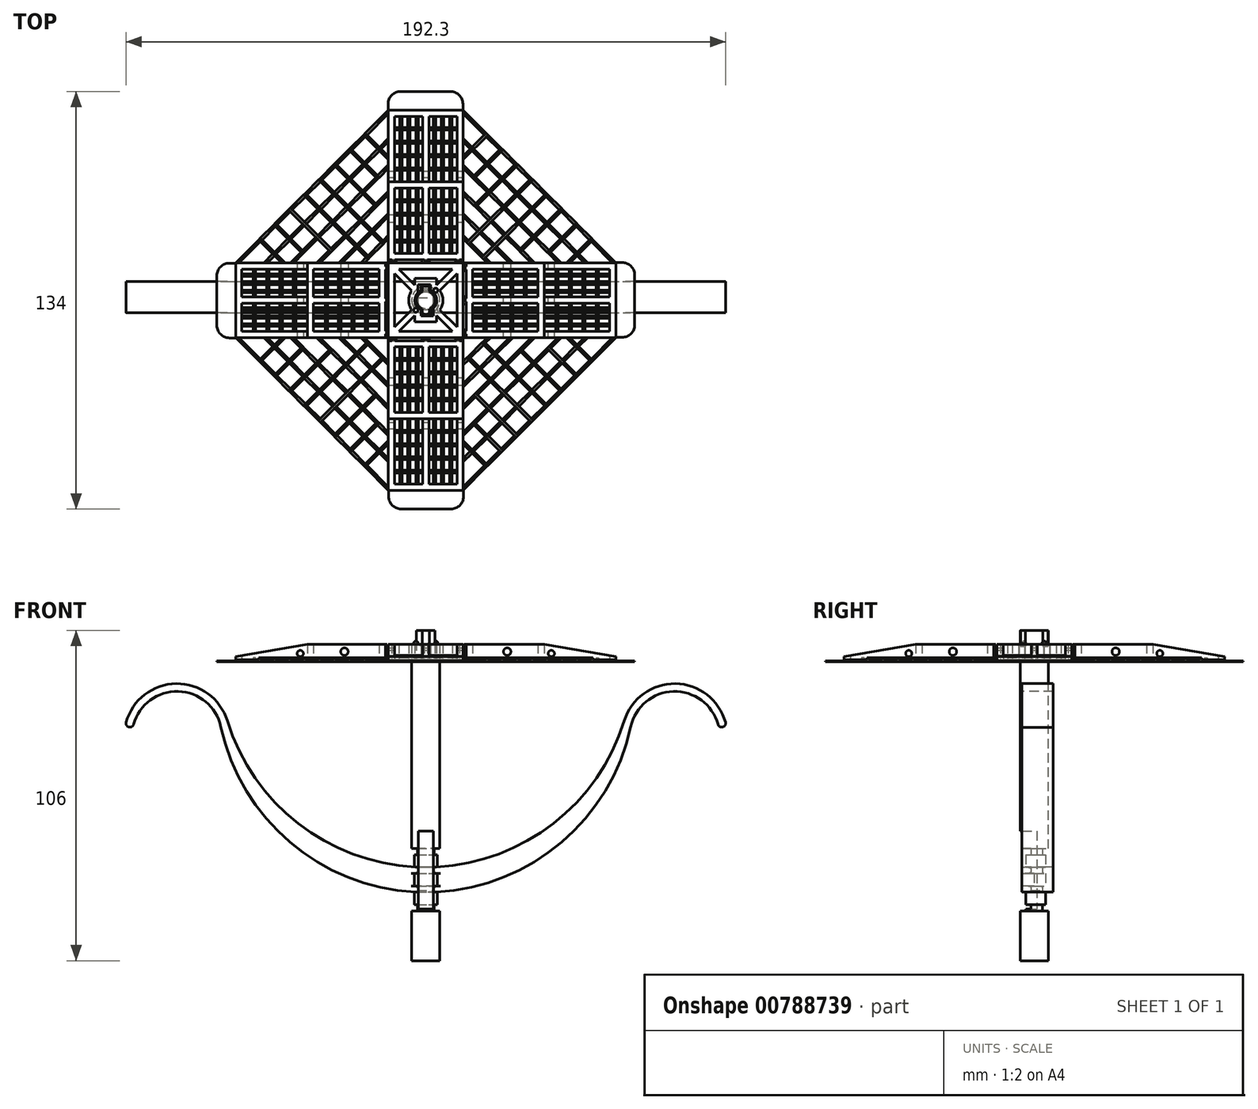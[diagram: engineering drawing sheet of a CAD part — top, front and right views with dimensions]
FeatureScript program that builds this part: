
annotation { "Feature Type Name" : "Feature", "Feature Type Description" : "" }
export const myFeature = defineFeature(function(context is Context, id is Id, definition is map)
    precondition{}
    {
        {
            var Q0;
            Q0=qCreatedBy(makeId("Top.planeOp"),FACE);
            var sketch = newSketch(context, id + "F0", { "sketchPlane" : qUnion([Q0])});
            skLineSegment(sketch, "E0", {"start": v(0, -70.19) * mm, "end": v(0, 72.49) * mm, "construction": true});
            skLineSegment(sketch, "E1", {"start": v(-72.03, 0) * mm, "end": v(73.38, 0) * mm, "construction": true});
            skLineSegment(sketch, "E2", {"start": v(-51.26, -51.26) * mm, "end": v(59.52, 59.52) * mm, "construction": true});
            skLineSegment(sketch, "E3", {"start": v(-54.32, 54.32) * mm, "end": v(52.75, -52.75) * mm, "construction": true});
            skCircle(sketch, "E4", {"center": v(0, 0) * mm, "radius": 3.5 * mm, "construction": true});
            skCircle(sketch, "E5", {"center": v(0, 0) * mm, "radius": 4.5 * mm, "construction": true});
            skSolve(sketch);
        }
        {
            var Q0;
            Q0=qCreatedBy(makeId("Top.planeOp"),FACE);
            var sketch = newSketch(context, id + "F1", { "sketchPlane" : qUnion([Q0])});
            skLineSegment(sketch, "E6.bottom", {"start": v(12, 12) * mm, "end": v(-12, 12) * mm});
            skLineSegment(sketch, "E6.top", {"start": v(12, -12) * mm, "end": v(-12, -12) * mm});
            skLineSegment(sketch, "E6.left", {"start": v(12, 12) * mm, "end": v(12, -12) * mm});
            skLineSegment(sketch, "E6.right", {"start": v(-12, 12) * mm, "end": v(-12, -12) * mm});
            skPoint(sketch, "E6.middle", {"position": v(0, 0) * mm});
            skLineSegment(sketch, "E7.bottom", {"start": v(1.5, -5) * mm, "end": v(-1.5, -5) * mm});
            skLineSegment(sketch, "E7.top", {"start": v(1.5, 5) * mm, "end": v(-1.5, 5) * mm});
            skLineSegment(sketch, "E7.left", {"start": v(1.5, -5) * mm, "end": v(1.5, -3.16) * mm});
            skLineSegment(sketch, "E7.right", {"start": v(-1.5, -5) * mm, "end": v(-1.5, -3.16) * mm});
            skLineSegment(sketch, "E8.bottom", {"start": v(8.59, 10) * mm, "end": v(1, 10) * mm});
            skLineSegment(sketch, "E8.top", {"start": v(8.59, -10) * mm, "end": v(1, -10) * mm});
            skLineSegment(sketch, "E8.left", {"start": v(10, 8.59) * mm, "end": v(10, -8.59) * mm});
            skLineSegment(sketch, "E8.right", {"start": v(-10, 8.59) * mm, "end": v(-10, -8.59) * mm});
            skLineSegment(sketch, "E9.trimOffspring", {"start": v(-1.5, 3.16) * mm, "end": v(-1.5, 5) * mm});
            skLineSegment(sketch, "E10.trimOffspring", {"start": v(1.5, 3.16) * mm, "end": v(1.5, 5) * mm});
            skLineSegment(sketch, "E11.left", {"start": v(10, -1) * mm, "end": v(10, 1) * mm});
            skLineSegment(sketch, "E11.right", {"start": v(-10, -1) * mm, "end": v(-10, 1) * mm});
            skPoint(sketch, "E12.middle", {"position": v(0, 8.75) * mm});
            skPoint(sketch, "E12.middle.positionSnap0", {"position": v(0, 10) * mm});
            skPoint(sketch, "E12.centerSnap0", {"position": v(0, 10) * mm});
            skPoint(sketch, "E13.middle", {"position": v(0, -8.75) * mm});
            skPoint(sketch, "E13.cornerSnap0", {"position": v(0, -10) * mm});
            skLineSegment(sketch, "E14.trimOffspring", {"start": v(-1, 10) * mm, "end": v(-8.59, 10) * mm});
            skLineSegment(sketch, "E15.trimOffspring", {"start": v(-1, -10) * mm, "end": v(-8.59, -10) * mm});
            skArc(sketch, "E16", {"start": v(1.5, -3.16) * mm, "mid": v(3.5, 0) * mm, "end": v(1.5, 3.16) * mm});
            skLineSegment(sketch, "E17", {"start": v(-10, -8.59) * mm, "end": v(-4.53, -3.12) * mm});
            skLineSegment(sketch, "E18", {"start": v(-8.59, -10) * mm, "end": v(-3.5, -4.91) * mm});
            skLineSegment(sketch, "E19", {"start": v(-10, 8.59) * mm, "end": v(-4.53, 3.12) * mm});
            skLineSegment(sketch, "E20", {"start": v(10, -8.59) * mm, "end": v(4.53, -3.12) * mm});
            skPoint(sketch, "E21.orphan", {"position": v(-10, -10) * mm});
            skPoint(sketch, "E22.orphan", {"position": v(10, -10) * mm});
            skPoint(sketch, "E23.orphan", {"position": v(10, 10) * mm});
            skPoint(sketch, "E24.orphan", {"position": v(-10, 10) * mm});
            skArc(sketch, "E25.trimOffspring", {"start": v(-4.53, 3.12) * mm, "mid": v(-5.5, 0) * mm, "end": v(-4.53, -3.12) * mm});
            skLineSegment(sketch, "E26.trimOffspring", {"start": v(-3.5, 4.91) * mm, "end": v(-8.59, 10) * mm});
            skLineSegment(sketch, "E27.trimOffspring", {"start": v(4.53, 3.12) * mm, "end": v(10, 8.59) * mm});
            skLineSegment(sketch, "E28.trimOffspring", {"start": v(3.5, 4.91) * mm, "end": v(8.59, 10) * mm});
            skLineSegment(sketch, "E29.trimOffspring", {"start": v(3.5, -4.91) * mm, "end": v(8.59, -10) * mm});
            skArc(sketch, "E30.trimOffspring", {"start": v(4.53, -3.12) * mm, "mid": v(5.5, 0) * mm, "end": v(4.53, 3.12) * mm});
            skLineSegment(sketch, "E31.bottom", {"start": v(3.5, -7) * mm, "end": v(-3.5, -7) * mm});
            skLineSegment(sketch, "E31.top", {"start": v(3.5, 7) * mm, "end": v(-3.5, 7) * mm});
            skLineSegment(sketch, "E31.left", {"start": v(3.5, -7) * mm, "end": v(3.5, -4.91) * mm});
            skLineSegment(sketch, "E31.right", {"start": v(-3.5, -7) * mm, "end": v(-3.5, -4.91) * mm});
            skLineSegment(sketch, "E32", {"start": v(-1, -10) * mm, "end": v(1, -10) * mm});
            skLineSegment(sketch, "E33", {"start": v(1, 10) * mm, "end": v(-1, 10) * mm});
            skLineSegment(sketch, "E34.trimOffspring", {"start": v(-3.5, 0) * mm, "end": v(-3.5, 7) * mm});
            skArc(sketch, "E35.trimOffspring", {"start": v(-1.5, 3.16) * mm, "mid": v(-3.5, 0) * mm, "end": v(-1.5, -3.16) * mm});
            skLineSegment(sketch, "E36.trimOffspring", {"start": v(3.5, 4.91) * mm, "end": v(3.5, 7) * mm});
            skSolve(sketch);
        }
        {
            var Q0;
            Q0 = qSketchRegion(id + "F1", true);
            extrude(context, id + "F2", {"entities" : qUnion([Q0]), "depth" : 5 * mm, "offsetDistance" : 25 * mm, "hasSecondDirection" : true, "secondDirectionOppositeDirection" : true, "secondDirectionDepth" : .6 * mm});
        }
        {
            var Q0;
            Q0=qCreatedBy(makeId("Top.planeOp"),FACE);
            var sketch = newSketch(context, id + "F3", { "sketchPlane" : qUnion([Q0])});
            skLineSegment(sketch, "E37.bottom", {"start": v(-13, 12) * mm, "end": v(-61, 12) * mm});
            skLineSegment(sketch, "E37.top", {"start": v(-13, -12) * mm, "end": v(-61, -12) * mm});
            skLineSegment(sketch, "E37.left", {"start": v(-13, 12) * mm, "end": v(-13, -12) * mm});
            skLineSegment(sketch, "E37.right", {"start": v(-61, 12) * mm, "end": v(-61, -12) * mm});
            skPoint(sketch, "E37.middle", {"position": v(-37, 0) * mm});
            skLineSegment(sketch, "E38.bottom", {"start": v(-15, 10) * mm, "end": v(-36, 10) * mm});
            skLineSegment(sketch, "E38.top", {"start": v(-15, -10) * mm, "end": v(-36, -10) * mm});
            skLineSegment(sketch, "E38.left", {"start": v(-15, 10) * mm, "end": v(-15, 1) * mm});
            skLineSegment(sketch, "E38.right", {"start": v(-59, 10) * mm, "end": v(-59, 1) * mm});
            skLineSegment(sketch, "E39.bottom", {"start": v(-15, 1) * mm, "end": v(-36, 1) * mm});
            skLineSegment(sketch, "E39.top", {"start": v(-15, -1) * mm, "end": v(-36, -1) * mm});
            skLineSegment(sketch, "E40.left", {"start": v(-36, 10) * mm, "end": v(-36, 1) * mm});
            skLineSegment(sketch, "E40.right", {"start": v(-38, 10) * mm, "end": v(-38, 1) * mm});
            skLineSegment(sketch, "E41.trimOffspring", {"start": v(-38, 10) * mm, "end": v(-59, 10) * mm});
            skLineSegment(sketch, "E42.trimOffspring", {"start": v(-15, -1) * mm, "end": v(-15, -10) * mm});
            skLineSegment(sketch, "E43.trimOffspring", {"start": v(-38, -10) * mm, "end": v(-59, -10) * mm});
            skLineSegment(sketch, "E44.trimOffspring", {"start": v(-38, -1) * mm, "end": v(-59, -1) * mm});
            skLineSegment(sketch, "E45.trimOffspring", {"start": v(-38, 1) * mm, "end": v(-59, 1) * mm});
            skLineSegment(sketch, "E46.trimOffspring", {"start": v(-36, -1) * mm, "end": v(-36, -10) * mm});
            skLineSegment(sketch, "E47.trimOffspring", {"start": v(-38, -1) * mm, "end": v(-38, -10) * mm});
            skLineSegment(sketch, "E48.trimOffspring", {"start": v(-59, -1) * mm, "end": v(-59, -10) * mm});
            skSolve(sketch);
        }
        {
            var Q0;
            Q0 = qSketchRegion(id + "F3", true);
            extrude(context, id + "F4", {"entities" : qUnion([Q0]), "depth" : 5 * mm, "offsetDistance" : 25 * mm, "hasSecondDirection" : true, "secondDirectionOppositeDirection" : true, "secondDirectionDepth" : .6 * mm});
        }
        {
            var Q0;
            Q0=qCreatedBy(makeId("Front.planeOp"),FACE);
            var sketch = newSketch(context, id + "F5", { "sketchPlane" : qUnion([Q0])});
            skLineSegment(sketch, "E49", {"start": v(0, 58.8) * mm, "end": v(0, -68.64) * mm, "construction": true});
            skSolve(sketch);
        }
        {
            var Q0;
            Q0=makeQuery(id+"F4.opExtrude","SWEPT_BODY",BODY,{"disambiguationData":[OSD([sQuery(id+"F3.wireOp",EDGE,"E37.bottom"),sQuery(id+"F3.wireOp",EDGE,"E37.top"),sQuery(id+"F3.wireOp",EDGE,"E37.left"),sQuery(id+"F3.wireOp",EDGE,"E37.right"),sQuery(id+"F3.wireOp",EDGE,"E38.bottom"),sQuery(id+"F3.wireOp",EDGE,"E38.top"),sQuery(id+"F3.wireOp",EDGE,"E38.left"),sQuery(id+"F3.wireOp",EDGE,"E38.right"),sQuery(id+"F3.wireOp",EDGE,"E39.bottom"),sQuery(id+"F3.wireOp",EDGE,"E39.top"),sQuery(id+"F3.wireOp",EDGE,"E40.left"),sQuery(id+"F3.wireOp",EDGE,"E40.right"),sQuery(id+"F3.wireOp",EDGE,"E41.trimOffspring"),sQuery(id+"F3.wireOp",EDGE,"E42.trimOffspring"),sQuery(id+"F3.wireOp",EDGE,"E43.trimOffspring"),sQuery(id+"F3.wireOp",EDGE,"E44.trimOffspring"),sQuery(id+"F3.wireOp",EDGE,"E45.trimOffspring"),sQuery(id+"F3.wireOp",EDGE,"E46.trimOffspring"),sQuery(id+"F3.wireOp",EDGE,"E47.trimOffspring"),sQuery(id+"F3.wireOp",EDGE,"E48.trimOffspring")])]});
            var Q1;
            Q1=sQuery(id+"F5.wireOp",EDGE,"E49");
            circularPattern(context, id + "F6", {"entities" : qUnion([Q0]), "axis" : qUnion([Q1]), "angle" : 360 * degree, "instanceCount" : 4, "equalSpace" : true});
        }
        {
            var Q0;
            Q0=qCreatedBy(makeId("Top.planeOp"),FACE);
            var sketch = newSketch(context, id + "F7", { "sketchPlane" : qUnion([Q0])});
            skLineSegment(sketch, "E50", {"start": v(-61, 12) * mm, "end": v(-61, -12) * mm});
            skLineSegment(sketch, "E51", {"start": v(-61, -12) * mm, "end": v(-12, -61) * mm});
            skLineSegment(sketch, "E52", {"start": v(-12, -61) * mm, "end": v(12, -61) * mm});
            skLineSegment(sketch, "E53", {"start": v(12, -61) * mm, "end": v(61, -12) * mm});
            skLineSegment(sketch, "E54", {"start": v(61, -12) * mm, "end": v(61, 12) * mm});
            skLineSegment(sketch, "E55", {"start": v(61, 12) * mm, "end": v(12, 61) * mm});
            skLineSegment(sketch, "E56", {"start": v(12, 61) * mm, "end": v(-12, 61) * mm});
            skLineSegment(sketch, "E57", {"start": v(-12, 61) * mm, "end": v(-61, 12) * mm});
            skLineSegment(sketch, "E58", {"start": v(-60.2, -11.67) * mm, "end": v(-11.67, -60.2) * mm});
            skLineSegment(sketch, "E59", {"start": v(-11.67, -60.2) * mm, "end": v(11.67, -60.2) * mm});
            skLineSegment(sketch, "E60", {"start": v(11.67, -60.2) * mm, "end": v(60.2, -11.67) * mm});
            skLineSegment(sketch, "E61", {"start": v(60.2, -11.67) * mm, "end": v(60.2, 11.67) * mm});
            skLineSegment(sketch, "E62", {"start": v(60.2, 11.67) * mm, "end": v(11.67, 60.2) * mm});
            skLineSegment(sketch, "E63", {"start": v(11.67, 60.2) * mm, "end": v(-11.67, 60.2) * mm});
            skLineSegment(sketch, "E64", {"start": v(-11.67, 60.2) * mm, "end": v(-60.2, 11.67) * mm});
            skLineSegment(sketch, "E65", {"start": v(-60.2, 11.67) * mm, "end": v(-60.2, -11.67) * mm});
            skSolve(sketch);
        }
        {
            var Q0;
            Q0 = qSketchRegion(id + "F7", true);
            extrude(context, id + "F8", {"entities" : qUnion([Q0]), "oppositeDirection" : true, "depth" : .6 * mm, "offsetDistance" : 25 * mm});
        }
        {
            var Q0;
            Q0=makeQuery(id+"F4.opExtrude","SWEPT_BODY",BODY,{"disambiguationData":[OSD([sQuery(id+"F3.wireOp",EDGE,"E37.bottom"),sQuery(id+"F3.wireOp",EDGE,"E37.top"),sQuery(id+"F3.wireOp",EDGE,"E37.left"),sQuery(id+"F3.wireOp",EDGE,"E37.right"),sQuery(id+"F3.wireOp",EDGE,"E38.bottom"),sQuery(id+"F3.wireOp",EDGE,"E38.top"),sQuery(id+"F3.wireOp",EDGE,"E38.left"),sQuery(id+"F3.wireOp",EDGE,"E38.right"),sQuery(id+"F3.wireOp",EDGE,"E39.bottom"),sQuery(id+"F3.wireOp",EDGE,"E39.top"),sQuery(id+"F3.wireOp",EDGE,"E40.left"),sQuery(id+"F3.wireOp",EDGE,"E40.right"),sQuery(id+"F3.wireOp",EDGE,"E41.trimOffspring"),sQuery(id+"F3.wireOp",EDGE,"E42.trimOffspring"),sQuery(id+"F3.wireOp",EDGE,"E43.trimOffspring"),sQuery(id+"F3.wireOp",EDGE,"E44.trimOffspring"),sQuery(id+"F3.wireOp",EDGE,"E45.trimOffspring"),sQuery(id+"F3.wireOp",EDGE,"E46.trimOffspring"),sQuery(id+"F3.wireOp",EDGE,"E47.trimOffspring"),sQuery(id+"F3.wireOp",EDGE,"E48.trimOffspring")])]});
            var Q1;
            Q1=makeQuery(id+"F6.opPattern","COPY",BODY,{"derivedFrom":makeQuery(id+"F4.opExtrude","SWEPT_BODY",BODY,{"disambiguationData":[OSD([sQuery(id+"F3.wireOp",EDGE,"E37.bottom"),sQuery(id+"F3.wireOp",EDGE,"E37.top"),sQuery(id+"F3.wireOp",EDGE,"E37.left"),sQuery(id+"F3.wireOp",EDGE,"E37.right"),sQuery(id+"F3.wireOp",EDGE,"E38.bottom"),sQuery(id+"F3.wireOp",EDGE,"E38.top"),sQuery(id+"F3.wireOp",EDGE,"E38.left"),sQuery(id+"F3.wireOp",EDGE,"E38.right"),sQuery(id+"F3.wireOp",EDGE,"E39.bottom"),sQuery(id+"F3.wireOp",EDGE,"E39.top"),sQuery(id+"F3.wireOp",EDGE,"E40.left"),sQuery(id+"F3.wireOp",EDGE,"E40.right"),sQuery(id+"F3.wireOp",EDGE,"E41.trimOffspring"),sQuery(id+"F3.wireOp",EDGE,"E42.trimOffspring"),sQuery(id+"F3.wireOp",EDGE,"E43.trimOffspring"),sQuery(id+"F3.wireOp",EDGE,"E44.trimOffspring"),sQuery(id+"F3.wireOp",EDGE,"E45.trimOffspring"),sQuery(id+"F3.wireOp",EDGE,"E46.trimOffspring"),sQuery(id+"F3.wireOp",EDGE,"E47.trimOffspring"),sQuery(id+"F3.wireOp",EDGE,"E48.trimOffspring")])]}),"instanceName":"1"});
            var Q2;
            Q2=makeQuery(id+"F6.opPattern","COPY",BODY,{"derivedFrom":makeQuery(id+"F4.opExtrude","SWEPT_BODY",BODY,{"disambiguationData":[OSD([sQuery(id+"F3.wireOp",EDGE,"E37.bottom"),sQuery(id+"F3.wireOp",EDGE,"E37.top"),sQuery(id+"F3.wireOp",EDGE,"E37.left"),sQuery(id+"F3.wireOp",EDGE,"E37.right"),sQuery(id+"F3.wireOp",EDGE,"E38.bottom"),sQuery(id+"F3.wireOp",EDGE,"E38.top"),sQuery(id+"F3.wireOp",EDGE,"E38.left"),sQuery(id+"F3.wireOp",EDGE,"E38.right"),sQuery(id+"F3.wireOp",EDGE,"E39.bottom"),sQuery(id+"F3.wireOp",EDGE,"E39.top"),sQuery(id+"F3.wireOp",EDGE,"E40.left"),sQuery(id+"F3.wireOp",EDGE,"E40.right"),sQuery(id+"F3.wireOp",EDGE,"E41.trimOffspring"),sQuery(id+"F3.wireOp",EDGE,"E42.trimOffspring"),sQuery(id+"F3.wireOp",EDGE,"E43.trimOffspring"),sQuery(id+"F3.wireOp",EDGE,"E44.trimOffspring"),sQuery(id+"F3.wireOp",EDGE,"E45.trimOffspring"),sQuery(id+"F3.wireOp",EDGE,"E46.trimOffspring"),sQuery(id+"F3.wireOp",EDGE,"E47.trimOffspring"),sQuery(id+"F3.wireOp",EDGE,"E48.trimOffspring")])]}),"instanceName":"2"});
            var Q3;
            Q3=makeQuery(id+"F6.opPattern","COPY",BODY,{"derivedFrom":makeQuery(id+"F4.opExtrude","SWEPT_BODY",BODY,{"disambiguationData":[OSD([sQuery(id+"F3.wireOp",EDGE,"E37.bottom"),sQuery(id+"F3.wireOp",EDGE,"E37.top"),sQuery(id+"F3.wireOp",EDGE,"E37.left"),sQuery(id+"F3.wireOp",EDGE,"E37.right"),sQuery(id+"F3.wireOp",EDGE,"E38.bottom"),sQuery(id+"F3.wireOp",EDGE,"E38.top"),sQuery(id+"F3.wireOp",EDGE,"E38.left"),sQuery(id+"F3.wireOp",EDGE,"E38.right"),sQuery(id+"F3.wireOp",EDGE,"E39.bottom"),sQuery(id+"F3.wireOp",EDGE,"E39.top"),sQuery(id+"F3.wireOp",EDGE,"E40.left"),sQuery(id+"F3.wireOp",EDGE,"E40.right"),sQuery(id+"F3.wireOp",EDGE,"E41.trimOffspring"),sQuery(id+"F3.wireOp",EDGE,"E42.trimOffspring"),sQuery(id+"F3.wireOp",EDGE,"E43.trimOffspring"),sQuery(id+"F3.wireOp",EDGE,"E44.trimOffspring"),sQuery(id+"F3.wireOp",EDGE,"E45.trimOffspring"),sQuery(id+"F3.wireOp",EDGE,"E46.trimOffspring"),sQuery(id+"F3.wireOp",EDGE,"E47.trimOffspring"),sQuery(id+"F3.wireOp",EDGE,"E48.trimOffspring")])]}),"instanceName":"3"});
            var Q4;
            Q4=makeQuery(id+"F8.opExtrude","SWEPT_BODY",BODY,{"disambiguationData":[OSD([sQuery(id+"F7.wireOp",EDGE,"E50"),sQuery(id+"F7.wireOp",EDGE,"E51"),sQuery(id+"F7.wireOp",EDGE,"E52"),sQuery(id+"F7.wireOp",EDGE,"E53"),sQuery(id+"F7.wireOp",EDGE,"E54"),sQuery(id+"F7.wireOp",EDGE,"E55"),sQuery(id+"F7.wireOp",EDGE,"E56"),sQuery(id+"F7.wireOp",EDGE,"E57"),sQuery(id+"F7.wireOp",EDGE,"E58"),sQuery(id+"F7.wireOp",EDGE,"E59"),sQuery(id+"F7.wireOp",EDGE,"E60"),sQuery(id+"F7.wireOp",EDGE,"E61"),sQuery(id+"F7.wireOp",EDGE,"E62"),sQuery(id+"F7.wireOp",EDGE,"E63"),sQuery(id+"F7.wireOp",EDGE,"E64"),sQuery(id+"F7.wireOp",EDGE,"E65")])]});
            booleanBodies(context, id + "F9", {"operationType" : BooleanOperationType.UNION, "tools" : qUnion([Q0, Q1, Q2, Q3, Q4])});
        }
        {
            var Q0;
            Q0=qCreatedBy(makeId("Top.planeOp"),FACE);
            var sketch = newSketch(context, id + "F10", { "sketchPlane" : qUnion([Q0])});
            skLineSegment(sketch, "E66.bottom", {"start": v(-13, -12) * mm, "end": v(-11.2, -12) * mm});
            skLineSegment(sketch, "E66.top", {"start": v(-13, -11.2) * mm, "end": v(-11.2, -11.2) * mm});
            skLineSegment(sketch, "E66.left", {"start": v(-13, -12) * mm, "end": v(-13, -11.2) * mm});
            skLineSegment(sketch, "E66.right", {"start": v(-11.2, -12) * mm, "end": v(-11.2, -11.2) * mm});
            skLineSegment(sketch, "E67.0.1.0", {"start": v(-13, -9.5) * mm, "end": v(-13, -8.7) * mm});
            skLineSegment(sketch, "E67.0.1.1", {"start": v(-13, -9.5) * mm, "end": v(-11.2, -9.5) * mm});
            skLineSegment(sketch, "E67.0.1.2", {"start": v(-11.2, -9.5) * mm, "end": v(-11.2, -8.7) * mm});
            skLineSegment(sketch, "E67.0.4.0", {"start": v(-13, -2) * mm, "end": v(-13, -1.2) * mm});
            skLineSegment(sketch, "E67.0.4.2", {"start": v(-11.2, -2) * mm, "end": v(-11.2, -1.2) * mm});
            skLineSegment(sketch, "E67.0.4.3", {"start": v(-13, -1.2) * mm, "end": v(-11.2, -1.2) * mm});
            skLineSegment(sketch, "E67.direction1", {"start": v(-13, -12) * mm, "end": v(12, -12) * mm, "construction": true});
            skLineSegment(sketch, "E67.direction2", {"start": v(-13, -12) * mm, "end": v(-13, -9.5) * mm, "construction": true});
            skLineSegment(sketch, "E68.MirrorCS", {"start": v(-13, 12) * mm, "end": v(-13, 11.2) * mm});
            skLineSegment(sketch, "E69.MirrorCS", {"start": v(-13, 2) * mm, "end": v(-13, 1.2) * mm});
            skLineSegment(sketch, "E70.MirrorCS", {"start": v(-13, 12) * mm, "end": v(-13, 9.5) * mm, "construction": true});
            skLineSegment(sketch, "E71.MirrorCS", {"start": v(-13, 1.2) * mm, "end": v(-11.2, 1.2) * mm});
            skLineSegment(sketch, "E72.MirrorCS", {"start": v(-11.2, 12) * mm, "end": v(-11.2, 11.2) * mm});
            skLineSegment(sketch, "E73.MirrorCS", {"start": v(-13, 12) * mm, "end": v(-11.2, 12) * mm});
            skLineSegment(sketch, "E74.MirrorCS", {"start": v(-13, 9.5) * mm, "end": v(-13, 8.7) * mm});
            skLineSegment(sketch, "E75.MirrorCS", {"start": v(-11.2, 2) * mm, "end": v(-11.2, 1.2) * mm});
            skLineSegment(sketch, "E76.MirrorCS", {"start": v(-13, 11.2) * mm, "end": v(-11.2, 11.2) * mm});
            skLineSegment(sketch, "E77.MirrorCS", {"start": v(-11.2, 9.5) * mm, "end": v(-11.2, 8.7) * mm});
            skLineSegment(sketch, "E78.MirrorCS", {"start": v(-13, 9.5) * mm, "end": v(-11.2, 9.5) * mm});
            skLineSegment(sketch, "E79.bottom", {"start": v(-59, -8.4) * mm, "end": v(-15, -8.4) * mm});
            skLineSegment(sketch, "E79.top", {"start": v(-59, -7.6) * mm, "end": v(-15, -7.6) * mm});
            skLineSegment(sketch, "E79.left", {"start": v(-59, -8.4) * mm, "end": v(-59, -7.6) * mm});
            skLineSegment(sketch, "E79.right", {"start": v(-15, -8.4) * mm, "end": v(-15, -7.6) * mm});
            skLineSegment(sketch, "E80.0.1.0", {"start": v(-59, -5.8) * mm, "end": v(-59, -5) * mm});
            skLineSegment(sketch, "E80.0.1.1", {"start": v(-59, -5.8) * mm, "end": v(-15, -5.8) * mm});
            skLineSegment(sketch, "E80.0.1.2", {"start": v(-59, -5) * mm, "end": v(-15, -5) * mm});
            skLineSegment(sketch, "E80.0.1.3", {"start": v(-15, -5.8) * mm, "end": v(-15, -5) * mm});
            skLineSegment(sketch, "E80.0.2.0", {"start": v(-59, -3.2) * mm, "end": v(-59, -2.4) * mm});
            skLineSegment(sketch, "E80.0.2.1", {"start": v(-59, -3.2) * mm, "end": v(-15, -3.2) * mm});
            skLineSegment(sketch, "E80.0.2.2", {"start": v(-59, -2.4) * mm, "end": v(-15, -2.4) * mm});
            skLineSegment(sketch, "E80.0.2.3", {"start": v(-15, -3.2) * mm, "end": v(-15, -2.4) * mm});
            skLineSegment(sketch, "E80.direction1", {"start": v(-59, -8.4) * mm, "end": v(-34, -8.4) * mm, "construction": true});
            skLineSegment(sketch, "E80.direction2", {"start": v(-59, -8.4) * mm, "end": v(-59, -5.8) * mm, "construction": true});
            skLineSegment(sketch, "E81.MirrorCS", {"start": v(-15, 3.2) * mm, "end": v(-15, 2.4) * mm});
            skLineSegment(sketch, "E82.MirrorCS", {"start": v(-59, 3.2) * mm, "end": v(-59, 2.4) * mm});
            skLineSegment(sketch, "E83.MirrorCS", {"start": v(-59, 8.4) * mm, "end": v(-59, 7.6) * mm});
            skLineSegment(sketch, "E84.MirrorCS", {"start": v(-15, 5.8) * mm, "end": v(-15, 5) * mm});
            skLineSegment(sketch, "E85.MirrorCS", {"start": v(-59, 8.4) * mm, "end": v(-34, 8.4) * mm, "construction": true});
            skLineSegment(sketch, "E86.MirrorCS", {"start": v(-59, 5) * mm, "end": v(-15, 5) * mm});
            skLineSegment(sketch, "E87.MirrorCS", {"start": v(-59, 3.2) * mm, "end": v(-15, 3.2) * mm});
            skLineSegment(sketch, "E88.MirrorCS", {"start": v(-59, 5.8) * mm, "end": v(-15, 5.8) * mm});
            skLineSegment(sketch, "E89.MirrorCS", {"start": v(-59, 8.4) * mm, "end": v(-59, 5.8) * mm, "construction": true});
            skLineSegment(sketch, "E90.MirrorCS", {"start": v(-59, 8.4) * mm, "end": v(-15, 8.4) * mm});
            skLineSegment(sketch, "E91.MirrorCS", {"start": v(-59, 7.6) * mm, "end": v(-15, 7.6) * mm});
            skLineSegment(sketch, "E92.MirrorCS", {"start": v(-59, 2.4) * mm, "end": v(-15, 2.4) * mm});
            skLineSegment(sketch, "E93.MirrorCS", {"start": v(-59, 5.8) * mm, "end": v(-59, 5) * mm});
            skLineSegment(sketch, "E94.MirrorCS", {"start": v(-15, 8.4) * mm, "end": v(-15, 7.6) * mm});
            skLineSegment(sketch, "E95.bottom", {"start": v(-13, -12) * mm, "end": v(-15, -12) * mm});
            skLineSegment(sketch, "E95.top", {"start": v(-13, 12) * mm, "end": v(-15, 12) * mm});
            skLineSegment(sketch, "E95.left", {"start": v(-13, -12) * mm, "end": v(-13, 12) * mm});
            skLineSegment(sketch, "E95.right", {"start": v(-15, -12) * mm, "end": v(-15, 8.4) * mm});
            skLineSegment(sketch, "E96", {"start": v(-15, 12) * mm, "end": v(-15, 8.4) * mm});
            skLineSegment(sketch, "E97", {"start": v(-13, -8.7) * mm, "end": v(-13, -2) * mm});
            skLineSegment(sketch, "E98", {"start": v(-11.2, -8.7) * mm, "end": v(-11.2, -2) * mm});
            skLineSegment(sketch, "E99", {"start": v(-13, 2) * mm, "end": v(-13, 8.7) * mm});
            skLineSegment(sketch, "E100", {"start": v(-11.2, 2) * mm, "end": v(-11.2, 8.7) * mm});
            skSolve(sketch);
        }
        {
            var Q0;
            Q0=qCreatedBy(makeId("Top.planeOp"),FACE);
            var sketch = newSketch(context, id + "F11", { "sketchPlane" : qUnion([Q0])});
            skLineSegment(sketch, "E101.bottom", {"start": v(-13, 10.85) * mm, "end": v(-12.4, 10.85) * mm});
            skLineSegment(sketch, "E101.top", {"start": v(-13, 9.85) * mm, "end": v(-12.4, 9.85) * mm});
            skLineSegment(sketch, "E101.left", {"start": v(-13, 10.85) * mm, "end": v(-13, 9.85) * mm});
            skLineSegment(sketch, "E101.right", {"start": v(-12.4, 10.85) * mm, "end": v(-12.4, 9.85) * mm});
            skLineSegment(sketch, "E102.bottom", {"start": v(-13, 0.5) * mm, "end": v(-12.4, 0.5) * mm});
            skLineSegment(sketch, "E102.top", {"start": v(-13, -0.5) * mm, "end": v(-12.4, -0.5) * mm});
            skLineSegment(sketch, "E102.left", {"start": v(-13, 0.5) * mm, "end": v(-13, -0.5) * mm});
            skLineSegment(sketch, "E102.right", {"start": v(-12.4, 0.5) * mm, "end": v(-12.4, -0.5) * mm});
            skLineSegment(sketch, "E103.bottom", {"start": v(-13, -9.85) * mm, "end": v(-12.4, -9.85) * mm});
            skLineSegment(sketch, "E103.top", {"start": v(-13, -10.85) * mm, "end": v(-12.4, -10.85) * mm});
            skLineSegment(sketch, "E103.left", {"start": v(-13, -9.85) * mm, "end": v(-13, -10.85) * mm});
            skLineSegment(sketch, "E103.right", {"start": v(-12.4, -9.85) * mm, "end": v(-12.4, -10.85) * mm});
            skLineSegment(sketch, "E104.1.0", {"start": v(-0.5, -12.4) * mm, "end": v(0.5, -12.4) * mm});
            skLineSegment(sketch, "E104.1.1", {"start": v(-0.5, -13) * mm, "end": v(0.5, -13) * mm});
            skLineSegment(sketch, "E104.1.2", {"start": v(-10.85, -13) * mm, "end": v(-9.85, -13) * mm});
            skLineSegment(sketch, "E104.1.3", {"start": v(9.85, -12.4) * mm, "end": v(10.85, -12.4) * mm});
            skLineSegment(sketch, "E104.1.4", {"start": v(-10.85, -12.4) * mm, "end": v(-9.85, -12.4) * mm});
            skLineSegment(sketch, "E104.1.5", {"start": v(9.85, -13) * mm, "end": v(10.85, -13) * mm});
            skLineSegment(sketch, "E104.1.6", {"start": v(0.5, -13) * mm, "end": v(0.5, -12.4) * mm});
            skLineSegment(sketch, "E104.1.7", {"start": v(-9.85, -13) * mm, "end": v(-9.85, -12.4) * mm});
            skLineSegment(sketch, "E104.1.8", {"start": v(-10.85, -13) * mm, "end": v(-10.85, -12.4) * mm});
            skLineSegment(sketch, "E104.1.9", {"start": v(10.85, -13) * mm, "end": v(10.85, -12.4) * mm});
            skLineSegment(sketch, "E104.1.10", {"start": v(9.85, -13) * mm, "end": v(9.85, -12.4) * mm});
            skLineSegment(sketch, "E104.1.11", {"start": v(-0.5, -13) * mm, "end": v(-0.5, -12.4) * mm});
            skLineSegment(sketch, "E104.2.0", {"start": v(12.4, -0.5) * mm, "end": v(12.4, 0.5) * mm});
            skLineSegment(sketch, "E104.2.1", {"start": v(13, -0.5) * mm, "end": v(13, 0.5) * mm});
            skLineSegment(sketch, "E104.2.2", {"start": v(13, -10.85) * mm, "end": v(13, -9.85) * mm});
            skLineSegment(sketch, "E104.2.3", {"start": v(12.4, 9.85) * mm, "end": v(12.4, 10.85) * mm});
            skLineSegment(sketch, "E104.2.4", {"start": v(12.4, -10.85) * mm, "end": v(12.4, -9.85) * mm});
            skLineSegment(sketch, "E104.2.5", {"start": v(13, 9.85) * mm, "end": v(13, 10.85) * mm});
            skLineSegment(sketch, "E104.2.6", {"start": v(13, 0.5) * mm, "end": v(12.4, 0.5) * mm});
            skLineSegment(sketch, "E104.2.7", {"start": v(13, -9.85) * mm, "end": v(12.4, -9.85) * mm});
            skLineSegment(sketch, "E104.2.8", {"start": v(13, -10.85) * mm, "end": v(12.4, -10.85) * mm});
            skLineSegment(sketch, "E104.2.9", {"start": v(13, 10.85) * mm, "end": v(12.4, 10.85) * mm});
            skLineSegment(sketch, "E104.2.10", {"start": v(13, 9.85) * mm, "end": v(12.4, 9.85) * mm});
            skLineSegment(sketch, "E104.2.11", {"start": v(13, -0.5) * mm, "end": v(12.4, -0.5) * mm});
            skLineSegment(sketch, "E104.3.0", {"start": v(0.5, 12.4) * mm, "end": v(-0.5, 12.4) * mm});
            skLineSegment(sketch, "E104.3.1", {"start": v(0.5, 13) * mm, "end": v(-0.5, 13) * mm});
            skLineSegment(sketch, "E104.3.2", {"start": v(10.85, 13) * mm, "end": v(9.85, 13) * mm});
            skLineSegment(sketch, "E104.3.3", {"start": v(-9.85, 12.4) * mm, "end": v(-10.85, 12.4) * mm});
            skLineSegment(sketch, "E104.3.4", {"start": v(10.85, 12.4) * mm, "end": v(9.85, 12.4) * mm});
            skLineSegment(sketch, "E104.3.5", {"start": v(-9.85, 13) * mm, "end": v(-10.85, 13) * mm});
            skLineSegment(sketch, "E104.3.6", {"start": v(-0.5, 13) * mm, "end": v(-0.5, 12.4) * mm});
            skLineSegment(sketch, "E104.3.7", {"start": v(9.85, 13) * mm, "end": v(9.85, 12.4) * mm});
            skLineSegment(sketch, "E104.3.8", {"start": v(10.85, 13) * mm, "end": v(10.85, 12.4) * mm});
            skLineSegment(sketch, "E104.3.9", {"start": v(-10.85, 13) * mm, "end": v(-10.85, 12.4) * mm});
            skLineSegment(sketch, "E104.3.10", {"start": v(-9.85, 13) * mm, "end": v(-9.85, 12.4) * mm});
            skLineSegment(sketch, "E104.3.11", {"start": v(0.5, 13) * mm, "end": v(0.5, 12.4) * mm});
            skPoint(sketch, "E104.center", {"position": v(0, 0) * mm});
            skSolve(sketch);
        }
        {
            var Q0;
            Q0 = qSketchRegion(id + "F11", true);
            var Q1;
            Q1=makeQuery(id+"F4.opExtrude","CAP_FACE",FACE,{"disambiguationData":[OSD([sQuery(id+"F3.wireOp",EDGE,"E37.bottom"),sQuery(id+"F3.wireOp",EDGE,"E37.top"),sQuery(id+"F3.wireOp",EDGE,"E37.left"),sQuery(id+"F3.wireOp",EDGE,"E37.right"),sQuery(id+"F3.wireOp",EDGE,"E38.bottom"),sQuery(id+"F3.wireOp",EDGE,"E38.top"),sQuery(id+"F3.wireOp",EDGE,"E38.left"),sQuery(id+"F3.wireOp",EDGE,"E38.right"),sQuery(id+"F3.wireOp",EDGE,"E39.bottom"),sQuery(id+"F3.wireOp",EDGE,"E39.top"),sQuery(id+"F3.wireOp",EDGE,"E40.left"),sQuery(id+"F3.wireOp",EDGE,"E40.right"),sQuery(id+"F3.wireOp",EDGE,"E41.trimOffspring"),sQuery(id+"F3.wireOp",EDGE,"E42.trimOffspring"),sQuery(id+"F3.wireOp",EDGE,"E43.trimOffspring"),sQuery(id+"F3.wireOp",EDGE,"E44.trimOffspring"),sQuery(id+"F3.wireOp",EDGE,"E45.trimOffspring"),sQuery(id+"F3.wireOp",EDGE,"E46.trimOffspring"),sQuery(id+"F3.wireOp",EDGE,"E47.trimOffspring"),sQuery(id+"F3.wireOp",EDGE,"E48.trimOffspring")])],"isStart":false});
            var Q2;
            Q2=makeQuery(id+"F4.opExtrude","CAP_FACE",FACE,{"disambiguationData":[OSD([sQuery(id+"F3.wireOp",EDGE,"E37.bottom"),sQuery(id+"F3.wireOp",EDGE,"E37.top"),sQuery(id+"F3.wireOp",EDGE,"E37.left"),sQuery(id+"F3.wireOp",EDGE,"E37.right"),sQuery(id+"F3.wireOp",EDGE,"E38.bottom"),sQuery(id+"F3.wireOp",EDGE,"E38.top"),sQuery(id+"F3.wireOp",EDGE,"E38.left"),sQuery(id+"F3.wireOp",EDGE,"E38.right"),sQuery(id+"F3.wireOp",EDGE,"E39.bottom"),sQuery(id+"F3.wireOp",EDGE,"E39.top"),sQuery(id+"F3.wireOp",EDGE,"E40.left"),sQuery(id+"F3.wireOp",EDGE,"E40.right"),sQuery(id+"F3.wireOp",EDGE,"E41.trimOffspring"),sQuery(id+"F3.wireOp",EDGE,"E42.trimOffspring"),sQuery(id+"F3.wireOp",EDGE,"E43.trimOffspring"),sQuery(id+"F3.wireOp",EDGE,"E44.trimOffspring"),sQuery(id+"F3.wireOp",EDGE,"E45.trimOffspring"),sQuery(id+"F3.wireOp",EDGE,"E46.trimOffspring"),sQuery(id+"F3.wireOp",EDGE,"E47.trimOffspring"),sQuery(id+"F3.wireOp",EDGE,"E48.trimOffspring")])],"isStart":false});
            extrude(context, id + "F12", {"entities" : qUnion([Q0]), "operationType" : NewBodyOperationType.ADD, "endBound" : BoundingType.UP_TO_SURFACE, "depth" : 25 * mm, "endBoundEntityFace" : qUnion([Q1]), "offsetDistance" : 25 * mm, "hasSecondDirection" : true, "secondDirectionOppositeDirection" : true, "secondDirectionDepth" : .6 * mm, "secondDirectionBoundEntityFace" : qUnion([Q2])});
        }
        {
            var Q0;
            Q0=makeQuery(id+"F12.opExtrude","CAP_EDGE",EDGE,{"disambiguationData":[OSD([sQuery(id+"F11.wireOp",EDGE,"E103.right")])],"isStart":true});
            var Q1;
            Q1=makeQuery(id+"F12.opExtrude","CAP_EDGE",EDGE,{"disambiguationData":[OSD([sQuery(id+"F11.wireOp",EDGE,"E102.right")])],"isStart":true});
            var Q2;
            Q2=makeQuery(id+"F12.opExtrude","CAP_EDGE",EDGE,{"disambiguationData":[OSD([sQuery(id+"F11.wireOp",EDGE,"E101.right")])],"isStart":true});
            var Q3;
            Q3=makeQuery(id+"F12.opExtrude","CAP_EDGE",EDGE,{"disambiguationData":[OSD([sQuery(id+"F11.wireOp",EDGE,"E104.3.3")])],"isStart":true});
            var Q4;
            Q4=makeQuery(id+"F12.opExtrude","CAP_EDGE",EDGE,{"disambiguationData":[OSD([sQuery(id+"F11.wireOp",EDGE,"E104.3.0")])],"isStart":true});
            var Q5;
            Q5=makeQuery(id+"F12.opExtrude","CAP_EDGE",EDGE,{"disambiguationData":[OSD([sQuery(id+"F11.wireOp",EDGE,"E104.3.4")])],"isStart":true});
            var Q6;
            Q6=makeQuery(id+"F12.opExtrude","CAP_EDGE",EDGE,{"disambiguationData":[OSD([sQuery(id+"F11.wireOp",EDGE,"E104.2.3")])],"isStart":true});
            var Q7;
            Q7=makeQuery(id+"F12.opExtrude","CAP_EDGE",EDGE,{"disambiguationData":[OSD([sQuery(id+"F11.wireOp",EDGE,"E104.2.0")])],"isStart":true});
            var Q8;
            Q8=makeQuery(id+"F12.opExtrude","CAP_EDGE",EDGE,{"disambiguationData":[OSD([sQuery(id+"F11.wireOp",EDGE,"E104.2.4")])],"isStart":true});
            var Q9;
            Q9=makeQuery(id+"F12.opExtrude","CAP_EDGE",EDGE,{"disambiguationData":[OSD([sQuery(id+"F11.wireOp",EDGE,"E104.1.3")])],"isStart":true});
            var Q10;
            Q10=makeQuery(id+"F12.opExtrude","CAP_EDGE",EDGE,{"disambiguationData":[OSD([sQuery(id+"F11.wireOp",EDGE,"E104.1.0")])],"isStart":true});
            var Q11;
            Q11=makeQuery(id+"F12.opExtrude","CAP_EDGE",EDGE,{"disambiguationData":[OSD([sQuery(id+"F11.wireOp",EDGE,"E104.1.4")])],"isStart":true});
            chamfer(context, id + "F13", {"entities" : qUnion([Q0, Q1, Q2, Q3, Q4, Q5, Q6, Q7, Q8, Q9, Q10, Q11]), "width" : .6 * mm, "tangentPropagation" : true});
        }
        {
            var Q0;
            Q0=makeQuery(id+"F12.opExtrude","SWEPT_EDGE",EDGE,{"disambiguationData":[OSD([sQuery(id+"F11.wireOp",EDGE,"E103.top"),sQuery(id+"F11.wireOp",EDGE,"E103.right")])]});
            var Q1;
            Q1=makeQuery(id+"F12.opExtrude","SWEPT_EDGE",EDGE,{"disambiguationData":[OSD([sQuery(id+"F11.wireOp",EDGE,"E103.bottom"),sQuery(id+"F11.wireOp",EDGE,"E103.right")])]});
            var Q2;
            Q2=makeQuery(id+"F12.opExtrude","SWEPT_EDGE",EDGE,{"disambiguationData":[OSD([sQuery(id+"F11.wireOp",EDGE,"E102.top"),sQuery(id+"F11.wireOp",EDGE,"E102.right")])]});
            var Q3;
            Q3=makeQuery(id+"F12.opExtrude","SWEPT_EDGE",EDGE,{"disambiguationData":[OSD([sQuery(id+"F11.wireOp",EDGE,"E102.bottom"),sQuery(id+"F11.wireOp",EDGE,"E102.right")])]});
            var Q4;
            Q4=makeQuery(id+"F12.opExtrude","SWEPT_EDGE",EDGE,{"disambiguationData":[OSD([sQuery(id+"F11.wireOp",EDGE,"E101.top"),sQuery(id+"F11.wireOp",EDGE,"E101.right")])]});
            var Q5;
            Q5=makeQuery(id+"F12.opExtrude","SWEPT_EDGE",EDGE,{"disambiguationData":[OSD([sQuery(id+"F11.wireOp",EDGE,"E101.bottom"),sQuery(id+"F11.wireOp",EDGE,"E101.right")])]});
            var Q6;
            Q6=makeQuery(id+"F12.opExtrude","SWEPT_EDGE",EDGE,{"disambiguationData":[OSD([sQuery(id+"F11.wireOp",EDGE,"E104.3.3"),sQuery(id+"F11.wireOp",EDGE,"E104.3.9")])]});
            var Q7;
            Q7=makeQuery(id+"F12.opExtrude","SWEPT_EDGE",EDGE,{"disambiguationData":[OSD([sQuery(id+"F11.wireOp",EDGE,"E104.3.3"),sQuery(id+"F11.wireOp",EDGE,"E104.3.10")])]});
            var Q8;
            Q8=makeQuery(id+"F12.opExtrude","SWEPT_EDGE",EDGE,{"disambiguationData":[OSD([sQuery(id+"F11.wireOp",EDGE,"E104.3.0"),sQuery(id+"F11.wireOp",EDGE,"E104.3.6")])]});
            var Q9;
            Q9=makeQuery(id+"F12.opExtrude","SWEPT_EDGE",EDGE,{"disambiguationData":[OSD([sQuery(id+"F11.wireOp",EDGE,"E104.3.0"),sQuery(id+"F11.wireOp",EDGE,"E104.3.11")])]});
            var Q10;
            Q10=makeQuery(id+"F12.opExtrude","SWEPT_EDGE",EDGE,{"disambiguationData":[OSD([sQuery(id+"F11.wireOp",EDGE,"E104.3.4"),sQuery(id+"F11.wireOp",EDGE,"E104.3.7")])]});
            var Q11;
            Q11=makeQuery(id+"F12.opExtrude","SWEPT_EDGE",EDGE,{"disambiguationData":[OSD([sQuery(id+"F11.wireOp",EDGE,"E104.3.4"),sQuery(id+"F11.wireOp",EDGE,"E104.3.8")])]});
            var Q12;
            Q12=makeQuery(id+"F12.opExtrude","SWEPT_EDGE",EDGE,{"disambiguationData":[OSD([sQuery(id+"F11.wireOp",EDGE,"E104.2.3"),sQuery(id+"F11.wireOp",EDGE,"E104.2.9")])]});
            var Q13;
            Q13=makeQuery(id+"F12.opExtrude","SWEPT_EDGE",EDGE,{"disambiguationData":[OSD([sQuery(id+"F11.wireOp",EDGE,"E104.2.3"),sQuery(id+"F11.wireOp",EDGE,"E104.2.10")])]});
            var Q14;
            Q14=makeQuery(id+"F12.opExtrude","SWEPT_EDGE",EDGE,{"disambiguationData":[OSD([sQuery(id+"F11.wireOp",EDGE,"E104.2.0"),sQuery(id+"F11.wireOp",EDGE,"E104.2.6")])]});
            var Q15;
            Q15=makeQuery(id+"F12.opExtrude","SWEPT_EDGE",EDGE,{"disambiguationData":[OSD([sQuery(id+"F11.wireOp",EDGE,"E104.2.0"),sQuery(id+"F11.wireOp",EDGE,"E104.2.11")])]});
            var Q16;
            Q16=makeQuery(id+"F12.opExtrude","SWEPT_EDGE",EDGE,{"disambiguationData":[OSD([sQuery(id+"F11.wireOp",EDGE,"E104.2.4"),sQuery(id+"F11.wireOp",EDGE,"E104.2.8")])]});
            var Q17;
            Q17=makeQuery(id+"F12.opExtrude","SWEPT_EDGE",EDGE,{"disambiguationData":[OSD([sQuery(id+"F11.wireOp",EDGE,"E104.2.4"),sQuery(id+"F11.wireOp",EDGE,"E104.2.7")])]});
            var Q18;
            Q18=makeQuery(id+"F12.opExtrude","SWEPT_EDGE",EDGE,{"disambiguationData":[OSD([sQuery(id+"F11.wireOp",EDGE,"E104.1.3"),sQuery(id+"F11.wireOp",EDGE,"E104.1.10")])]});
            var Q19;
            Q19=makeQuery(id+"F12.opExtrude","SWEPT_EDGE",EDGE,{"disambiguationData":[OSD([sQuery(id+"F11.wireOp",EDGE,"E104.1.3"),sQuery(id+"F11.wireOp",EDGE,"E104.1.9")])]});
            var Q20;
            Q20=makeQuery(id+"F12.opExtrude","SWEPT_EDGE",EDGE,{"disambiguationData":[OSD([sQuery(id+"F11.wireOp",EDGE,"E104.1.0"),sQuery(id+"F11.wireOp",EDGE,"E104.1.11")])]});
            var Q21;
            Q21=makeQuery(id+"F12.opExtrude","SWEPT_EDGE",EDGE,{"disambiguationData":[OSD([sQuery(id+"F11.wireOp",EDGE,"E104.1.0"),sQuery(id+"F11.wireOp",EDGE,"E104.1.6")])]});
            var Q22;
            Q22=makeQuery(id+"F12.opExtrude","SWEPT_EDGE",EDGE,{"disambiguationData":[OSD([sQuery(id+"F11.wireOp",EDGE,"E104.1.4"),sQuery(id+"F11.wireOp",EDGE,"E104.1.8")])]});
            var Q23;
            Q23=makeQuery(id+"F12.opExtrude","SWEPT_EDGE",EDGE,{"disambiguationData":[OSD([sQuery(id+"F11.wireOp",EDGE,"E104.1.4"),sQuery(id+"F11.wireOp",EDGE,"E104.1.7")])]});
            fillet(context, id + "F14", {"entities" : qUnion([Q0, Q1, Q2, Q3, Q4, Q5, Q6, Q7, Q8, Q9, Q10, Q11, Q12, Q13, Q14, Q15, Q16, Q17, Q18, Q19, Q20, Q21, Q22, Q23]), "radius" : .4 * mm, "tangentPropagation" : true, "allowEdgeOverflow" : false});
        }
        {
            var Q0;
            Q0 = qSketchRegion(id + "F10", true);
            extrude(context, id + "F15", {"entities" : qUnion([Q0]), "oppositeDirection" : true, "depth" : .6 * mm, "offsetDistance" : 25 * mm});
        }
        {
            var Q0;
            Q0=makeQuery(id+"F15.opExtrude","SWEPT_BODY",BODY,{"disambiguationData":[OSD([sQuery(id+"F10.wireOp",EDGE,"E66.bottom"),sQuery(id+"F10.wireOp",EDGE,"E66.top"),sQuery(id+"F10.wireOp",EDGE,"E66.right"),sQuery(id+"F10.wireOp",EDGE,"E67.0.1.1"),sQuery(id+"F10.wireOp",EDGE,"E67.0.1.2"),sQuery(id+"F10.wireOp",EDGE,"E67.0.1.3"),sQuery(id+"F10.wireOp",EDGE,"E67.0.2.1"),sQuery(id+"F10.wireOp",EDGE,"E67.0.2.2"),sQuery(id+"F10.wireOp",EDGE,"E67.0.2.3"),sQuery(id+"F10.wireOp",EDGE,"E67.0.3.1"),sQuery(id+"F10.wireOp",EDGE,"E67.0.3.2"),sQuery(id+"F10.wireOp",EDGE,"E67.0.3.3"),sQuery(id+"F10.wireOp",EDGE,"E67.0.4.1"),sQuery(id+"F10.wireOp",EDGE,"E67.0.4.2"),sQuery(id+"F10.wireOp",EDGE,"E67.0.4.3"),sQuery(id+"F10.wireOp",EDGE,"f8f007aa-b1cc-4542-abcf-356018b7fdd71.MirrorCS"),sQuery(id+"F10.wireOp",EDGE,"E71.MirrorCS"),sQuery(id+"F10.wireOp",EDGE,"f8f007aa-b1cc-4542-abcf-356018b7fdd76.MirrorCS"),sQuery(id+"F10.wireOp",EDGE,"E72.MirrorCS"),sQuery(id+"F10.wireOp",EDGE,"f8f007aa-b1cc-4542-abcf-356018b7fdd78.MirrorCS"),sQuery(id+"F10.wireOp",EDGE,"E73.MirrorCS"),sQuery(id+"F10.wireOp",EDGE,"E75.MirrorCS"),sQuery(id+"F10.wireOp",EDGE,"f8f007aa-b1cc-4542-abcf-356018b7fdd712.MirrorCS"),sQuery(id+"F10.wireOp",EDGE,"f8f007aa-b1cc-4542-abcf-356018b7fdd713.MirrorCS"),sQuery(id+"F10.wireOp",EDGE,"E76.MirrorCS"),sQuery(id+"F10.wireOp",EDGE,"E77.MirrorCS"),sQuery(id+"F10.wireOp",EDGE,"E78.MirrorCS"),sQuery(id+"F10.wireOp",EDGE,"f8f007aa-b1cc-4542-abcf-356018b7fdd718.MirrorCS"),sQuery(id+"F10.wireOp",EDGE,"f8f007aa-b1cc-4542-abcf-356018b7fdd719.MirrorCS"),sQuery(id+"F10.wireOp",EDGE,"E690.MirrorCS"),sQuery(id+"F10.wireOp",EDGE,"E79.bottom"),sQuery(id+"F10.wireOp",EDGE,"E79.top"),sQuery(id+"F10.wireOp",EDGE,"E79.left"),sQuery(id+"F10.wireOp",EDGE,"E80.0.1.0"),sQuery(id+"F10.wireOp",EDGE,"E80.0.1.1"),sQuery(id+"F10.wireOp",EDGE,"E80.0.1.2"),sQuery(id+"F10.wireOp",EDGE,"E80.0.2.0"),sQuery(id+"F10.wireOp",EDGE,"E80.0.2.1"),sQuery(id+"F10.wireOp",EDGE,"E80.0.2.2"),sQuery(id+"F10.wireOp",EDGE,"E82.MirrorCS"),sQuery(id+"F10.wireOp",EDGE,"E83.MirrorCS"),sQuery(id+"F10.wireOp",EDGE,"E86.MirrorCS"),sQuery(id+"F10.wireOp",EDGE,"E87.MirrorCS"),sQuery(id+"F10.wireOp",EDGE,"E88.MirrorCS"),sQuery(id+"F10.wireOp",EDGE,"E90.MirrorCS"),sQuery(id+"F10.wireOp",EDGE,"E91.MirrorCS"),sQuery(id+"F10.wireOp",EDGE,"E92.MirrorCS"),sQuery(id+"F10.wireOp",EDGE,"E93.MirrorCS"),sQuery(id+"F10.wireOp",EDGE,"E95.bottom"),sQuery(id+"F10.wireOp",EDGE,"E95.top"),sQuery(id+"F10.wireOp",EDGE,"E95.left"),sQuery(id+"F10.wireOp",EDGE,"E95.right"),sQuery(id+"F10.wireOp",EDGE,"E96")])]});
            var Q1;
            Q1=sQuery(id+"F5.wireOp",EDGE,"E49");
            circularPattern(context, id + "F16", {"entities" : qUnion([Q0]), "axis" : qUnion([Q1]), "angle" : 360 * degree, "instanceCount" : 4, "equalSpace" : true});
        }
        {
            var Q0;
            Q0=makeQuery(id+"F15.opExtrude","SWEPT_BODY",BODY,{"disambiguationData":[OSD([sQuery(id+"F10.wireOp",EDGE,"E66.bottom"),sQuery(id+"F10.wireOp",EDGE,"E66.top"),sQuery(id+"F10.wireOp",EDGE,"E66.right"),sQuery(id+"F10.wireOp",EDGE,"E67.0.1.1"),sQuery(id+"F10.wireOp",EDGE,"E67.0.1.2"),sQuery(id+"F10.wireOp",EDGE,"E67.0.1.3"),sQuery(id+"F10.wireOp",EDGE,"E67.0.2.1"),sQuery(id+"F10.wireOp",EDGE,"E67.0.2.2"),sQuery(id+"F10.wireOp",EDGE,"E67.0.2.3"),sQuery(id+"F10.wireOp",EDGE,"E67.0.3.1"),sQuery(id+"F10.wireOp",EDGE,"E67.0.3.2"),sQuery(id+"F10.wireOp",EDGE,"E67.0.3.3"),sQuery(id+"F10.wireOp",EDGE,"E67.0.4.1"),sQuery(id+"F10.wireOp",EDGE,"E67.0.4.2"),sQuery(id+"F10.wireOp",EDGE,"E67.0.4.3"),sQuery(id+"F10.wireOp",EDGE,"f8f007aa-b1cc-4542-abcf-356018b7fdd71.MirrorCS"),sQuery(id+"F10.wireOp",EDGE,"E71.MirrorCS"),sQuery(id+"F10.wireOp",EDGE,"f8f007aa-b1cc-4542-abcf-356018b7fdd76.MirrorCS"),sQuery(id+"F10.wireOp",EDGE,"E72.MirrorCS"),sQuery(id+"F10.wireOp",EDGE,"f8f007aa-b1cc-4542-abcf-356018b7fdd78.MirrorCS"),sQuery(id+"F10.wireOp",EDGE,"E73.MirrorCS"),sQuery(id+"F10.wireOp",EDGE,"E75.MirrorCS"),sQuery(id+"F10.wireOp",EDGE,"f8f007aa-b1cc-4542-abcf-356018b7fdd712.MirrorCS"),sQuery(id+"F10.wireOp",EDGE,"f8f007aa-b1cc-4542-abcf-356018b7fdd713.MirrorCS"),sQuery(id+"F10.wireOp",EDGE,"E76.MirrorCS"),sQuery(id+"F10.wireOp",EDGE,"E77.MirrorCS"),sQuery(id+"F10.wireOp",EDGE,"E78.MirrorCS"),sQuery(id+"F10.wireOp",EDGE,"f8f007aa-b1cc-4542-abcf-356018b7fdd718.MirrorCS"),sQuery(id+"F10.wireOp",EDGE,"f8f007aa-b1cc-4542-abcf-356018b7fdd719.MirrorCS"),sQuery(id+"F10.wireOp",EDGE,"E690.MirrorCS"),sQuery(id+"F10.wireOp",EDGE,"E79.bottom"),sQuery(id+"F10.wireOp",EDGE,"E79.top"),sQuery(id+"F10.wireOp",EDGE,"E79.left"),sQuery(id+"F10.wireOp",EDGE,"E80.0.1.0"),sQuery(id+"F10.wireOp",EDGE,"E80.0.1.1"),sQuery(id+"F10.wireOp",EDGE,"E80.0.1.2"),sQuery(id+"F10.wireOp",EDGE,"E80.0.2.0"),sQuery(id+"F10.wireOp",EDGE,"E80.0.2.1"),sQuery(id+"F10.wireOp",EDGE,"E80.0.2.2"),sQuery(id+"F10.wireOp",EDGE,"E82.MirrorCS"),sQuery(id+"F10.wireOp",EDGE,"E83.MirrorCS"),sQuery(id+"F10.wireOp",EDGE,"E86.MirrorCS"),sQuery(id+"F10.wireOp",EDGE,"E87.MirrorCS"),sQuery(id+"F10.wireOp",EDGE,"E88.MirrorCS"),sQuery(id+"F10.wireOp",EDGE,"E90.MirrorCS"),sQuery(id+"F10.wireOp",EDGE,"E91.MirrorCS"),sQuery(id+"F10.wireOp",EDGE,"E92.MirrorCS"),sQuery(id+"F10.wireOp",EDGE,"E93.MirrorCS"),sQuery(id+"F10.wireOp",EDGE,"E95.bottom"),sQuery(id+"F10.wireOp",EDGE,"E95.top"),sQuery(id+"F10.wireOp",EDGE,"E95.left"),sQuery(id+"F10.wireOp",EDGE,"E95.right"),sQuery(id+"F10.wireOp",EDGE,"E96")])]});
            var Q1;
            Q1=makeQuery(id+"F16.opPattern","COPY",BODY,{"derivedFrom":makeQuery(id+"F15.opExtrude","SWEPT_BODY",BODY,{"disambiguationData":[OSD([sQuery(id+"F10.wireOp",EDGE,"E66.bottom"),sQuery(id+"F10.wireOp",EDGE,"E66.top"),sQuery(id+"F10.wireOp",EDGE,"E66.right"),sQuery(id+"F10.wireOp",EDGE,"E67.0.1.1"),sQuery(id+"F10.wireOp",EDGE,"E67.0.1.2"),sQuery(id+"F10.wireOp",EDGE,"E67.0.1.3"),sQuery(id+"F10.wireOp",EDGE,"E67.0.2.1"),sQuery(id+"F10.wireOp",EDGE,"E67.0.2.2"),sQuery(id+"F10.wireOp",EDGE,"E67.0.2.3"),sQuery(id+"F10.wireOp",EDGE,"E67.0.3.1"),sQuery(id+"F10.wireOp",EDGE,"E67.0.3.2"),sQuery(id+"F10.wireOp",EDGE,"E67.0.3.3"),sQuery(id+"F10.wireOp",EDGE,"E67.0.4.1"),sQuery(id+"F10.wireOp",EDGE,"E67.0.4.2"),sQuery(id+"F10.wireOp",EDGE,"E67.0.4.3"),sQuery(id+"F10.wireOp",EDGE,"f8f007aa-b1cc-4542-abcf-356018b7fdd71.MirrorCS"),sQuery(id+"F10.wireOp",EDGE,"E71.MirrorCS"),sQuery(id+"F10.wireOp",EDGE,"f8f007aa-b1cc-4542-abcf-356018b7fdd76.MirrorCS"),sQuery(id+"F10.wireOp",EDGE,"E72.MirrorCS"),sQuery(id+"F10.wireOp",EDGE,"f8f007aa-b1cc-4542-abcf-356018b7fdd78.MirrorCS"),sQuery(id+"F10.wireOp",EDGE,"E73.MirrorCS"),sQuery(id+"F10.wireOp",EDGE,"E75.MirrorCS"),sQuery(id+"F10.wireOp",EDGE,"f8f007aa-b1cc-4542-abcf-356018b7fdd712.MirrorCS"),sQuery(id+"F10.wireOp",EDGE,"f8f007aa-b1cc-4542-abcf-356018b7fdd713.MirrorCS"),sQuery(id+"F10.wireOp",EDGE,"E76.MirrorCS"),sQuery(id+"F10.wireOp",EDGE,"E77.MirrorCS"),sQuery(id+"F10.wireOp",EDGE,"E78.MirrorCS"),sQuery(id+"F10.wireOp",EDGE,"f8f007aa-b1cc-4542-abcf-356018b7fdd718.MirrorCS"),sQuery(id+"F10.wireOp",EDGE,"f8f007aa-b1cc-4542-abcf-356018b7fdd719.MirrorCS"),sQuery(id+"F10.wireOp",EDGE,"E690.MirrorCS"),sQuery(id+"F10.wireOp",EDGE,"E79.bottom"),sQuery(id+"F10.wireOp",EDGE,"E79.top"),sQuery(id+"F10.wireOp",EDGE,"E79.left"),sQuery(id+"F10.wireOp",EDGE,"E80.0.1.0"),sQuery(id+"F10.wireOp",EDGE,"E80.0.1.1"),sQuery(id+"F10.wireOp",EDGE,"E80.0.1.2"),sQuery(id+"F10.wireOp",EDGE,"E80.0.2.0"),sQuery(id+"F10.wireOp",EDGE,"E80.0.2.1"),sQuery(id+"F10.wireOp",EDGE,"E80.0.2.2"),sQuery(id+"F10.wireOp",EDGE,"E82.MirrorCS"),sQuery(id+"F10.wireOp",EDGE,"E83.MirrorCS"),sQuery(id+"F10.wireOp",EDGE,"E86.MirrorCS"),sQuery(id+"F10.wireOp",EDGE,"E87.MirrorCS"),sQuery(id+"F10.wireOp",EDGE,"E88.MirrorCS"),sQuery(id+"F10.wireOp",EDGE,"E90.MirrorCS"),sQuery(id+"F10.wireOp",EDGE,"E91.MirrorCS"),sQuery(id+"F10.wireOp",EDGE,"E92.MirrorCS"),sQuery(id+"F10.wireOp",EDGE,"E93.MirrorCS"),sQuery(id+"F10.wireOp",EDGE,"E95.bottom"),sQuery(id+"F10.wireOp",EDGE,"E95.top"),sQuery(id+"F10.wireOp",EDGE,"E95.left"),sQuery(id+"F10.wireOp",EDGE,"E95.right"),sQuery(id+"F10.wireOp",EDGE,"E96")])]}),"instanceName":"1"});
            var Q2;
            Q2=makeQuery(id+"F16.opPattern","COPY",BODY,{"derivedFrom":makeQuery(id+"F15.opExtrude","SWEPT_BODY",BODY,{"disambiguationData":[OSD([sQuery(id+"F10.wireOp",EDGE,"E66.bottom"),sQuery(id+"F10.wireOp",EDGE,"E66.top"),sQuery(id+"F10.wireOp",EDGE,"E66.right"),sQuery(id+"F10.wireOp",EDGE,"E67.0.1.1"),sQuery(id+"F10.wireOp",EDGE,"E67.0.1.2"),sQuery(id+"F10.wireOp",EDGE,"E67.0.1.3"),sQuery(id+"F10.wireOp",EDGE,"E67.0.2.1"),sQuery(id+"F10.wireOp",EDGE,"E67.0.2.2"),sQuery(id+"F10.wireOp",EDGE,"E67.0.2.3"),sQuery(id+"F10.wireOp",EDGE,"E67.0.3.1"),sQuery(id+"F10.wireOp",EDGE,"E67.0.3.2"),sQuery(id+"F10.wireOp",EDGE,"E67.0.3.3"),sQuery(id+"F10.wireOp",EDGE,"E67.0.4.1"),sQuery(id+"F10.wireOp",EDGE,"E67.0.4.2"),sQuery(id+"F10.wireOp",EDGE,"E67.0.4.3"),sQuery(id+"F10.wireOp",EDGE,"f8f007aa-b1cc-4542-abcf-356018b7fdd71.MirrorCS"),sQuery(id+"F10.wireOp",EDGE,"E71.MirrorCS"),sQuery(id+"F10.wireOp",EDGE,"f8f007aa-b1cc-4542-abcf-356018b7fdd76.MirrorCS"),sQuery(id+"F10.wireOp",EDGE,"E72.MirrorCS"),sQuery(id+"F10.wireOp",EDGE,"f8f007aa-b1cc-4542-abcf-356018b7fdd78.MirrorCS"),sQuery(id+"F10.wireOp",EDGE,"E73.MirrorCS"),sQuery(id+"F10.wireOp",EDGE,"E75.MirrorCS"),sQuery(id+"F10.wireOp",EDGE,"f8f007aa-b1cc-4542-abcf-356018b7fdd712.MirrorCS"),sQuery(id+"F10.wireOp",EDGE,"f8f007aa-b1cc-4542-abcf-356018b7fdd713.MirrorCS"),sQuery(id+"F10.wireOp",EDGE,"E76.MirrorCS"),sQuery(id+"F10.wireOp",EDGE,"E77.MirrorCS"),sQuery(id+"F10.wireOp",EDGE,"E78.MirrorCS"),sQuery(id+"F10.wireOp",EDGE,"f8f007aa-b1cc-4542-abcf-356018b7fdd718.MirrorCS"),sQuery(id+"F10.wireOp",EDGE,"f8f007aa-b1cc-4542-abcf-356018b7fdd719.MirrorCS"),sQuery(id+"F10.wireOp",EDGE,"E690.MirrorCS"),sQuery(id+"F10.wireOp",EDGE,"E79.bottom"),sQuery(id+"F10.wireOp",EDGE,"E79.top"),sQuery(id+"F10.wireOp",EDGE,"E79.left"),sQuery(id+"F10.wireOp",EDGE,"E80.0.1.0"),sQuery(id+"F10.wireOp",EDGE,"E80.0.1.1"),sQuery(id+"F10.wireOp",EDGE,"E80.0.1.2"),sQuery(id+"F10.wireOp",EDGE,"E80.0.2.0"),sQuery(id+"F10.wireOp",EDGE,"E80.0.2.1"),sQuery(id+"F10.wireOp",EDGE,"E80.0.2.2"),sQuery(id+"F10.wireOp",EDGE,"E82.MirrorCS"),sQuery(id+"F10.wireOp",EDGE,"E83.MirrorCS"),sQuery(id+"F10.wireOp",EDGE,"E86.MirrorCS"),sQuery(id+"F10.wireOp",EDGE,"E87.MirrorCS"),sQuery(id+"F10.wireOp",EDGE,"E88.MirrorCS"),sQuery(id+"F10.wireOp",EDGE,"E90.MirrorCS"),sQuery(id+"F10.wireOp",EDGE,"E91.MirrorCS"),sQuery(id+"F10.wireOp",EDGE,"E92.MirrorCS"),sQuery(id+"F10.wireOp",EDGE,"E93.MirrorCS"),sQuery(id+"F10.wireOp",EDGE,"E95.bottom"),sQuery(id+"F10.wireOp",EDGE,"E95.top"),sQuery(id+"F10.wireOp",EDGE,"E95.left"),sQuery(id+"F10.wireOp",EDGE,"E95.right"),sQuery(id+"F10.wireOp",EDGE,"E96")])]}),"instanceName":"3"});
            var Q3;
            Q3=makeQuery(id+"F16.opPattern","COPY",BODY,{"derivedFrom":makeQuery(id+"F15.opExtrude","SWEPT_BODY",BODY,{"disambiguationData":[OSD([sQuery(id+"F10.wireOp",EDGE,"E66.bottom"),sQuery(id+"F10.wireOp",EDGE,"E66.top"),sQuery(id+"F10.wireOp",EDGE,"E66.right"),sQuery(id+"F10.wireOp",EDGE,"E67.0.1.1"),sQuery(id+"F10.wireOp",EDGE,"E67.0.1.2"),sQuery(id+"F10.wireOp",EDGE,"E67.0.1.3"),sQuery(id+"F10.wireOp",EDGE,"E67.0.2.1"),sQuery(id+"F10.wireOp",EDGE,"E67.0.2.2"),sQuery(id+"F10.wireOp",EDGE,"E67.0.2.3"),sQuery(id+"F10.wireOp",EDGE,"E67.0.3.1"),sQuery(id+"F10.wireOp",EDGE,"E67.0.3.2"),sQuery(id+"F10.wireOp",EDGE,"E67.0.3.3"),sQuery(id+"F10.wireOp",EDGE,"E67.0.4.1"),sQuery(id+"F10.wireOp",EDGE,"E67.0.4.2"),sQuery(id+"F10.wireOp",EDGE,"E67.0.4.3"),sQuery(id+"F10.wireOp",EDGE,"f8f007aa-b1cc-4542-abcf-356018b7fdd71.MirrorCS"),sQuery(id+"F10.wireOp",EDGE,"E71.MirrorCS"),sQuery(id+"F10.wireOp",EDGE,"f8f007aa-b1cc-4542-abcf-356018b7fdd76.MirrorCS"),sQuery(id+"F10.wireOp",EDGE,"E72.MirrorCS"),sQuery(id+"F10.wireOp",EDGE,"f8f007aa-b1cc-4542-abcf-356018b7fdd78.MirrorCS"),sQuery(id+"F10.wireOp",EDGE,"E73.MirrorCS"),sQuery(id+"F10.wireOp",EDGE,"E75.MirrorCS"),sQuery(id+"F10.wireOp",EDGE,"f8f007aa-b1cc-4542-abcf-356018b7fdd712.MirrorCS"),sQuery(id+"F10.wireOp",EDGE,"f8f007aa-b1cc-4542-abcf-356018b7fdd713.MirrorCS"),sQuery(id+"F10.wireOp",EDGE,"E76.MirrorCS"),sQuery(id+"F10.wireOp",EDGE,"E77.MirrorCS"),sQuery(id+"F10.wireOp",EDGE,"E78.MirrorCS"),sQuery(id+"F10.wireOp",EDGE,"f8f007aa-b1cc-4542-abcf-356018b7fdd718.MirrorCS"),sQuery(id+"F10.wireOp",EDGE,"f8f007aa-b1cc-4542-abcf-356018b7fdd719.MirrorCS"),sQuery(id+"F10.wireOp",EDGE,"E690.MirrorCS"),sQuery(id+"F10.wireOp",EDGE,"E79.bottom"),sQuery(id+"F10.wireOp",EDGE,"E79.top"),sQuery(id+"F10.wireOp",EDGE,"E79.left"),sQuery(id+"F10.wireOp",EDGE,"E80.0.1.0"),sQuery(id+"F10.wireOp",EDGE,"E80.0.1.1"),sQuery(id+"F10.wireOp",EDGE,"E80.0.1.2"),sQuery(id+"F10.wireOp",EDGE,"E80.0.2.0"),sQuery(id+"F10.wireOp",EDGE,"E80.0.2.1"),sQuery(id+"F10.wireOp",EDGE,"E80.0.2.2"),sQuery(id+"F10.wireOp",EDGE,"E82.MirrorCS"),sQuery(id+"F10.wireOp",EDGE,"E83.MirrorCS"),sQuery(id+"F10.wireOp",EDGE,"E86.MirrorCS"),sQuery(id+"F10.wireOp",EDGE,"E87.MirrorCS"),sQuery(id+"F10.wireOp",EDGE,"E88.MirrorCS"),sQuery(id+"F10.wireOp",EDGE,"E90.MirrorCS"),sQuery(id+"F10.wireOp",EDGE,"E91.MirrorCS"),sQuery(id+"F10.wireOp",EDGE,"E92.MirrorCS"),sQuery(id+"F10.wireOp",EDGE,"E93.MirrorCS"),sQuery(id+"F10.wireOp",EDGE,"E95.bottom"),sQuery(id+"F10.wireOp",EDGE,"E95.top"),sQuery(id+"F10.wireOp",EDGE,"E95.left"),sQuery(id+"F10.wireOp",EDGE,"E95.right"),sQuery(id+"F10.wireOp",EDGE,"E96")])]}),"instanceName":"2"});
            booleanBodies(context, id + "F17", {"operationType" : BooleanOperationType.UNION, "tools" : qUnion([Q0, Q1, Q2, Q3])});
        }
        {
            var Q0;
            Q0=qCreatedBy(makeId("Top.planeOp"),FACE);
            var sketch = newSketch(context, id + "F18", { "sketchPlane" : qUnion([Q0])});
            skLineSegment(sketch, "E105.bottom", {"start": v(-18.6, -10) * mm, "end": v(-19.4, -10) * mm});
            skLineSegment(sketch, "E105.top", {"start": v(-18.6, 10) * mm, "end": v(-19.4, 10) * mm});
            skLineSegment(sketch, "E105.left", {"start": v(-18.6, -10) * mm, "end": v(-18.6, 10) * mm});
            skLineSegment(sketch, "E105.right", {"start": v(-19.4, -10) * mm, "end": v(-19.4, 10) * mm});
            skLineSegment(sketch, "E106.1.0.0", {"start": v(-22.9, -10) * mm, "end": v(-22.9, 10) * mm});
            skLineSegment(sketch, "E106.1.0.1", {"start": v(-23.7, -10) * mm, "end": v(-23.7, 10) * mm});
            skLineSegment(sketch, "E106.1.0.2", {"start": v(-22.9, -10) * mm, "end": v(-23.7, -10) * mm});
            skLineSegment(sketch, "E106.1.0.3", {"start": v(-22.9, 10) * mm, "end": v(-23.7, 10) * mm});
            skLineSegment(sketch, "E106.2.0.0", {"start": v(-27.2, -10) * mm, "end": v(-27.2, 10) * mm});
            skLineSegment(sketch, "E106.2.0.1", {"start": v(-28, -10) * mm, "end": v(-28, 10) * mm});
            skLineSegment(sketch, "E106.2.0.2", {"start": v(-27.2, -10) * mm, "end": v(-28, -10) * mm});
            skLineSegment(sketch, "E106.2.0.3", {"start": v(-27.2, 10) * mm, "end": v(-28, 10) * mm});
            skLineSegment(sketch, "E106.3.0.0", {"start": v(-31.5, -10) * mm, "end": v(-31.5, 10) * mm});
            skLineSegment(sketch, "E106.3.0.1", {"start": v(-32.3, -10) * mm, "end": v(-32.3, 10) * mm});
            skLineSegment(sketch, "E106.3.0.2", {"start": v(-31.5, -10) * mm, "end": v(-32.3, -10) * mm});
            skLineSegment(sketch, "E106.3.0.3", {"start": v(-31.5, 10) * mm, "end": v(-32.3, 10) * mm});
            skLineSegment(sketch, "E106.direction1", {"start": v(-19.4, -10) * mm, "end": v(-23.7, -10) * mm, "construction": true});
            skLineSegment(sketch, "E107", {"start": v(-37, -11.33) * mm, "end": v(-37, 10.9) * mm, "construction": true});
            skLineSegment(sketch, "E108.MirrorCS", {"start": v(-55.4, -10) * mm, "end": v(-54.6, -10) * mm});
            skLineSegment(sketch, "E109.MirrorCS", {"start": v(-46.8, 10) * mm, "end": v(-46, 10) * mm});
            skLineSegment(sketch, "E110.MirrorCS", {"start": v(-46.8, -10) * mm, "end": v(-46, -10) * mm});
            skLineSegment(sketch, "E111.MirrorCS", {"start": v(-51.1, 10) * mm, "end": v(-50.3, 10) * mm});
            skLineSegment(sketch, "E112.MirrorCS", {"start": v(-51.1, -10) * mm, "end": v(-50.3, -10) * mm});
            skLineSegment(sketch, "E113.MirrorCS", {"start": v(-55.4, 10) * mm, "end": v(-54.6, 10) * mm});
            skLineSegment(sketch, "E114.MirrorCS", {"start": v(-42.5, 10) * mm, "end": v(-41.7, 10) * mm});
            skLineSegment(sketch, "E115.MirrorCS", {"start": v(-42.5, -10) * mm, "end": v(-41.7, -10) * mm});
            skLineSegment(sketch, "E116.MirrorCS", {"start": v(-42.5, -10) * mm, "end": v(-42.5, 10) * mm});
            skLineSegment(sketch, "E117.MirrorCS", {"start": v(-46, -10) * mm, "end": v(-46, 10) * mm});
            skLineSegment(sketch, "E118.MirrorCS", {"start": v(-46.8, -10) * mm, "end": v(-46.8, 10) * mm});
            skLineSegment(sketch, "E119.MirrorCS", {"start": v(-50.3, -10) * mm, "end": v(-50.3, 10) * mm});
            skLineSegment(sketch, "E120.MirrorCS", {"start": v(-51.1, -10) * mm, "end": v(-51.1, 10) * mm});
            skLineSegment(sketch, "E121.MirrorCS", {"start": v(-54.6, -10) * mm, "end": v(-54.6, 10) * mm});
            skLineSegment(sketch, "E122.MirrorCS", {"start": v(-55.4, -10) * mm, "end": v(-55.4, 10) * mm});
            skLineSegment(sketch, "E123.MirrorCS", {"start": v(-54.6, -10) * mm, "end": v(-50.3, -10) * mm, "construction": true});
            skLineSegment(sketch, "E124.MirrorCS", {"start": v(-41.7, -10) * mm, "end": v(-41.7, 10) * mm});
            skLineSegment(sketch, "E125.bottom", {"start": v(-55.4, -10) * mm, "end": v(-13, -10) * mm});
            skLineSegment(sketch, "E125.top", {"start": v(-55.4, -12) * mm, "end": v(-13, -12) * mm});
            skLineSegment(sketch, "E125.left", {"start": v(-55.4, -10) * mm, "end": v(-55.4, -12) * mm});
            skLineSegment(sketch, "E125.right", {"start": v(-13, -10) * mm, "end": v(-13, -12) * mm});
            skLineSegment(sketch, "E126.bottom", {"start": v(-13, -12) * mm, "end": v(-14, -12) * mm});
            skLineSegment(sketch, "E126.top", {"start": v(-13, 12) * mm, "end": v(-14, 12) * mm});
            skLineSegment(sketch, "E126.left", {"start": v(-13, -12) * mm, "end": v(-13, 12) * mm});
            skLineSegment(sketch, "E126.right", {"start": v(-14, -12) * mm, "end": v(-14, 12) * mm});
            skSolve(sketch);
        }
        {
            var Q0;
            Q0 = qSketchRegion(id + "F18", true);
            extrude(context, id + "F19", {"entities" : qUnion([Q0]), "depth" : .6 * mm, "offsetDistance" : 25 * mm});
        }
        {
            var Q0;
            Q0=makeQuery(id+"F19.opExtrude","SWEPT_BODY",BODY,{"disambiguationData":[OSD([sQuery(id+"F18.wireOp",EDGE,"E105.top"),sQuery(id+"F18.wireOp",EDGE,"E105.left"),sQuery(id+"F18.wireOp",EDGE,"E105.right"),sQuery(id+"F18.wireOp",EDGE,"E106.1.0.0"),sQuery(id+"F18.wireOp",EDGE,"E106.1.0.1"),sQuery(id+"F18.wireOp",EDGE,"E106.1.0.3"),sQuery(id+"F18.wireOp",EDGE,"E106.2.0.0"),sQuery(id+"F18.wireOp",EDGE,"E106.2.0.1"),sQuery(id+"F18.wireOp",EDGE,"E106.2.0.3"),sQuery(id+"F18.wireOp",EDGE,"E106.3.0.0"),sQuery(id+"F18.wireOp",EDGE,"E106.3.0.1"),sQuery(id+"F18.wireOp",EDGE,"E106.3.0.3"),sQuery(id+"F18.wireOp",EDGE,"E109.MirrorCS"),sQuery(id+"F18.wireOp",EDGE,"E111.MirrorCS"),sQuery(id+"F18.wireOp",EDGE,"E113.MirrorCS"),sQuery(id+"F18.wireOp",EDGE,"E114.MirrorCS"),sQuery(id+"F18.wireOp",EDGE,"E116.MirrorCS"),sQuery(id+"F18.wireOp",EDGE,"E117.MirrorCS"),sQuery(id+"F18.wireOp",EDGE,"E118.MirrorCS"),sQuery(id+"F18.wireOp",EDGE,"E119.MirrorCS"),sQuery(id+"F18.wireOp",EDGE,"E120.MirrorCS"),sQuery(id+"F18.wireOp",EDGE,"E121.MirrorCS"),sQuery(id+"F18.wireOp",EDGE,"E122.MirrorCS"),sQuery(id+"F18.wireOp",EDGE,"E124.MirrorCS"),sQuery(id+"F18.wireOp",EDGE,"E125.bottom"),sQuery(id+"F18.wireOp",EDGE,"E125.top"),sQuery(id+"F18.wireOp",EDGE,"E125.left"),sQuery(id+"F18.wireOp",EDGE,"EhRrtqoq-vNMk-uMcm-uzMD-iH6UDO5MWuUa.bottom"),sQuery(id+"F18.wireOp",EDGE,"EhRrtqoq-vNMk-uMcm-uzMD-iH6UDO5MWuUa.top"),sQuery(id+"F18.wireOp",EDGE,"orvlhdmn-wiKn-TyWR-zfCy-YB2kORi7zM3W.bottom"),sQuery(id+"F18.wireOp",EDGE,"orvlhdmn-wiKn-TyWR-zfCy-YB2kORi7zM3W.top"),sQuery(id+"F18.wireOp",EDGE,"orvlhdmn-wiKn-TyWR-zfCy-YB2kORi7zM3W.left"),sQuery(id+"F18.wireOp",EDGE,"orvlhdmn-wiKn-TyWR-zfCy-YB2kORi7zM3W.right"),sQuery(id+"F18.wireOp",EDGE,"E126.bottom"),sQuery(id+"F18.wireOp",EDGE,"E126.top"),sQuery(id+"F18.wireOp",EDGE,"E126.left"),sQuery(id+"F18.wireOp",EDGE,"E126.right")])]});
            var Q1;
            Q1=sQuery(id+"F5.wireOp",EDGE,"E49");
            circularPattern(context, id + "F20", {"operationType" : NewBodyOperationType.ADD, "entities" : qUnion([Q0]), "axis" : qUnion([Q1]), "angle" : 360 * degree, "instanceCount" : 4, "equalSpace" : true});
        }
        {
            var Q0;
            Q0=makeQuery(id+"F2.opExtrude","SWEPT_BODY",BODY,{"disambiguationData":[OSD([sQuery(id+"F1.wireOp",EDGE,"E6.bottom"),sQuery(id+"F1.wireOp",EDGE,"E6.top"),sQuery(id+"F1.wireOp",EDGE,"E6.left"),sQuery(id+"F1.wireOp",EDGE,"E6.right"),sQuery(id+"F1.wireOp",EDGE,"E7.bottom"),sQuery(id+"F1.wireOp",EDGE,"E7.top"),sQuery(id+"F1.wireOp",EDGE,"E7.left"),sQuery(id+"F1.wireOp",EDGE,"E7.right"),sQuery(id+"F1.wireOp",EDGE,"E8.bottom"),sQuery(id+"F1.wireOp",EDGE,"E8.top"),sQuery(id+"F1.wireOp",EDGE,"E8.left"),sQuery(id+"F1.wireOp",EDGE,"E8.right"),sQuery(id+"F1.wireOp",EDGE,"E9.trimOffspring"),sQuery(id+"F1.wireOp",EDGE,"E10.trimOffspring"),sQuery(id+"F1.wireOp",EDGE,"E11.left"),sQuery(id+"F1.wireOp",EDGE,"E11.right"),sQuery(id+"F1.wireOp",EDGE,"E14.trimOffspring"),sQuery(id+"F1.wireOp",EDGE,"E15.trimOffspring"),sQuery(id+"F1.wireOp",EDGE,"E16"),sQuery(id+"F1.wireOp",EDGE,"E17"),sQuery(id+"F1.wireOp",EDGE,"E18"),sQuery(id+"F1.wireOp",EDGE,"E19"),sQuery(id+"F1.wireOp",EDGE,"E20"),sQuery(id+"F1.wireOp",EDGE,"E25.trimOffspring"),sQuery(id+"F1.wireOp",EDGE,"E26.trimOffspring"),sQuery(id+"F1.wireOp",EDGE,"E27.trimOffspring"),sQuery(id+"F1.wireOp",EDGE,"E28.trimOffspring"),sQuery(id+"F1.wireOp",EDGE,"E29.trimOffspring"),sQuery(id+"F1.wireOp",EDGE,"E30.trimOffspring"),sQuery(id+"F1.wireOp",EDGE,"E31.bottom"),sQuery(id+"F1.wireOp",EDGE,"E31.top"),sQuery(id+"F1.wireOp",EDGE,"E31.left"),sQuery(id+"F1.wireOp",EDGE,"E31.right"),sQuery(id+"F1.wireOp",EDGE,"E32"),sQuery(id+"F1.wireOp",EDGE,"E33"),sQuery(id+"F1.wireOp",EDGE,"E34.trimOffspring"),sQuery(id+"F1.wireOp",EDGE,"E35.trimOffspring"),sQuery(id+"F1.wireOp",EDGE,"E36.trimOffspring")])]});
            var Q1;
            Q1=makeQuery(id+"F4.opExtrude","SWEPT_BODY",BODY,{"disambiguationData":[OSD([sQuery(id+"F3.wireOp",EDGE,"E37.bottom"),sQuery(id+"F3.wireOp",EDGE,"E37.top"),sQuery(id+"F3.wireOp",EDGE,"E37.left"),sQuery(id+"F3.wireOp",EDGE,"E37.right"),sQuery(id+"F3.wireOp",EDGE,"E38.bottom"),sQuery(id+"F3.wireOp",EDGE,"E38.top"),sQuery(id+"F3.wireOp",EDGE,"E38.left"),sQuery(id+"F3.wireOp",EDGE,"E38.right"),sQuery(id+"F3.wireOp",EDGE,"E39.bottom"),sQuery(id+"F3.wireOp",EDGE,"E39.top"),sQuery(id+"F3.wireOp",EDGE,"E40.left"),sQuery(id+"F3.wireOp",EDGE,"E40.right"),sQuery(id+"F3.wireOp",EDGE,"E41.trimOffspring"),sQuery(id+"F3.wireOp",EDGE,"E42.trimOffspring"),sQuery(id+"F3.wireOp",EDGE,"E43.trimOffspring"),sQuery(id+"F3.wireOp",EDGE,"E44.trimOffspring"),sQuery(id+"F3.wireOp",EDGE,"E45.trimOffspring"),sQuery(id+"F3.wireOp",EDGE,"E46.trimOffspring"),sQuery(id+"F3.wireOp",EDGE,"E47.trimOffspring"),sQuery(id+"F3.wireOp",EDGE,"E48.trimOffspring")])]});
            var Q2;
            Q2=makeQuery(id+"F15.opExtrude","SWEPT_BODY",BODY,{"disambiguationData":[OSD([sQuery(id+"F10.wireOp",EDGE,"E66.bottom"),sQuery(id+"F10.wireOp",EDGE,"E66.top"),sQuery(id+"F10.wireOp",EDGE,"E66.right"),sQuery(id+"F10.wireOp",EDGE,"E67.0.1.1"),sQuery(id+"F10.wireOp",EDGE,"E67.0.1.2"),sQuery(id+"F10.wireOp",EDGE,"E67.0.1.3"),sQuery(id+"F10.wireOp",EDGE,"E67.0.2.1"),sQuery(id+"F10.wireOp",EDGE,"E67.0.2.2"),sQuery(id+"F10.wireOp",EDGE,"E67.0.2.3"),sQuery(id+"F10.wireOp",EDGE,"E67.0.3.1"),sQuery(id+"F10.wireOp",EDGE,"E67.0.3.2"),sQuery(id+"F10.wireOp",EDGE,"E67.0.3.3"),sQuery(id+"F10.wireOp",EDGE,"E67.0.4.1"),sQuery(id+"F10.wireOp",EDGE,"E67.0.4.2"),sQuery(id+"F10.wireOp",EDGE,"E67.0.4.3"),sQuery(id+"F10.wireOp",EDGE,"f8f007aa-b1cc-4542-abcf-356018b7fdd71.MirrorCS"),sQuery(id+"F10.wireOp",EDGE,"E71.MirrorCS"),sQuery(id+"F10.wireOp",EDGE,"f8f007aa-b1cc-4542-abcf-356018b7fdd76.MirrorCS"),sQuery(id+"F10.wireOp",EDGE,"E72.MirrorCS"),sQuery(id+"F10.wireOp",EDGE,"f8f007aa-b1cc-4542-abcf-356018b7fdd78.MirrorCS"),sQuery(id+"F10.wireOp",EDGE,"E73.MirrorCS"),sQuery(id+"F10.wireOp",EDGE,"E75.MirrorCS"),sQuery(id+"F10.wireOp",EDGE,"f8f007aa-b1cc-4542-abcf-356018b7fdd712.MirrorCS"),sQuery(id+"F10.wireOp",EDGE,"f8f007aa-b1cc-4542-abcf-356018b7fdd713.MirrorCS"),sQuery(id+"F10.wireOp",EDGE,"E76.MirrorCS"),sQuery(id+"F10.wireOp",EDGE,"E77.MirrorCS"),sQuery(id+"F10.wireOp",EDGE,"E78.MirrorCS"),sQuery(id+"F10.wireOp",EDGE,"f8f007aa-b1cc-4542-abcf-356018b7fdd718.MirrorCS"),sQuery(id+"F10.wireOp",EDGE,"f8f007aa-b1cc-4542-abcf-356018b7fdd719.MirrorCS"),sQuery(id+"F10.wireOp",EDGE,"E690.MirrorCS"),sQuery(id+"F10.wireOp",EDGE,"E79.bottom"),sQuery(id+"F10.wireOp",EDGE,"E79.top"),sQuery(id+"F10.wireOp",EDGE,"E79.left"),sQuery(id+"F10.wireOp",EDGE,"E80.0.1.0"),sQuery(id+"F10.wireOp",EDGE,"E80.0.1.1"),sQuery(id+"F10.wireOp",EDGE,"E80.0.1.2"),sQuery(id+"F10.wireOp",EDGE,"E80.0.2.0"),sQuery(id+"F10.wireOp",EDGE,"E80.0.2.1"),sQuery(id+"F10.wireOp",EDGE,"E80.0.2.2"),sQuery(id+"F10.wireOp",EDGE,"E82.MirrorCS"),sQuery(id+"F10.wireOp",EDGE,"E83.MirrorCS"),sQuery(id+"F10.wireOp",EDGE,"E86.MirrorCS"),sQuery(id+"F10.wireOp",EDGE,"E87.MirrorCS"),sQuery(id+"F10.wireOp",EDGE,"E88.MirrorCS"),sQuery(id+"F10.wireOp",EDGE,"E90.MirrorCS"),sQuery(id+"F10.wireOp",EDGE,"E91.MirrorCS"),sQuery(id+"F10.wireOp",EDGE,"E92.MirrorCS"),sQuery(id+"F10.wireOp",EDGE,"E93.MirrorCS"),sQuery(id+"F10.wireOp",EDGE,"E95.bottom"),sQuery(id+"F10.wireOp",EDGE,"E95.top"),sQuery(id+"F10.wireOp",EDGE,"E95.left"),sQuery(id+"F10.wireOp",EDGE,"E95.right"),sQuery(id+"F10.wireOp",EDGE,"E96")])]});
            booleanBodies(context, id + "F21", {"operationType" : BooleanOperationType.UNION, "tools" : qUnion([Q0, Q1, Q2])});
        }
        {
            var Q0;
            Q0=qCreatedBy(makeId("Top.planeOp"),FACE);
            var sketch = newSketch(context, id + "F22", { "sketchPlane" : qUnion([Q0])});
            skLineSegment(sketch, "E127.bottom", {"start": v(-11.43, -51.38) * mm, "end": v(-12, -51.95) * mm});
            skLineSegment(sketch, "E127.top", {"start": v(-51.38, -11.43) * mm, "end": v(-51.95, -12) * mm});
            skLineSegment(sketch, "E127.left", {"start": v(-11.43, -51.38) * mm, "end": v(-51.38, -11.43) * mm});
            skLineSegment(sketch, "E127.right", {"start": v(-12, -51.95) * mm, "end": v(-51.95, -12) * mm});
            skPoint(sketch, "E127.middle", {"position": v(-31.7, -31.7) * mm});
            skLineSegment(sketch, "E128.bottom", {"start": v(-11.43, -42.9) * mm, "end": v(-12, -43.46) * mm});
            skLineSegment(sketch, "E128.top", {"start": v(-42.9, -11.43) * mm, "end": v(-43.46, -12) * mm});
            skLineSegment(sketch, "E128.left", {"start": v(-11.43, -42.9) * mm, "end": v(-42.9, -11.43) * mm});
            skLineSegment(sketch, "E128.right", {"start": v(-12, -43.46) * mm, "end": v(-43.46, -12) * mm});
            skPoint(sketch, "E128.middle", {"position": v(-27.45, -27.45) * mm});
            skLineSegment(sketch, "E129.bottom", {"start": v(-11.43, -34.41) * mm, "end": v(-12, -34.98) * mm});
            skLineSegment(sketch, "E129.top", {"start": v(-34.41, -11.43) * mm, "end": v(-34.98, -12) * mm});
            skLineSegment(sketch, "E129.left", {"start": v(-11.43, -34.41) * mm, "end": v(-34.41, -11.43) * mm});
            skLineSegment(sketch, "E129.right", {"start": v(-12, -34.98) * mm, "end": v(-34.98, -12) * mm});
            skPoint(sketch, "E129.middle", {"position": v(-23.2, -23.2) * mm});
            skLineSegment(sketch, "E130.bottom", {"start": v(-11.43, -27.34) * mm, "end": v(-12, -27.9) * mm});
            skLineSegment(sketch, "E130.top", {"start": v(-27.34, -11.43) * mm, "end": v(-27.9, -12) * mm});
            skLineSegment(sketch, "E130.left", {"start": v(-11.43, -27.34) * mm, "end": v(-27.34, -11.43) * mm});
            skLineSegment(sketch, "E130.right", {"start": v(-12, -27.9) * mm, "end": v(-27.9, -12) * mm});
            skPoint(sketch, "E130.middle", {"position": v(-19.67, -19.67) * mm});
            skLineSegment(sketch, "E131.bottom", {"start": v(-11.43, -20.27) * mm, "end": v(-12, -20.84) * mm});
            skLineSegment(sketch, "E131.top", {"start": v(-20.27, -11.43) * mm, "end": v(-20.84, -12) * mm});
            skLineSegment(sketch, "E131.left", {"start": v(-11.43, -20.27) * mm, "end": v(-20.27, -11.43) * mm});
            skLineSegment(sketch, "E131.right", {"start": v(-12, -20.84) * mm, "end": v(-20.84, -12) * mm});
            skPoint(sketch, "E131.middle", {"position": v(-16.14, -16.14) * mm});
            skLineSegment(sketch, "E132.1.0", {"start": v(43.46, -12) * mm, "end": v(12, -43.46) * mm});
            skLineSegment(sketch, "E132.1.1", {"start": v(51.95, -12) * mm, "end": v(12, -51.95) * mm});
            skPoint(sketch, "E132.1.2", {"position": v(23.2, -23.2) * mm});
            skLineSegment(sketch, "E132.1.3", {"start": v(20.84, -12) * mm, "end": v(12, -20.84) * mm});
            skLineSegment(sketch, "E132.1.4", {"start": v(51.38, -11.43) * mm, "end": v(11.43, -51.38) * mm});
            skPoint(sketch, "E132.1.5", {"position": v(16.14, -16.14) * mm});
            skLineSegment(sketch, "E132.1.6", {"start": v(34.41, -11.43) * mm, "end": v(11.43, -34.41) * mm});
            skLineSegment(sketch, "E132.1.7", {"start": v(34.98, -12) * mm, "end": v(12, -34.98) * mm});
            skLineSegment(sketch, "E132.1.8", {"start": v(42.9, -11.43) * mm, "end": v(11.43, -42.9) * mm});
            skPoint(sketch, "E132.1.9", {"position": v(27.45, -27.45) * mm});
            skLineSegment(sketch, "E132.1.10", {"start": v(20.27, -11.43) * mm, "end": v(11.43, -20.27) * mm});
            skPoint(sketch, "E132.1.11", {"position": v(19.67, -19.67) * mm});
            skLineSegment(sketch, "E132.1.12", {"start": v(27.9, -12) * mm, "end": v(12, -27.9) * mm});
            skLineSegment(sketch, "E132.1.13", {"start": v(27.34, -11.43) * mm, "end": v(11.43, -27.34) * mm});
            skPoint(sketch, "E132.1.14", {"position": v(31.7, -31.7) * mm});
            skLineSegment(sketch, "E132.1.15", {"start": v(20.27, -11.43) * mm, "end": v(20.84, -12) * mm});
            skLineSegment(sketch, "E132.1.16", {"start": v(11.43, -51.38) * mm, "end": v(12, -51.95) * mm});
            skLineSegment(sketch, "E132.1.17", {"start": v(34.41, -11.43) * mm, "end": v(34.98, -12) * mm});
            skLineSegment(sketch, "E132.1.18", {"start": v(11.43, -34.41) * mm, "end": v(12, -34.98) * mm});
            skLineSegment(sketch, "E132.1.19", {"start": v(27.34, -11.43) * mm, "end": v(27.9, -12) * mm});
            skLineSegment(sketch, "E132.1.20", {"start": v(11.43, -42.9) * mm, "end": v(12, -43.46) * mm});
            skLineSegment(sketch, "E132.1.21", {"start": v(51.38, -11.43) * mm, "end": v(51.95, -12) * mm});
            skLineSegment(sketch, "E132.1.22", {"start": v(11.43, -20.27) * mm, "end": v(12, -20.84) * mm});
            skLineSegment(sketch, "E132.1.23", {"start": v(11.43, -27.34) * mm, "end": v(12, -27.9) * mm});
            skLineSegment(sketch, "E132.1.24", {"start": v(42.9, -11.43) * mm, "end": v(43.46, -12) * mm});
            skLineSegment(sketch, "E132.2.0", {"start": v(12, 43.46) * mm, "end": v(43.46, 12) * mm});
            skLineSegment(sketch, "E132.2.1", {"start": v(12, 51.95) * mm, "end": v(51.95, 12) * mm});
            skPoint(sketch, "E132.2.2", {"position": v(23.2, 23.2) * mm});
            skLineSegment(sketch, "E132.2.3", {"start": v(12, 20.84) * mm, "end": v(20.84, 12) * mm});
            skLineSegment(sketch, "E132.2.4", {"start": v(11.43, 51.38) * mm, "end": v(51.38, 11.43) * mm});
            skPoint(sketch, "E132.2.5", {"position": v(16.14, 16.14) * mm});
            skLineSegment(sketch, "E132.2.6", {"start": v(11.43, 34.41) * mm, "end": v(34.41, 11.43) * mm});
            skLineSegment(sketch, "E132.2.7", {"start": v(12, 34.98) * mm, "end": v(34.98, 12) * mm});
            skLineSegment(sketch, "E132.2.8", {"start": v(11.43, 42.9) * mm, "end": v(42.9, 11.43) * mm});
            skPoint(sketch, "E132.2.9", {"position": v(27.45, 27.45) * mm});
            skLineSegment(sketch, "E132.2.10", {"start": v(11.43, 20.27) * mm, "end": v(20.27, 11.43) * mm});
            skPoint(sketch, "E132.2.11", {"position": v(19.67, 19.67) * mm});
            skLineSegment(sketch, "E132.2.12", {"start": v(12, 27.9) * mm, "end": v(27.9, 12) * mm});
            skLineSegment(sketch, "E132.2.13", {"start": v(11.43, 27.34) * mm, "end": v(27.34, 11.43) * mm});
            skPoint(sketch, "E132.2.14", {"position": v(31.7, 31.7) * mm});
            skLineSegment(sketch, "E132.2.15", {"start": v(11.43, 20.27) * mm, "end": v(12, 20.84) * mm});
            skLineSegment(sketch, "E132.2.16", {"start": v(51.38, 11.43) * mm, "end": v(51.95, 12) * mm});
            skLineSegment(sketch, "E132.2.17", {"start": v(11.43, 34.41) * mm, "end": v(12, 34.98) * mm});
            skLineSegment(sketch, "E132.2.18", {"start": v(34.41, 11.43) * mm, "end": v(34.98, 12) * mm});
            skLineSegment(sketch, "E132.2.19", {"start": v(11.43, 27.34) * mm, "end": v(12, 27.9) * mm});
            skLineSegment(sketch, "E132.2.20", {"start": v(42.9, 11.43) * mm, "end": v(43.46, 12) * mm});
            skLineSegment(sketch, "E132.2.21", {"start": v(11.43, 51.38) * mm, "end": v(12, 51.95) * mm});
            skLineSegment(sketch, "E132.2.22", {"start": v(20.27, 11.43) * mm, "end": v(20.84, 12) * mm});
            skLineSegment(sketch, "E132.2.23", {"start": v(27.34, 11.43) * mm, "end": v(27.9, 12) * mm});
            skLineSegment(sketch, "E132.2.24", {"start": v(11.43, 42.9) * mm, "end": v(12, 43.46) * mm});
            skLineSegment(sketch, "E132.3.0", {"start": v(-43.46, 12) * mm, "end": v(-12, 43.46) * mm});
            skLineSegment(sketch, "E132.3.1", {"start": v(-51.95, 12) * mm, "end": v(-12, 51.95) * mm});
            skPoint(sketch, "E132.3.2", {"position": v(-23.2, 23.2) * mm});
            skLineSegment(sketch, "E132.3.3", {"start": v(-20.84, 12) * mm, "end": v(-12, 20.84) * mm});
            skLineSegment(sketch, "E132.3.4", {"start": v(-51.38, 11.43) * mm, "end": v(-11.43, 51.38) * mm});
            skPoint(sketch, "E132.3.5", {"position": v(-16.14, 16.14) * mm});
            skLineSegment(sketch, "E132.3.6", {"start": v(-34.41, 11.43) * mm, "end": v(-11.43, 34.41) * mm});
            skLineSegment(sketch, "E132.3.7", {"start": v(-34.98, 12) * mm, "end": v(-12, 34.98) * mm});
            skLineSegment(sketch, "E132.3.8", {"start": v(-42.9, 11.43) * mm, "end": v(-11.43, 42.9) * mm});
            skPoint(sketch, "E132.3.9", {"position": v(-27.45, 27.45) * mm});
            skLineSegment(sketch, "E132.3.10", {"start": v(-20.27, 11.43) * mm, "end": v(-11.43, 20.27) * mm});
            skPoint(sketch, "E132.3.11", {"position": v(-19.67, 19.67) * mm});
            skLineSegment(sketch, "E132.3.12", {"start": v(-27.9, 12) * mm, "end": v(-12, 27.9) * mm});
            skLineSegment(sketch, "E132.3.13", {"start": v(-27.34, 11.43) * mm, "end": v(-11.43, 27.34) * mm});
            skPoint(sketch, "E132.3.14", {"position": v(-31.7, 31.7) * mm});
            skLineSegment(sketch, "E132.3.15", {"start": v(-20.27, 11.43) * mm, "end": v(-20.84, 12) * mm});
            skLineSegment(sketch, "E132.3.16", {"start": v(-11.43, 51.38) * mm, "end": v(-12, 51.95) * mm});
            skLineSegment(sketch, "E132.3.17", {"start": v(-34.41, 11.43) * mm, "end": v(-34.98, 12) * mm});
            skLineSegment(sketch, "E132.3.18", {"start": v(-11.43, 34.41) * mm, "end": v(-12, 34.98) * mm});
            skLineSegment(sketch, "E132.3.19", {"start": v(-27.34, 11.43) * mm, "end": v(-27.9, 12) * mm});
            skLineSegment(sketch, "E132.3.20", {"start": v(-11.43, 42.9) * mm, "end": v(-12, 43.46) * mm});
            skLineSegment(sketch, "E132.3.21", {"start": v(-51.38, 11.43) * mm, "end": v(-51.95, 12) * mm});
            skLineSegment(sketch, "E132.3.22", {"start": v(-11.43, 20.27) * mm, "end": v(-12, 20.84) * mm});
            skLineSegment(sketch, "E132.3.23", {"start": v(-11.43, 27.34) * mm, "end": v(-12, 27.9) * mm});
            skLineSegment(sketch, "E132.3.24", {"start": v(-42.9, 11.43) * mm, "end": v(-43.46, 12) * mm});
            skPoint(sketch, "E132.center", {"position": v(0, 0) * mm});
            skSolve(sketch);
        }
        {
            var Q0;
            Q0 = qSketchRegion(id + "F22", true);
            extrude(context, id + "F23", {"entities" : qUnion([Q0]), "operationType" : NewBodyOperationType.ADD, "oppositeDirection" : true, "depth" : .6 * mm, "offsetDistance" : 25 * mm});
        }
        {
            var Q0;
            Q0=qCreatedBy(makeId("Top.planeOp"),FACE);
            var sketch = newSketch(context, id + "F24", { "sketchPlane" : qUnion([Q0])});
            skLineSegment(sketch, "E133.bottom", {"start": v(-13.73, -17.97) * mm, "end": v(-13.17, -18.54) * mm});
            skLineSegment(sketch, "E133.top", {"start": v(-34.38, -38.62) * mm, "end": v(-33.81, -39.19) * mm});
            skLineSegment(sketch, "E133.left", {"start": v(-13.73, -17.97) * mm, "end": v(-34.38, -38.62) * mm});
            skLineSegment(sketch, "E133.right", {"start": v(-13.17, -18.54) * mm, "end": v(-33.81, -39.19) * mm});
            skPoint(sketch, "E133.middle", {"position": v(-23.77, -28.58) * mm});
            skLineSegment(sketch, "E134.bottom", {"start": v(-16, -29.85) * mm, "end": v(-15.43, -30.42) * mm});
            skLineSegment(sketch, "E134.top", {"start": v(-29.57, -43.43) * mm, "end": v(-29, -44) * mm});
            skLineSegment(sketch, "E134.left", {"start": v(-16, -29.85) * mm, "end": v(-29.57, -43.43) * mm});
            skLineSegment(sketch, "E134.right", {"start": v(-15.43, -30.42) * mm, "end": v(-29, -44) * mm});
            skPoint(sketch, "E134.middle", {"position": v(-22.5, -36.92) * mm});
            skLineSegment(sketch, "E135.bottom", {"start": v(-15.43, -38.9) * mm, "end": v(-14.86, -39.47) * mm});
            skLineSegment(sketch, "E135.top", {"start": v(-24.76, -48.24) * mm, "end": v(-24.2, -48.8) * mm});
            skLineSegment(sketch, "E135.left", {"start": v(-15.43, -38.9) * mm, "end": v(-24.76, -48.24) * mm});
            skLineSegment(sketch, "E135.right", {"start": v(-14.86, -39.47) * mm, "end": v(-24.2, -48.8) * mm});
            skPoint(sketch, "E135.middle", {"position": v(-19.81, -43.85) * mm});
            skLineSegment(sketch, "E136.bottom", {"start": v(-12, -45.1) * mm, "end": v(-11.43, -45.66) * mm});
            skLineSegment(sketch, "E136.top", {"start": v(-19.95, -53.05) * mm, "end": v(-19.39, -53.61) * mm});
            skLineSegment(sketch, "E136.left", {"start": v(-12, -45.1) * mm, "end": v(-19.95, -53.05) * mm});
            skLineSegment(sketch, "E136.right", {"start": v(-11.43, -45.66) * mm, "end": v(-19.39, -53.61) * mm});
            skPoint(sketch, "E136.middle", {"position": v(-15.7, -49.35) * mm});
            skLineSegment(sketch, "E137.MirrorCS", {"start": v(-38.9, -15.43) * mm, "end": v(-39.47, -14.86) * mm});
            skLineSegment(sketch, "E138.MirrorCS", {"start": v(-43.43, -29.57) * mm, "end": v(-44, -29) * mm});
            skLineSegment(sketch, "E139.MirrorCS", {"start": v(-53.05, -19.95) * mm, "end": v(-53.61, -19.39) * mm});
            skLineSegment(sketch, "E140.MirrorCS", {"start": v(-29.85, -16) * mm, "end": v(-30.42, -15.43) * mm});
            skLineSegment(sketch, "E141.MirrorCS", {"start": v(-48.24, -24.76) * mm, "end": v(-48.8, -24.2) * mm});
            skLineSegment(sketch, "E142.MirrorCS", {"start": v(-45.1, -12) * mm, "end": v(-45.66, -11.43) * mm});
            skLineSegment(sketch, "E143.MirrorCS", {"start": v(-30.42, -15.43) * mm, "end": v(-44, -29) * mm});
            skLineSegment(sketch, "E144.MirrorCS", {"start": v(-29.85, -16) * mm, "end": v(-43.43, -29.57) * mm});
            skLineSegment(sketch, "E145.MirrorCS", {"start": v(-39.47, -14.86) * mm, "end": v(-48.8, -24.2) * mm});
            skLineSegment(sketch, "E146.MirrorCS", {"start": v(-38.9, -15.43) * mm, "end": v(-48.24, -24.76) * mm});
            skLineSegment(sketch, "E147.MirrorCS", {"start": v(-45.66, -11.43) * mm, "end": v(-53.61, -19.39) * mm});
            skPoint(sketch, "E148.MirrorP", {"position": v(-36.92, -22.5) * mm});
            skPoint(sketch, "E149.MirrorP", {"position": v(-49.35, -15.7) * mm});
            skLineSegment(sketch, "E150.MirrorCS", {"start": v(-45.1, -12) * mm, "end": v(-53.05, -19.95) * mm});
            skPoint(sketch, "E151.MirrorP", {"position": v(-43.85, -19.81) * mm});
            skLineSegment(sketch, "E152.MirrorCS", {"start": v(-38.62, -34.38) * mm, "end": v(-39.19, -33.81) * mm});
            skLineSegment(sketch, "E153.MirrorCS", {"start": v(-17.97, -13.73) * mm, "end": v(-18.54, -13.17) * mm});
            skLineSegment(sketch, "E154.MirrorCS", {"start": v(-18.54, -13.17) * mm, "end": v(-39.19, -33.81) * mm});
            skLineSegment(sketch, "E155.MirrorCS", {"start": v(-17.97, -13.73) * mm, "end": v(-38.62, -34.38) * mm});
            skPoint(sketch, "E156.MirrorP", {"position": v(-28.58, -23.77) * mm});
            skLineSegment(sketch, "E157.1.0", {"start": v(45.1, -12) * mm, "end": v(53.05, -19.95) * mm});
            skLineSegment(sketch, "E157.1.1", {"start": v(45.66, -11.43) * mm, "end": v(53.61, -19.39) * mm});
            skLineSegment(sketch, "E157.1.2", {"start": v(17.97, -13.73) * mm, "end": v(38.62, -34.38) * mm});
            skLineSegment(sketch, "E157.1.3", {"start": v(18.54, -13.17) * mm, "end": v(39.19, -33.81) * mm});
            skLineSegment(sketch, "E157.1.4", {"start": v(29.85, -16) * mm, "end": v(43.43, -29.57) * mm});
            skLineSegment(sketch, "E157.1.5", {"start": v(30.42, -15.43) * mm, "end": v(44, -29) * mm});
            skLineSegment(sketch, "E157.1.6", {"start": v(38.9, -15.43) * mm, "end": v(48.24, -24.76) * mm});
            skLineSegment(sketch, "E157.1.7", {"start": v(39.47, -14.86) * mm, "end": v(48.8, -24.2) * mm});
            skLineSegment(sketch, "E157.1.8", {"start": v(13.17, -18.54) * mm, "end": v(33.81, -39.19) * mm});
            skLineSegment(sketch, "E157.1.9", {"start": v(13.73, -17.97) * mm, "end": v(34.38, -38.62) * mm});
            skPoint(sketch, "E157.1.10", {"position": v(28.58, -23.77) * mm});
            skPoint(sketch, "E157.1.11", {"position": v(36.92, -22.5) * mm});
            skPoint(sketch, "E157.1.12", {"position": v(43.85, -19.81) * mm});
            skPoint(sketch, "E157.1.13", {"position": v(49.35, -15.7) * mm});
            skPoint(sketch, "E157.1.14", {"position": v(22.5, -36.92) * mm});
            skPoint(sketch, "E157.1.15", {"position": v(15.7, -49.35) * mm});
            skLineSegment(sketch, "E157.1.16", {"start": v(15.43, -30.42) * mm, "end": v(29, -44) * mm});
            skPoint(sketch, "E157.1.17", {"position": v(19.81, -43.85) * mm});
            skLineSegment(sketch, "E157.1.18", {"start": v(16, -29.85) * mm, "end": v(29.57, -43.43) * mm});
            skPoint(sketch, "E157.1.19", {"position": v(23.77, -28.58) * mm});
            skLineSegment(sketch, "E157.1.20", {"start": v(14.86, -39.47) * mm, "end": v(24.2, -48.8) * mm});
            skLineSegment(sketch, "E157.1.21", {"start": v(15.43, -38.9) * mm, "end": v(24.76, -48.24) * mm});
            skLineSegment(sketch, "E157.1.22", {"start": v(11.43, -45.66) * mm, "end": v(19.39, -53.61) * mm});
            skLineSegment(sketch, "E157.1.23", {"start": v(12, -45.1) * mm, "end": v(19.95, -53.05) * mm});
            skLineSegment(sketch, "E157.1.24", {"start": v(53.05, -19.95) * mm, "end": v(53.61, -19.39) * mm});
            skLineSegment(sketch, "E157.1.25", {"start": v(17.97, -13.73) * mm, "end": v(18.54, -13.17) * mm});
            skLineSegment(sketch, "E157.1.26", {"start": v(38.62, -34.38) * mm, "end": v(39.19, -33.81) * mm});
            skLineSegment(sketch, "E157.1.27", {"start": v(29.85, -16) * mm, "end": v(30.42, -15.43) * mm});
            skLineSegment(sketch, "E157.1.28", {"start": v(43.43, -29.57) * mm, "end": v(44, -29) * mm});
            skLineSegment(sketch, "E157.1.29", {"start": v(38.9, -15.43) * mm, "end": v(39.47, -14.86) * mm});
            skLineSegment(sketch, "E157.1.30", {"start": v(48.24, -24.76) * mm, "end": v(48.8, -24.2) * mm});
            skLineSegment(sketch, "E157.1.31", {"start": v(45.1, -12) * mm, "end": v(45.66, -11.43) * mm});
            skLineSegment(sketch, "E157.1.32", {"start": v(13.73, -17.97) * mm, "end": v(13.17, -18.54) * mm});
            skLineSegment(sketch, "E157.1.33", {"start": v(15.43, -38.9) * mm, "end": v(14.86, -39.47) * mm});
            skLineSegment(sketch, "E157.1.34", {"start": v(29.57, -43.43) * mm, "end": v(29, -44) * mm});
            skLineSegment(sketch, "E157.1.35", {"start": v(19.95, -53.05) * mm, "end": v(19.39, -53.61) * mm});
            skLineSegment(sketch, "E157.1.36", {"start": v(16, -29.85) * mm, "end": v(15.43, -30.42) * mm});
            skLineSegment(sketch, "E157.1.37", {"start": v(24.76, -48.24) * mm, "end": v(24.2, -48.8) * mm});
            skLineSegment(sketch, "E157.1.38", {"start": v(12, -45.1) * mm, "end": v(11.43, -45.66) * mm});
            skLineSegment(sketch, "E157.1.39", {"start": v(34.38, -38.62) * mm, "end": v(33.81, -39.19) * mm});
            skLineSegment(sketch, "E157.2.0", {"start": v(12, 45.1) * mm, "end": v(19.95, 53.05) * mm});
            skLineSegment(sketch, "E157.2.1", {"start": v(11.43, 45.66) * mm, "end": v(19.39, 53.61) * mm});
            skLineSegment(sketch, "E157.2.2", {"start": v(13.73, 17.97) * mm, "end": v(34.38, 38.62) * mm});
            skLineSegment(sketch, "E157.2.3", {"start": v(13.17, 18.54) * mm, "end": v(33.81, 39.19) * mm});
            skLineSegment(sketch, "E157.2.4", {"start": v(16, 29.85) * mm, "end": v(29.57, 43.43) * mm});
            skLineSegment(sketch, "E157.2.5", {"start": v(15.43, 30.42) * mm, "end": v(29, 44) * mm});
            skLineSegment(sketch, "E157.2.6", {"start": v(15.43, 38.9) * mm, "end": v(24.76, 48.24) * mm});
            skLineSegment(sketch, "E157.2.7", {"start": v(14.86, 39.47) * mm, "end": v(24.2, 48.8) * mm});
            skLineSegment(sketch, "E157.2.8", {"start": v(18.54, 13.17) * mm, "end": v(39.19, 33.81) * mm});
            skLineSegment(sketch, "E157.2.9", {"start": v(17.97, 13.73) * mm, "end": v(38.62, 34.38) * mm});
            skPoint(sketch, "E157.2.10", {"position": v(23.77, 28.58) * mm});
            skPoint(sketch, "E157.2.11", {"position": v(22.5, 36.92) * mm});
            skPoint(sketch, "E157.2.12", {"position": v(19.81, 43.85) * mm});
            skPoint(sketch, "E157.2.13", {"position": v(15.7, 49.35) * mm});
            skPoint(sketch, "E157.2.14", {"position": v(36.92, 22.5) * mm});
            skPoint(sketch, "E157.2.15", {"position": v(49.35, 15.7) * mm});
            skLineSegment(sketch, "E157.2.16", {"start": v(30.42, 15.43) * mm, "end": v(44, 29) * mm});
            skPoint(sketch, "E157.2.17", {"position": v(43.85, 19.81) * mm});
            skLineSegment(sketch, "E157.2.18", {"start": v(29.85, 16) * mm, "end": v(43.43, 29.57) * mm});
            skPoint(sketch, "E157.2.19", {"position": v(28.58, 23.77) * mm});
            skLineSegment(sketch, "E157.2.20", {"start": v(39.47, 14.86) * mm, "end": v(48.8, 24.2) * mm});
            skLineSegment(sketch, "E157.2.21", {"start": v(38.9, 15.43) * mm, "end": v(48.24, 24.76) * mm});
            skLineSegment(sketch, "E157.2.22", {"start": v(45.66, 11.43) * mm, "end": v(53.61, 19.39) * mm});
            skLineSegment(sketch, "E157.2.23", {"start": v(45.1, 12) * mm, "end": v(53.05, 19.95) * mm});
            skLineSegment(sketch, "E157.2.24", {"start": v(19.95, 53.05) * mm, "end": v(19.39, 53.61) * mm});
            skLineSegment(sketch, "E157.2.25", {"start": v(13.73, 17.97) * mm, "end": v(13.17, 18.54) * mm});
            skLineSegment(sketch, "E157.2.26", {"start": v(34.38, 38.62) * mm, "end": v(33.81, 39.19) * mm});
            skLineSegment(sketch, "E157.2.27", {"start": v(16, 29.85) * mm, "end": v(15.43, 30.42) * mm});
            skLineSegment(sketch, "E157.2.28", {"start": v(29.57, 43.43) * mm, "end": v(29, 44) * mm});
            skLineSegment(sketch, "E157.2.29", {"start": v(15.43, 38.9) * mm, "end": v(14.86, 39.47) * mm});
            skLineSegment(sketch, "E157.2.30", {"start": v(24.76, 48.24) * mm, "end": v(24.2, 48.8) * mm});
            skLineSegment(sketch, "E157.2.31", {"start": v(12, 45.1) * mm, "end": v(11.43, 45.66) * mm});
            skLineSegment(sketch, "E157.2.32", {"start": v(17.97, 13.73) * mm, "end": v(18.54, 13.17) * mm});
            skLineSegment(sketch, "E157.2.33", {"start": v(38.9, 15.43) * mm, "end": v(39.47, 14.86) * mm});
            skLineSegment(sketch, "E157.2.34", {"start": v(43.43, 29.57) * mm, "end": v(44, 29) * mm});
            skLineSegment(sketch, "E157.2.35", {"start": v(53.05, 19.95) * mm, "end": v(53.61, 19.39) * mm});
            skLineSegment(sketch, "E157.2.36", {"start": v(29.85, 16) * mm, "end": v(30.42, 15.43) * mm});
            skLineSegment(sketch, "E157.2.37", {"start": v(48.24, 24.76) * mm, "end": v(48.8, 24.2) * mm});
            skLineSegment(sketch, "E157.2.38", {"start": v(45.1, 12) * mm, "end": v(45.66, 11.43) * mm});
            skLineSegment(sketch, "E157.2.39", {"start": v(38.62, 34.38) * mm, "end": v(39.19, 33.81) * mm});
            skLineSegment(sketch, "E157.3.0", {"start": v(-45.1, 12) * mm, "end": v(-53.05, 19.95) * mm});
            skLineSegment(sketch, "E157.3.1", {"start": v(-45.66, 11.43) * mm, "end": v(-53.61, 19.39) * mm});
            skLineSegment(sketch, "E157.3.2", {"start": v(-17.97, 13.73) * mm, "end": v(-38.62, 34.38) * mm});
            skLineSegment(sketch, "E157.3.3", {"start": v(-18.54, 13.17) * mm, "end": v(-39.19, 33.81) * mm});
            skLineSegment(sketch, "E157.3.4", {"start": v(-29.85, 16) * mm, "end": v(-43.43, 29.57) * mm});
            skLineSegment(sketch, "E157.3.5", {"start": v(-30.42, 15.43) * mm, "end": v(-44, 29) * mm});
            skLineSegment(sketch, "E157.3.6", {"start": v(-38.9, 15.43) * mm, "end": v(-48.24, 24.76) * mm});
            skLineSegment(sketch, "E157.3.7", {"start": v(-39.47, 14.86) * mm, "end": v(-48.8, 24.2) * mm});
            skLineSegment(sketch, "E157.3.8", {"start": v(-13.17, 18.54) * mm, "end": v(-33.81, 39.19) * mm});
            skLineSegment(sketch, "E157.3.9", {"start": v(-13.73, 17.97) * mm, "end": v(-34.38, 38.62) * mm});
            skPoint(sketch, "E157.3.10", {"position": v(-28.58, 23.77) * mm});
            skPoint(sketch, "E157.3.11", {"position": v(-36.92, 22.5) * mm});
            skPoint(sketch, "E157.3.12", {"position": v(-43.85, 19.81) * mm});
            skPoint(sketch, "E157.3.13", {"position": v(-49.35, 15.7) * mm});
            skPoint(sketch, "E157.3.14", {"position": v(-22.5, 36.92) * mm});
            skPoint(sketch, "E157.3.15", {"position": v(-15.7, 49.35) * mm});
            skLineSegment(sketch, "E157.3.16", {"start": v(-15.43, 30.42) * mm, "end": v(-29, 44) * mm});
            skPoint(sketch, "E157.3.17", {"position": v(-19.81, 43.85) * mm});
            skLineSegment(sketch, "E157.3.18", {"start": v(-16, 29.85) * mm, "end": v(-29.57, 43.43) * mm});
            skPoint(sketch, "E157.3.19", {"position": v(-23.77, 28.58) * mm});
            skLineSegment(sketch, "E157.3.20", {"start": v(-14.86, 39.47) * mm, "end": v(-24.2, 48.8) * mm});
            skLineSegment(sketch, "E157.3.21", {"start": v(-15.43, 38.9) * mm, "end": v(-24.76, 48.24) * mm});
            skLineSegment(sketch, "E157.3.22", {"start": v(-11.43, 45.66) * mm, "end": v(-19.39, 53.61) * mm});
            skLineSegment(sketch, "E157.3.23", {"start": v(-12, 45.1) * mm, "end": v(-19.95, 53.05) * mm});
            skLineSegment(sketch, "E157.3.24", {"start": v(-53.05, 19.95) * mm, "end": v(-53.61, 19.39) * mm});
            skLineSegment(sketch, "E157.3.25", {"start": v(-17.97, 13.73) * mm, "end": v(-18.54, 13.17) * mm});
            skLineSegment(sketch, "E157.3.26", {"start": v(-38.62, 34.38) * mm, "end": v(-39.19, 33.81) * mm});
            skLineSegment(sketch, "E157.3.27", {"start": v(-29.85, 16) * mm, "end": v(-30.42, 15.43) * mm});
            skLineSegment(sketch, "E157.3.28", {"start": v(-43.43, 29.57) * mm, "end": v(-44, 29) * mm});
            skLineSegment(sketch, "E157.3.29", {"start": v(-38.9, 15.43) * mm, "end": v(-39.47, 14.86) * mm});
            skLineSegment(sketch, "E157.3.30", {"start": v(-48.24, 24.76) * mm, "end": v(-48.8, 24.2) * mm});
            skLineSegment(sketch, "E157.3.31", {"start": v(-45.1, 12) * mm, "end": v(-45.66, 11.43) * mm});
            skLineSegment(sketch, "E157.3.32", {"start": v(-13.73, 17.97) * mm, "end": v(-13.17, 18.54) * mm});
            skLineSegment(sketch, "E157.3.33", {"start": v(-15.43, 38.9) * mm, "end": v(-14.86, 39.47) * mm});
            skLineSegment(sketch, "E157.3.34", {"start": v(-29.57, 43.43) * mm, "end": v(-29, 44) * mm});
            skLineSegment(sketch, "E157.3.35", {"start": v(-19.95, 53.05) * mm, "end": v(-19.39, 53.61) * mm});
            skLineSegment(sketch, "E157.3.36", {"start": v(-16, 29.85) * mm, "end": v(-15.43, 30.42) * mm});
            skLineSegment(sketch, "E157.3.37", {"start": v(-24.76, 48.24) * mm, "end": v(-24.2, 48.8) * mm});
            skLineSegment(sketch, "E157.3.38", {"start": v(-12, 45.1) * mm, "end": v(-11.43, 45.66) * mm});
            skLineSegment(sketch, "E157.3.39", {"start": v(-34.38, 38.62) * mm, "end": v(-33.81, 39.19) * mm});
            skPoint(sketch, "E157.center", {"position": v(0, 0) * mm});
            skSolve(sketch);
        }
        {
            var Q0;
            Q0 = qSketchRegion(id + "F24", true);
            extrude(context, id + "F25", {"entities" : qUnion([Q0]), "operationType" : NewBodyOperationType.ADD, "depth" : .6 * mm, "offsetDistance" : 25 * mm});
        }
        {
            var Q0;
            {var subQ0=makeQuery(id+"F15.opExtrude","CAP_FACE",FACE,{"disambiguationData":[OSD([sQuery(id+"F10.wireOp",EDGE,"E66.bottom"),sQuery(id+"F10.wireOp",EDGE,"E66.top"),sQuery(id+"F10.wireOp",EDGE,"E66.right"),sQuery(id+"F10.wireOp",EDGE,"E67.0.1.1"),sQuery(id+"F10.wireOp",EDGE,"E67.0.1.2"),sQuery(id+"F10.wireOp",EDGE,"E67.0.1.3"),sQuery(id+"F10.wireOp",EDGE,"E67.0.2.1"),sQuery(id+"F10.wireOp",EDGE,"E67.0.2.2"),sQuery(id+"F10.wireOp",EDGE,"E67.0.2.3"),sQuery(id+"F10.wireOp",EDGE,"E67.0.3.1"),sQuery(id+"F10.wireOp",EDGE,"E67.0.3.2"),sQuery(id+"F10.wireOp",EDGE,"E67.0.3.3"),sQuery(id+"F10.wireOp",EDGE,"E67.0.4.1"),sQuery(id+"F10.wireOp",EDGE,"E67.0.4.2"),sQuery(id+"F10.wireOp",EDGE,"E67.0.4.3"),sQuery(id+"F10.wireOp",EDGE,"f8f007aa-b1cc-4542-abcf-356018b7fdd71.MirrorCS"),sQuery(id+"F10.wireOp",EDGE,"E71.MirrorCS"),sQuery(id+"F10.wireOp",EDGE,"f8f007aa-b1cc-4542-abcf-356018b7fdd76.MirrorCS"),sQuery(id+"F10.wireOp",EDGE,"E72.MirrorCS"),sQuery(id+"F10.wireOp",EDGE,"f8f007aa-b1cc-4542-abcf-356018b7fdd78.MirrorCS"),sQuery(id+"F10.wireOp",EDGE,"E73.MirrorCS"),sQuery(id+"F10.wireOp",EDGE,"E75.MirrorCS"),sQuery(id+"F10.wireOp",EDGE,"f8f007aa-b1cc-4542-abcf-356018b7fdd712.MirrorCS"),sQuery(id+"F10.wireOp",EDGE,"f8f007aa-b1cc-4542-abcf-356018b7fdd713.MirrorCS"),sQuery(id+"F10.wireOp",EDGE,"E76.MirrorCS"),sQuery(id+"F10.wireOp",EDGE,"E77.MirrorCS"),sQuery(id+"F10.wireOp",EDGE,"E78.MirrorCS"),sQuery(id+"F10.wireOp",EDGE,"f8f007aa-b1cc-4542-abcf-356018b7fdd718.MirrorCS"),sQuery(id+"F10.wireOp",EDGE,"f8f007aa-b1cc-4542-abcf-356018b7fdd719.MirrorCS"),sQuery(id+"F10.wireOp",EDGE,"E690.MirrorCS"),sQuery(id+"F10.wireOp",EDGE,"E79.bottom"),sQuery(id+"F10.wireOp",EDGE,"E79.top"),sQuery(id+"F10.wireOp",EDGE,"E79.left"),sQuery(id+"F10.wireOp",EDGE,"E80.0.1.0"),sQuery(id+"F10.wireOp",EDGE,"E80.0.1.1"),sQuery(id+"F10.wireOp",EDGE,"E80.0.1.2"),sQuery(id+"F10.wireOp",EDGE,"E80.0.2.0"),sQuery(id+"F10.wireOp",EDGE,"E80.0.2.1"),sQuery(id+"F10.wireOp",EDGE,"E80.0.2.2"),sQuery(id+"F10.wireOp",EDGE,"E82.MirrorCS"),sQuery(id+"F10.wireOp",EDGE,"E83.MirrorCS"),sQuery(id+"F10.wireOp",EDGE,"E86.MirrorCS"),sQuery(id+"F10.wireOp",EDGE,"E87.MirrorCS"),sQuery(id+"F10.wireOp",EDGE,"E88.MirrorCS"),sQuery(id+"F10.wireOp",EDGE,"E90.MirrorCS"),sQuery(id+"F10.wireOp",EDGE,"E91.MirrorCS"),sQuery(id+"F10.wireOp",EDGE,"E92.MirrorCS"),sQuery(id+"F10.wireOp",EDGE,"E93.MirrorCS"),sQuery(id+"F10.wireOp",EDGE,"E95.bottom"),sQuery(id+"F10.wireOp",EDGE,"E95.top"),sQuery(id+"F10.wireOp",EDGE,"E95.left"),sQuery(id+"F10.wireOp",EDGE,"E95.right"),sQuery(id+"F10.wireOp",EDGE,"E96")])],"isStart":false});var subQ1=makeQuery(id+"F4.opExtrude","CAP_FACE",FACE,{"disambiguationData":[OSD([sQuery(id+"F3.wireOp",EDGE,"E37.bottom"),sQuery(id+"F3.wireOp",EDGE,"E37.top"),sQuery(id+"F3.wireOp",EDGE,"E37.left"),sQuery(id+"F3.wireOp",EDGE,"E37.right"),sQuery(id+"F3.wireOp",EDGE,"E38.bottom"),sQuery(id+"F3.wireOp",EDGE,"E38.top"),sQuery(id+"F3.wireOp",EDGE,"E38.left"),sQuery(id+"F3.wireOp",EDGE,"E38.right"),sQuery(id+"F3.wireOp",EDGE,"E39.bottom"),sQuery(id+"F3.wireOp",EDGE,"E39.top"),sQuery(id+"F3.wireOp",EDGE,"E40.left"),sQuery(id+"F3.wireOp",EDGE,"E40.right"),sQuery(id+"F3.wireOp",EDGE,"E41.trimOffspring"),sQuery(id+"F3.wireOp",EDGE,"E42.trimOffspring"),sQuery(id+"F3.wireOp",EDGE,"E43.trimOffspring"),sQuery(id+"F3.wireOp",EDGE,"E44.trimOffspring"),sQuery(id+"F3.wireOp",EDGE,"E45.trimOffspring"),sQuery(id+"F3.wireOp",EDGE,"E46.trimOffspring"),sQuery(id+"F3.wireOp",EDGE,"E47.trimOffspring"),sQuery(id+"F3.wireOp",EDGE,"E48.trimOffspring")])],"isStart":true});Q0=makeQuery(id+"F23.boolean.opBoolean","MERGE",FACE,{"derivedFrom":[makeQuery(id+"F21.opBoolean","MERGE",FACE,{"derivedFrom":[makeQuery(id+"F2.opExtrude","CAP_FACE",FACE,{"disambiguationData":[OSD([sQuery(id+"F1.wireOp",EDGE,"E6.bottom"),sQuery(id+"F1.wireOp",EDGE,"E6.top"),sQuery(id+"F1.wireOp",EDGE,"E6.left"),sQuery(id+"F1.wireOp",EDGE,"E6.right"),sQuery(id+"F1.wireOp",EDGE,"E7.bottom"),sQuery(id+"F1.wireOp",EDGE,"E7.top"),sQuery(id+"F1.wireOp",EDGE,"E7.left"),sQuery(id+"F1.wireOp",EDGE,"E7.right"),sQuery(id+"F1.wireOp",EDGE,"E8.bottom"),sQuery(id+"F1.wireOp",EDGE,"E8.top"),sQuery(id+"F1.wireOp",EDGE,"E8.left"),sQuery(id+"F1.wireOp",EDGE,"E8.right"),sQuery(id+"F1.wireOp",EDGE,"E9.trimOffspring"),sQuery(id+"F1.wireOp",EDGE,"E10.trimOffspring"),sQuery(id+"F1.wireOp",EDGE,"E11.left"),sQuery(id+"F1.wireOp",EDGE,"E11.right"),sQuery(id+"F1.wireOp",EDGE,"E14.trimOffspring"),sQuery(id+"F1.wireOp",EDGE,"E15.trimOffspring"),sQuery(id+"F1.wireOp",EDGE,"E16"),sQuery(id+"F1.wireOp",EDGE,"E17"),sQuery(id+"F1.wireOp",EDGE,"E18"),sQuery(id+"F1.wireOp",EDGE,"E19"),sQuery(id+"F1.wireOp",EDGE,"E20"),sQuery(id+"F1.wireOp",EDGE,"E25.trimOffspring"),sQuery(id+"F1.wireOp",EDGE,"E26.trimOffspring"),sQuery(id+"F1.wireOp",EDGE,"E27.trimOffspring"),sQuery(id+"F1.wireOp",EDGE,"E28.trimOffspring"),sQuery(id+"F1.wireOp",EDGE,"E29.trimOffspring"),sQuery(id+"F1.wireOp",EDGE,"E30.trimOffspring"),sQuery(id+"F1.wireOp",EDGE,"E31.bottom"),sQuery(id+"F1.wireOp",EDGE,"E31.top"),sQuery(id+"F1.wireOp",EDGE,"E31.left"),sQuery(id+"F1.wireOp",EDGE,"E31.right"),sQuery(id+"F1.wireOp",EDGE,"E32"),sQuery(id+"F1.wireOp",EDGE,"E33"),sQuery(id+"F1.wireOp",EDGE,"E34.trimOffspring"),sQuery(id+"F1.wireOp",EDGE,"E35.trimOffspring"),sQuery(id+"F1.wireOp",EDGE,"E36.trimOffspring")])],"isStart":true}),makeQuery(id+"F12.boolean.opBoolean","MERGE",FACE,{"derivedFrom":[makeQuery(id+"F9.opBoolean","MERGE",FACE,{"derivedFrom":[makeQuery(id+"F6.opPattern","COPY",FACE,{"derivedFrom":subQ1,"instanceName":"1"}),makeQuery(id+"F6.opPattern","COPY",FACE,{"derivedFrom":subQ1,"instanceName":"2"}),makeQuery(id+"F6.opPattern","COPY",FACE,{"derivedFrom":subQ1,"instanceName":"3"}),makeQuery(id+"FO8zS28IN7wsPAr_2.boolean.opBoolean","MERGE",FACE,{"derivedFrom":[subQ1,makeQuery(id+"FO8zS28IN7wsPAr_2.opExtrude","CAP_FACE",FACE,{"disambiguationData":[OSD([sQuery(id+"FGKSyKOM8flHIr0_2.wireOp",EDGE,"6WZHuQLm-4oZA-5b05-mLcp-LwPe52Hc8LRo.bottom"),sQuery(id+"FGKSyKOM8flHIr0_2.wireOp",EDGE,"6WZHuQLm-4oZA-5b05-mLcp-LwPe52Hc8LRo.top"),sQuery(id+"FGKSyKOM8flHIr0_2.wireOp",EDGE,"6WZHuQLm-4oZA-5b05-mLcp-LwPe52Hc8LRo.left"),sQuery(id+"FGKSyKOM8flHIr0_2.wireOp",EDGE,"6WZHuQLm-4oZA-5b05-mLcp-LwPe52Hc8LRo.right")])],"isStart":false})]}),makeQuery(id+"F8.opExtrude","CAP_FACE",FACE,{"disambiguationData":[OSD([sQuery(id+"F7.wireOp",EDGE,"E50"),sQuery(id+"F7.wireOp",EDGE,"E51"),sQuery(id+"F7.wireOp",EDGE,"E52"),sQuery(id+"F7.wireOp",EDGE,"E53"),sQuery(id+"F7.wireOp",EDGE,"E54"),sQuery(id+"F7.wireOp",EDGE,"E55"),sQuery(id+"F7.wireOp",EDGE,"E56"),sQuery(id+"F7.wireOp",EDGE,"E57"),sQuery(id+"F7.wireOp",EDGE,"E58"),sQuery(id+"F7.wireOp",EDGE,"E59"),sQuery(id+"F7.wireOp",EDGE,"E60"),sQuery(id+"F7.wireOp",EDGE,"E61"),sQuery(id+"F7.wireOp",EDGE,"E62"),sQuery(id+"F7.wireOp",EDGE,"E63"),sQuery(id+"F7.wireOp",EDGE,"E64"),sQuery(id+"F7.wireOp",EDGE,"E65")])],"isStart":false})]}),makeQuery(id+"F12.opExtrude","CAP_FACE",FACE,{"disambiguationData":[OSD([sQuery(id+"F11.wireOp",EDGE,"E101.bottom"),sQuery(id+"F11.wireOp",EDGE,"E101.top"),sQuery(id+"F11.wireOp",EDGE,"E101.left"),sQuery(id+"F11.wireOp",EDGE,"E101.right")])],"isStart":true}),makeQuery(id+"F12.opExtrude","CAP_FACE",FACE,{"disambiguationData":[OSD([sQuery(id+"F11.wireOp",EDGE,"E102.bottom"),sQuery(id+"F11.wireOp",EDGE,"E102.top"),sQuery(id+"F11.wireOp",EDGE,"E102.left"),sQuery(id+"F11.wireOp",EDGE,"E102.right")])],"isStart":true}),makeQuery(id+"F12.opExtrude","CAP_FACE",FACE,{"disambiguationData":[OSD([sQuery(id+"F11.wireOp",EDGE,"E103.bottom"),sQuery(id+"F11.wireOp",EDGE,"E103.top"),sQuery(id+"F11.wireOp",EDGE,"E103.left"),sQuery(id+"F11.wireOp",EDGE,"E103.right")])],"isStart":true}),makeQuery(id+"F12.opExtrude","CAP_FACE",FACE,{"disambiguationData":[OSD([sQuery(id+"F11.wireOp",EDGE,"E104.1.0"),sQuery(id+"F11.wireOp",EDGE,"E104.1.1"),sQuery(id+"F11.wireOp",EDGE,"E104.1.6"),sQuery(id+"F11.wireOp",EDGE,"E104.1.11")])],"isStart":true}),makeQuery(id+"F12.opExtrude","CAP_FACE",FACE,{"disambiguationData":[OSD([sQuery(id+"F11.wireOp",EDGE,"E104.1.2"),sQuery(id+"F11.wireOp",EDGE,"E104.1.4"),sQuery(id+"F11.wireOp",EDGE,"E104.1.7"),sQuery(id+"F11.wireOp",EDGE,"E104.1.8")])],"isStart":true}),makeQuery(id+"F12.opExtrude","CAP_FACE",FACE,{"disambiguationData":[OSD([sQuery(id+"F11.wireOp",EDGE,"E104.1.3"),sQuery(id+"F11.wireOp",EDGE,"E104.1.5"),sQuery(id+"F11.wireOp",EDGE,"E104.1.9"),sQuery(id+"F11.wireOp",EDGE,"E104.1.10")])],"isStart":true}),makeQuery(id+"F12.opExtrude","CAP_FACE",FACE,{"disambiguationData":[OSD([sQuery(id+"F11.wireOp",EDGE,"E104.2.0"),sQuery(id+"F11.wireOp",EDGE,"E104.2.1"),sQuery(id+"F11.wireOp",EDGE,"E104.2.6"),sQuery(id+"F11.wireOp",EDGE,"E104.2.11")])],"isStart":true}),makeQuery(id+"F12.opExtrude","CAP_FACE",FACE,{"disambiguationData":[OSD([sQuery(id+"F11.wireOp",EDGE,"E104.2.2"),sQuery(id+"F11.wireOp",EDGE,"E104.2.4"),sQuery(id+"F11.wireOp",EDGE,"E104.2.7"),sQuery(id+"F11.wireOp",EDGE,"E104.2.8")])],"isStart":true}),makeQuery(id+"F12.opExtrude","CAP_FACE",FACE,{"disambiguationData":[OSD([sQuery(id+"F11.wireOp",EDGE,"E104.2.3"),sQuery(id+"F11.wireOp",EDGE,"E104.2.5"),sQuery(id+"F11.wireOp",EDGE,"E104.2.9"),sQuery(id+"F11.wireOp",EDGE,"E104.2.10")])],"isStart":true}),makeQuery(id+"F12.opExtrude","CAP_FACE",FACE,{"disambiguationData":[OSD([sQuery(id+"F11.wireOp",EDGE,"E104.3.0"),sQuery(id+"F11.wireOp",EDGE,"E104.3.1"),sQuery(id+"F11.wireOp",EDGE,"E104.3.6"),sQuery(id+"F11.wireOp",EDGE,"E104.3.11")])],"isStart":true}),makeQuery(id+"F12.opExtrude","CAP_FACE",FACE,{"disambiguationData":[OSD([sQuery(id+"F11.wireOp",EDGE,"E104.3.2"),sQuery(id+"F11.wireOp",EDGE,"E104.3.4"),sQuery(id+"F11.wireOp",EDGE,"E104.3.7"),sQuery(id+"F11.wireOp",EDGE,"E104.3.8")])],"isStart":true}),makeQuery(id+"F12.opExtrude","CAP_FACE",FACE,{"disambiguationData":[OSD([sQuery(id+"F11.wireOp",EDGE,"E104.3.3"),sQuery(id+"F11.wireOp",EDGE,"E104.3.5"),sQuery(id+"F11.wireOp",EDGE,"E104.3.9"),sQuery(id+"F11.wireOp",EDGE,"E104.3.10")])],"isStart":true})]}),makeQuery(id+"F17.opBoolean","MERGE",FACE,{"derivedFrom":[subQ0,makeQuery(id+"F16.opPattern","COPY",FACE,{"derivedFrom":subQ0,"instanceName":"1"}),makeQuery(id+"F16.opPattern","COPY",FACE,{"derivedFrom":subQ0,"instanceName":"2"}),makeQuery(id+"F16.opPattern","COPY",FACE,{"derivedFrom":subQ0,"instanceName":"3"})]})]}),makeQuery(id+"F23.opExtrude","CAP_FACE",FACE,{"disambiguationData":[OSD([sQuery(id+"F22.wireOp",EDGE,"E127.bottom"),sQuery(id+"F22.wireOp",EDGE,"E127.top"),sQuery(id+"F22.wireOp",EDGE,"E127.left"),sQuery(id+"F22.wireOp",EDGE,"E127.right")])],"isStart":false}),makeQuery(id+"F23.opExtrude","CAP_FACE",FACE,{"disambiguationData":[OSD([sQuery(id+"F22.wireOp",EDGE,"E128.bottom"),sQuery(id+"F22.wireOp",EDGE,"E128.top"),sQuery(id+"F22.wireOp",EDGE,"E128.left"),sQuery(id+"F22.wireOp",EDGE,"E128.right")])],"isStart":false}),makeQuery(id+"F23.opExtrude","CAP_FACE",FACE,{"disambiguationData":[OSD([sQuery(id+"F22.wireOp",EDGE,"E129.bottom"),sQuery(id+"F22.wireOp",EDGE,"E129.top"),sQuery(id+"F22.wireOp",EDGE,"E129.left"),sQuery(id+"F22.wireOp",EDGE,"E129.right")])],"isStart":false}),makeQuery(id+"F23.opExtrude","CAP_FACE",FACE,{"disambiguationData":[OSD([sQuery(id+"F22.wireOp",EDGE,"E130.bottom"),sQuery(id+"F22.wireOp",EDGE,"E130.top"),sQuery(id+"F22.wireOp",EDGE,"E130.left"),sQuery(id+"F22.wireOp",EDGE,"E130.right")])],"isStart":false}),makeQuery(id+"F23.opExtrude","CAP_FACE",FACE,{"disambiguationData":[OSD([sQuery(id+"F22.wireOp",EDGE,"E131.bottom"),sQuery(id+"F22.wireOp",EDGE,"E131.top"),sQuery(id+"F22.wireOp",EDGE,"E131.left"),sQuery(id+"F22.wireOp",EDGE,"E131.right")])],"isStart":false}),makeQuery(id+"F23.opExtrude","CAP_FACE",FACE,{"disambiguationData":[OSD([sQuery(id+"F22.wireOp",EDGE,"E132.1.0"),sQuery(id+"F22.wireOp",EDGE,"E132.1.8"),sQuery(id+"F22.wireOp",EDGE,"E132.1.20"),sQuery(id+"F22.wireOp",EDGE,"E132.1.24")])],"isStart":false}),makeQuery(id+"F23.opExtrude","CAP_FACE",FACE,{"disambiguationData":[OSD([sQuery(id+"F22.wireOp",EDGE,"E132.1.1"),sQuery(id+"F22.wireOp",EDGE,"E132.1.4"),sQuery(id+"F22.wireOp",EDGE,"E132.1.16"),sQuery(id+"F22.wireOp",EDGE,"E132.1.21")])],"isStart":false}),makeQuery(id+"F23.opExtrude","CAP_FACE",FACE,{"disambiguationData":[OSD([sQuery(id+"F22.wireOp",EDGE,"E132.1.3"),sQuery(id+"F22.wireOp",EDGE,"E132.1.10"),sQuery(id+"F22.wireOp",EDGE,"E132.1.15"),sQuery(id+"F22.wireOp",EDGE,"E132.1.22")])],"isStart":false}),makeQuery(id+"F23.opExtrude","CAP_FACE",FACE,{"disambiguationData":[OSD([sQuery(id+"F22.wireOp",EDGE,"E132.1.6"),sQuery(id+"F22.wireOp",EDGE,"E132.1.7"),sQuery(id+"F22.wireOp",EDGE,"E132.1.17"),sQuery(id+"F22.wireOp",EDGE,"E132.1.18")])],"isStart":false}),makeQuery(id+"F23.opExtrude","CAP_FACE",FACE,{"disambiguationData":[OSD([sQuery(id+"F22.wireOp",EDGE,"E132.1.12"),sQuery(id+"F22.wireOp",EDGE,"E132.1.13"),sQuery(id+"F22.wireOp",EDGE,"E132.1.19"),sQuery(id+"F22.wireOp",EDGE,"E132.1.23")])],"isStart":false}),makeQuery(id+"F23.opExtrude","CAP_FACE",FACE,{"disambiguationData":[OSD([sQuery(id+"F22.wireOp",EDGE,"E132.2.0"),sQuery(id+"F22.wireOp",EDGE,"E132.2.8"),sQuery(id+"F22.wireOp",EDGE,"E132.2.20"),sQuery(id+"F22.wireOp",EDGE,"E132.2.24")])],"isStart":false}),makeQuery(id+"F23.opExtrude","CAP_FACE",FACE,{"disambiguationData":[OSD([sQuery(id+"F22.wireOp",EDGE,"E132.2.1"),sQuery(id+"F22.wireOp",EDGE,"E132.2.4"),sQuery(id+"F22.wireOp",EDGE,"E132.2.16"),sQuery(id+"F22.wireOp",EDGE,"E132.2.21")])],"isStart":false}),makeQuery(id+"F23.opExtrude","CAP_FACE",FACE,{"disambiguationData":[OSD([sQuery(id+"F22.wireOp",EDGE,"E132.2.3"),sQuery(id+"F22.wireOp",EDGE,"E132.2.10"),sQuery(id+"F22.wireOp",EDGE,"E132.2.15"),sQuery(id+"F22.wireOp",EDGE,"E132.2.22")])],"isStart":false}),makeQuery(id+"F23.opExtrude","CAP_FACE",FACE,{"disambiguationData":[OSD([sQuery(id+"F22.wireOp",EDGE,"E132.2.6"),sQuery(id+"F22.wireOp",EDGE,"E132.2.7"),sQuery(id+"F22.wireOp",EDGE,"E132.2.17"),sQuery(id+"F22.wireOp",EDGE,"E132.2.18")])],"isStart":false}),makeQuery(id+"F23.opExtrude","CAP_FACE",FACE,{"disambiguationData":[OSD([sQuery(id+"F22.wireOp",EDGE,"E132.2.12"),sQuery(id+"F22.wireOp",EDGE,"E132.2.13"),sQuery(id+"F22.wireOp",EDGE,"E132.2.19"),sQuery(id+"F22.wireOp",EDGE,"E132.2.23")])],"isStart":false}),makeQuery(id+"F23.opExtrude","CAP_FACE",FACE,{"disambiguationData":[OSD([sQuery(id+"F22.wireOp",EDGE,"E132.3.0"),sQuery(id+"F22.wireOp",EDGE,"E132.3.8"),sQuery(id+"F22.wireOp",EDGE,"E132.3.20"),sQuery(id+"F22.wireOp",EDGE,"E132.3.24")])],"isStart":false}),makeQuery(id+"F23.opExtrude","CAP_FACE",FACE,{"disambiguationData":[OSD([sQuery(id+"F22.wireOp",EDGE,"E132.3.1"),sQuery(id+"F22.wireOp",EDGE,"E132.3.4"),sQuery(id+"F22.wireOp",EDGE,"E132.3.16"),sQuery(id+"F22.wireOp",EDGE,"E132.3.21")])],"isStart":false}),makeQuery(id+"F23.opExtrude","CAP_FACE",FACE,{"disambiguationData":[OSD([sQuery(id+"F22.wireOp",EDGE,"E132.3.3"),sQuery(id+"F22.wireOp",EDGE,"E132.3.10"),sQuery(id+"F22.wireOp",EDGE,"E132.3.15"),sQuery(id+"F22.wireOp",EDGE,"E132.3.22")])],"isStart":false}),makeQuery(id+"F23.opExtrude","CAP_FACE",FACE,{"disambiguationData":[OSD([sQuery(id+"F22.wireOp",EDGE,"E132.3.6"),sQuery(id+"F22.wireOp",EDGE,"E132.3.7"),sQuery(id+"F22.wireOp",EDGE,"E132.3.17"),sQuery(id+"F22.wireOp",EDGE,"E132.3.18")])],"isStart":false}),makeQuery(id+"F23.opExtrude","CAP_FACE",FACE,{"disambiguationData":[OSD([sQuery(id+"F22.wireOp",EDGE,"E132.3.12"),sQuery(id+"F22.wireOp",EDGE,"E132.3.13"),sQuery(id+"F22.wireOp",EDGE,"E132.3.19"),sQuery(id+"F22.wireOp",EDGE,"E132.3.23")])],"isStart":false})]});}
            var sketch = newSketch(context, id + "F26", { "sketchPlane" : qUnion([Q0])});
            skCircle(sketch, "E158", {"center": v(0, 0) * mm, "radius": 4.5 * mm});
            skSolve(sketch);
        }
        {
            var Q0;
            Q0 = qSketchRegion(id + "F26", true);
            extrude(context, id + "F27", {"entities" : qUnion([Q0]), "depth" : 96 * mm, "offsetDistance" : 25 * mm});
        }
        {
            var Q0;
            Q0=makeQuery(id+"F27.opExtrude","CAP_FACE",FACE,{"disambiguationData":[OSD([sQuery(id+"F26.wireOp",EDGE,"E158")])],"isStart":true});
            var sketch = newSketch(context, id + "F28", { "sketchPlane" : qUnion([Q0])});
            skCircle(sketch, "E159", {"center": v(0, 0) * mm, "radius": 3 * mm});
            skSolve(sketch);
        }
        {
            var Q0;
            Q0 = qSketchRegion(id + "F28", true);
            extrude(context, id + "F29", {"entities" : qUnion([Q0]), "operationType" : NewBodyOperationType.ADD, "depth" : 10 * mm, "offsetDistance" : 25 * mm});
        }
        {
            var Q0;
            Q0=makeQuery(id+"F2.opExtrude","CAP_FACE",FACE,{"disambiguationData":[OSD([sQuery(id+"F1.wireOp",EDGE,"E6.bottom"),sQuery(id+"F1.wireOp",EDGE,"E6.top"),sQuery(id+"F1.wireOp",EDGE,"E6.left"),sQuery(id+"F1.wireOp",EDGE,"E6.right"),sQuery(id+"F1.wireOp",EDGE,"E7.bottom"),sQuery(id+"F1.wireOp",EDGE,"E7.top"),sQuery(id+"F1.wireOp",EDGE,"E7.left"),sQuery(id+"F1.wireOp",EDGE,"E7.right"),sQuery(id+"F1.wireOp",EDGE,"E8.bottom"),sQuery(id+"F1.wireOp",EDGE,"E8.top"),sQuery(id+"F1.wireOp",EDGE,"E8.left"),sQuery(id+"F1.wireOp",EDGE,"E8.right"),sQuery(id+"F1.wireOp",EDGE,"E9.trimOffspring"),sQuery(id+"F1.wireOp",EDGE,"E10.trimOffspring"),sQuery(id+"F1.wireOp",EDGE,"E11.left"),sQuery(id+"F1.wireOp",EDGE,"E11.right"),sQuery(id+"F1.wireOp",EDGE,"E14.trimOffspring"),sQuery(id+"F1.wireOp",EDGE,"E15.trimOffspring"),sQuery(id+"F1.wireOp",EDGE,"E16"),sQuery(id+"F1.wireOp",EDGE,"E17"),sQuery(id+"F1.wireOp",EDGE,"E18"),sQuery(id+"F1.wireOp",EDGE,"E19"),sQuery(id+"F1.wireOp",EDGE,"E20"),sQuery(id+"F1.wireOp",EDGE,"E25.trimOffspring"),sQuery(id+"F1.wireOp",EDGE,"E26.trimOffspring"),sQuery(id+"F1.wireOp",EDGE,"E27.trimOffspring"),sQuery(id+"F1.wireOp",EDGE,"E28.trimOffspring"),sQuery(id+"F1.wireOp",EDGE,"E29.trimOffspring"),sQuery(id+"F1.wireOp",EDGE,"E30.trimOffspring"),sQuery(id+"F1.wireOp",EDGE,"E31.bottom"),sQuery(id+"F1.wireOp",EDGE,"E31.top"),sQuery(id+"F1.wireOp",EDGE,"E31.left"),sQuery(id+"F1.wireOp",EDGE,"E31.right"),sQuery(id+"F1.wireOp",EDGE,"E32"),sQuery(id+"F1.wireOp",EDGE,"E33"),sQuery(id+"F1.wireOp",EDGE,"E34.trimOffspring"),sQuery(id+"F1.wireOp",EDGE,"E35.trimOffspring"),sQuery(id+"F1.wireOp",EDGE,"E36.trimOffspring")])],"isStart":false});
            var sketch = newSketch(context, id + "F30", { "sketchPlane" : qUnion([Q0])});
            skArc(sketch, "E160", {"start": v(1.1, 4.36) * mm, "mid": v(0, 4.5) * mm, "end": v(-1.1, 4.36) * mm});
            skLineSegment(sketch, "E161", {"start": v(1.1, -4.36) * mm, "end": v(1.1, 4.36) * mm});
            skLineSegment(sketch, "E162", {"start": v(-1.1, -4.36) * mm, "end": v(-1.1, 4.36) * mm});
            skArc(sketch, "E163.trimOffspring", {"start": v(-1.1, -4.36) * mm, "mid": v(0, -4.5) * mm, "end": v(1.1, -4.36) * mm});
            skSolve(sketch);
        }
        {
            var Q0;
            Q0 = qSketchRegion(id + "F30", true);
            var Q1;
            Q1=makeQuery(id+"F29.opExtrude","CAP_FACE",FACE,{"disambiguationData":[OSD([sQuery(id+"F28.wireOp",EDGE,"E159")])],"isStart":false});
            var Q2;
            Q2=makeQuery(id+"F29.opExtrude","CAP_FACE",FACE,{"disambiguationData":[OSD([sQuery(id+"F28.wireOp",EDGE,"E159")])],"isStart":false});
            extrude(context, id + "F31", {"entities" : qUnion([Q0]), "operationType" : NewBodyOperationType.ADD, "endBound" : BoundingType.UP_TO_SURFACE, "depth" : 4 * mm, "endBoundEntityFace" : qUnion([Q1]), "offsetDistance" : 25 * mm, "hasSecondDirection" : true, "secondDirectionOppositeDirection" : true, "secondDirectionDepth" : 1 * mm, "secondDirectionBoundEntityFace" : qUnion([Q2])});
        }
        {
            var Q0;
            {var subQ0=sQuery(id+"F30.wireOp",EDGE,"E163.trimOffspring");var subQ1=sQuery(id+"F30.wireOp",EDGE,"E161");Q0=makeQuery(id+"F31.boolean.opBoolean","SPLIT",EDGE,{"disambiguationData":[TD([makeQuery(id+"F31.opExtrude","SWEPT_FACE",FACE,{"disambiguationData":[OSD([subQ0])]})])],"derivedFrom":makeQuery(id+"F31.opExtrude","CAP_EDGE",EDGE,{"disambiguationData":[OSD([subQ1])],"isStart":true})});}
            chamfer(context, id + "F32", {"entities" : qUnion([Q0]), "chamferType" : ChamferType.TWO_OFFSETS, "width1" : 1.2 * mm, "oppositeDirection" : false, "width2" : 3 * mm, "tangentPropagation" : true});
        }
        {
            var Q0;
            {var subQ0=sQuery(id+"F30.wireOp",EDGE,"E160");var subQ1=sQuery(id+"F30.wireOp",EDGE,"E162");Q0=makeQuery(id+"F31.boolean.opBoolean","SPLIT",EDGE,{"disambiguationData":[TD([makeQuery(id+"F31.opExtrude","SWEPT_FACE",FACE,{"disambiguationData":[OSD([subQ0])]})])],"derivedFrom":makeQuery(id+"F31.opExtrude","CAP_EDGE",EDGE,{"disambiguationData":[OSD([subQ1])],"isStart":true})});}
            chamfer(context, id + "F33", {"entities" : qUnion([Q0]), "chamferType" : ChamferType.TWO_OFFSETS, "width1" : 3 * mm, "oppositeDirection" : false, "width2" : 1.2 * mm, "tangentPropagation" : true});
        }
        {
            var Q0;
            Q0=makeQuery(id+"F2.opExtrude","CAP_EDGE",EDGE,{"disambiguationData":[OSD([sQuery(id+"F1.wireOp",EDGE,"E7.left")])],"isStart":false});
            chamfer(context, id + "F34", {"entities" : qUnion([Q0]), "chamferType" : ChamferType.TWO_OFFSETS, "width1" : .5 * mm, "oppositeDirection" : false, "width2" : 1 * mm, "tangentPropagation" : true});
        }
        {
            var Q0;
            Q0=makeQuery(id+"F2.opExtrude","CAP_EDGE",EDGE,{"disambiguationData":[OSD([sQuery(id+"F1.wireOp",EDGE,"E9.trimOffspring")])],"isStart":false});
            chamfer(context, id + "F35", {"entities" : qUnion([Q0]), "chamferType" : ChamferType.TWO_OFFSETS, "width1" : 1 * mm, "oppositeDirection" : false, "width2" : .5 * mm, "tangentPropagation" : true});
        }
        {
            var Q0;
            Q0=qCreatedBy(makeId("Front.planeOp"),FACE);
            var sketch = newSketch(context, id + "F36", { "sketchPlane" : qUnion([Q0])});
            skLineSegment(sketch, "E164", {"start": v(108.6, -12.6) * mm, "end": v(-100.14, -12.6) * mm, "construction": true});
            skLineSegment(sketch, "E165", {"start": v(110.53, -60.6) * mm, "end": v(-103.2, -60.6) * mm, "construction": true});
            skLineSegment(sketch, "E166", {"start": v(3.67, -60.6) * mm, "end": v(2.67, -60.6) * mm});
            skLineSegment(sketch, "E167", {"start": v(2.67, -60.6) * mm, "end": v(2.67, -62.6) * mm});
            skLineSegment(sketch, "E168", {"start": v(2.67, -62.6) * mm, "end": v(3.67, -62.6) * mm});
            skLineSegment(sketch, "E169", {"start": v(3.67, -62.6) * mm, "end": v(3.67, -66.6) * mm});
            skLineSegment(sketch, "E170", {"start": v(3.67, -66.6) * mm, "end": v(2.67, -66.6) * mm});
            skLineSegment(sketch, "E171", {"start": v(2.67, -66.6) * mm, "end": v(2.67, -68.6) * mm});
            skLineSegment(sketch, "E172", {"start": v(2.67, -68.6) * mm, "end": v(3.67, -68.6) * mm});
            skLineSegment(sketch, "E173", {"start": v(3.67, -68.6) * mm, "end": v(3.67, -72.6) * mm});
            skLineSegment(sketch, "E174", {"start": v(3.67, -72.6) * mm, "end": v(2.67, -72.6) * mm});
            skLineSegment(sketch, "E175", {"start": v(2.67, -72.6) * mm, "end": v(2.67, -74.6) * mm});
            skLineSegment(sketch, "E176", {"start": v(2.67, -74.6) * mm, "end": v(3.67, -74.6) * mm});
            skLineSegment(sketch, "E177", {"start": v(3.67, -74.6) * mm, "end": v(3.67, -78.6) * mm});
            skLineSegment(sketch, "E178", {"start": v(3.67, -78.6) * mm, "end": v(2.67, -78.6) * mm});
            skLineSegment(sketch, "E179", {"start": v(2.67, -78.6) * mm, "end": v(2.67, -80.6) * mm});
            skLineSegment(sketch, "E180", {"start": v(2.67, -80.6) * mm, "end": v(3.67, -80.6) * mm});
            skLineSegment(sketch, "E181", {"start": v(3.67, -80.6) * mm, "end": v(5.86, -80.6) * mm});
            skLineSegment(sketch, "E182", {"start": v(5.86, -80.6) * mm, "end": v(5.86, -60.6) * mm});
            skLineSegment(sketch, "E183", {"start": v(5.86, -60.6) * mm, "end": v(3.67, -60.6) * mm});
            skSolve(sketch);
        }
        {
            var Q0;
            Q0 = qSketchRegion(id + "F36", true);
            var Q1;
            Q1=sQuery(id+"F5.wireOp",EDGE,"E49");
            revolve(context, id + "F37", {"operationType" : NewBodyOperationType.REMOVE, "surfaceOperationType" : NewSurfaceOperationType.NEW, "entities" : qUnion([Q0]), "axis" : qUnion([Q1]), "revolveType" : RevolveType.FULL, "oppositeDirection" : true});
        }
        {
            var Q0;
            Q0=makeQuery(id+"F2.opExtrude","CAP_FACE",FACE,{"disambiguationData":[OSD([sQuery(id+"F1.wireOp",EDGE,"E6.bottom"),sQuery(id+"F1.wireOp",EDGE,"E6.top"),sQuery(id+"F1.wireOp",EDGE,"E6.left"),sQuery(id+"F1.wireOp",EDGE,"E6.right"),sQuery(id+"F1.wireOp",EDGE,"E7.bottom"),sQuery(id+"F1.wireOp",EDGE,"E7.top"),sQuery(id+"F1.wireOp",EDGE,"E7.left"),sQuery(id+"F1.wireOp",EDGE,"E7.right"),sQuery(id+"F1.wireOp",EDGE,"E8.bottom"),sQuery(id+"F1.wireOp",EDGE,"E8.top"),sQuery(id+"F1.wireOp",EDGE,"E8.left"),sQuery(id+"F1.wireOp",EDGE,"E8.right"),sQuery(id+"F1.wireOp",EDGE,"E9.trimOffspring"),sQuery(id+"F1.wireOp",EDGE,"E10.trimOffspring"),sQuery(id+"F1.wireOp",EDGE,"E11.left"),sQuery(id+"F1.wireOp",EDGE,"E11.right"),sQuery(id+"F1.wireOp",EDGE,"E14.trimOffspring"),sQuery(id+"F1.wireOp",EDGE,"E15.trimOffspring"),sQuery(id+"F1.wireOp",EDGE,"E16"),sQuery(id+"F1.wireOp",EDGE,"E17"),sQuery(id+"F1.wireOp",EDGE,"E18"),sQuery(id+"F1.wireOp",EDGE,"E19"),sQuery(id+"F1.wireOp",EDGE,"E20"),sQuery(id+"F1.wireOp",EDGE,"E25.trimOffspring"),sQuery(id+"F1.wireOp",EDGE,"E26.trimOffspring"),sQuery(id+"F1.wireOp",EDGE,"E27.trimOffspring"),sQuery(id+"F1.wireOp",EDGE,"E28.trimOffspring"),sQuery(id+"F1.wireOp",EDGE,"E29.trimOffspring"),sQuery(id+"F1.wireOp",EDGE,"E30.trimOffspring"),sQuery(id+"F1.wireOp",EDGE,"E31.bottom"),sQuery(id+"F1.wireOp",EDGE,"E31.top"),sQuery(id+"F1.wireOp",EDGE,"E31.left"),sQuery(id+"F1.wireOp",EDGE,"E31.right"),sQuery(id+"F1.wireOp",EDGE,"E32"),sQuery(id+"F1.wireOp",EDGE,"E33"),sQuery(id+"F1.wireOp",EDGE,"E34.trimOffspring"),sQuery(id+"F1.wireOp",EDGE,"E35.trimOffspring"),sQuery(id+"F1.wireOp",EDGE,"E36.trimOffspring")])],"isStart":false});
            var sketch = newSketch(context, id + "F38", { "sketchPlane" : qUnion([Q0])});
            skCircle(sketch, "E184", {"center": v(3.18, 3.18) * mm, "radius": 0.7 * mm});
            skCircle(sketch, "E185", {"center": v(-3.18, -3.18) * mm, "radius": 0.7 * mm});
            skSolve(sketch);
        }
        {
            var Q0;
            Q0 = qSketchRegion(id + "F38", true);
            extrude(context, id + "F39", {"entities" : qUnion([Q0]), "operationType" : NewBodyOperationType.ADD, "depth" : 1 * mm, "offsetDistance" : 25 * mm});
        }
        {
            var Q0;
            Q0=makeQuery(id+"F39.opExtrude","CAP_FACE",FACE,{"disambiguationData":[OSD([sQuery(id+"F38.wireOp",EDGE,"E185")])],"isStart":false});
            var Q1;
            Q1=makeQuery(id+"F39.opExtrude","CAP_FACE",FACE,{"disambiguationData":[OSD([sQuery(id+"F38.wireOp",EDGE,"E184")])],"isStart":false});
            fillet(context, id + "F40", {"entities" : qUnion([Q0, Q1]), "radius" : .7 * mm, "tangentPropagation" : true, "allowEdgeOverflow" : false});
        }
        {
            var Q0;
            Q0=qCreatedBy(makeId("Front.planeOp"),FACE);
            var sketch = newSketch(context, id + "F41", { "sketchPlane" : qUnion([Q0])});
            skArc(sketch, "E186", {"start": v(-63.65, -19.6) * mm, "mid": v(-80.06, -7.67) * mm, "end": v(-96.1, -20.08) * mm});
            skArc(sketch, "E187", {"start": v(-63.65, -19.6) * mm, "mid": v(0, -66.6) * mm, "end": v(63.65, -19.6) * mm});
            skArc(sketch, "E188", {"start": v(-65.73, -21.54) * mm, "mid": v(0, -74.6) * mm, "end": v(65.73, -21.54) * mm});
            skLineSegment(sketch, "E189", {"start": v(-92.56, -74.6) * mm, "end": v(86.1, -74.6) * mm, "construction": true});
            skLineSegment(sketch, "E190", {"start": v(-94.69, -66.6) * mm, "end": v(82.9, -66.6) * mm, "construction": true});
            skArc(sketch, "E191", {"start": v(-65.73, -21.54) * mm, "mid": v(-79.4, -10.17) * mm, "end": v(-93.7, -20.74) * mm});
            skArc(sketch, "E192", {"start": v(-96.1, -20.08) * mm, "mid": v(-95.23, -21.61) * mm, "end": v(-93.7, -20.74) * mm});
            skArc(sketch, "E193.MirrorC", {"start": v(96.1, -20.08) * mm, "mid": v(95.23, -21.61) * mm, "end": v(93.7, -20.74) * mm});
            skArc(sketch, "E194.MirrorC", {"start": v(63.65, -19.6) * mm, "mid": v(80.06, -7.67) * mm, "end": v(96.1, -20.08) * mm});
            skArc(sketch, "E195.MirrorC", {"start": v(65.73, -21.54) * mm, "mid": v(79.4, -10.17) * mm, "end": v(93.7, -20.74) * mm});
            skSolve(sketch);
        }
        {
            var Q0;
            Q0 = qSketchRegion(id + "F41", true);
            extrude(context, id + "F42", {"entities" : qUnion([Q0]), "oppositeDirection" : true, "depth" : 6 * mm, "offsetDistance" : 25 * mm, "hasSecondDirection" : true, "secondDirectionOppositeDirection" : false, "secondDirectionDepth" : 4 * mm});
        }
        {
            var Q0;
            Q0=makeQuery(id+"F27.opExtrude","SWEPT_BODY",BODY,{"disambiguationData":[OSD([sQuery(id+"F26.wireOp",EDGE,"E158")])]});
            var Q1;
            Q1=makeQuery(id+"F42.opExtrude","SWEPT_BODY",BODY,{"disambiguationData":[OSD([sQuery(id+"F41.wireOp",EDGE,"E186"),sQuery(id+"F41.wireOp",EDGE,"E187"),sQuery(id+"F41.wireOp",EDGE,"E188"),sQuery(id+"F41.wireOp",EDGE,"E191"),sQuery(id+"F41.wireOp",EDGE,"E192"),sQuery(id+"F41.wireOp",EDGE,"E193.MirrorC"),sQuery(id+"F41.wireOp",EDGE,"E194.MirrorC"),sQuery(id+"F41.wireOp",EDGE,"E195.MirrorC")])]});
            booleanBodies(context, id + "F43", {"operationType" : BooleanOperationType.SUBTRACTION, "tools" : qUnion([Q0]), "targets" : qUnion([Q1]), "keepTools" : true});
        }
        {
            var Q0;
            Q0=qCreatedBy(makeId("Top.planeOp"),FACE);
            cPlane(context, id + "F44", {"entities" : qUnion([Q0]), "cplaneType" : CPlaneType.OFFSET, "offset" : 80 * mm, "oppositeDirection" : true, "width" : 150 * mm, "height" : 150 * mm});
        }
        {
            var Q0;
            Q0=qCreatedBy(id+"F44.planeOp",FACE);
            var sketch = newSketch(context, id + "F45", { "sketchPlane" : qUnion([Q0])});
            skLineSegment(sketch, "E196.bottom", {"start": v(-2.44, -4.78) * mm, "end": v(2.44, -4.78) * mm});
            skLineSegment(sketch, "E196.top", {"start": v(-2.44, 0.78) * mm, "end": v(2.44, 0.78) * mm});
            skLineSegment(sketch, "E196.left", {"start": v(-2.44, -4.78) * mm, "end": v(-2.44, 0.78) * mm});
            skLineSegment(sketch, "E196.right", {"start": v(2.44, -4.78) * mm, "end": v(2.44, 0.78) * mm});
            skPoint(sketch, "E196.middle", {"position": v(0, -2) * mm});
            skSolve(sketch);
        }
        {
            var Q0;
            Q0 = qSketchRegion(id + "F45", true);
            extrude(context, id + "F46", {"entities" : qUnion([Q0]), "operationType" : NewBodyOperationType.REMOVE, "depth" : 25 * mm, "offsetDistance" : 25 * mm});
        }
        {
            var Q0;
            Q0=qCreatedBy(makeId("Right.planeOp"),FACE);
            var sketch = newSketch(context, id + "F47", { "sketchPlane" : qUnion([Q0])});
            skLineSegment(sketch, "E197.bottom", {"start": v(0, -72.6) * mm, "end": v(-5.65, -72.6) * mm});
            skLineSegment(sketch, "E197.top", {"start": v(0, -68.6) * mm, "end": v(-5.65, -68.6) * mm});
            skLineSegment(sketch, "E197.left", {"start": v(0, -72.6) * mm, "end": v(0, -68.6) * mm});
            skLineSegment(sketch, "E197.right", {"start": v(-5.65, -72.6) * mm, "end": v(-5.65, -68.6) * mm});
            skSolve(sketch);
        }
        {
            var Q0;
            Q0 = qSketchRegion(id + "F47", true);
            extrude(context, id + "F48", {"entities" : qUnion([Q0]), "operationType" : NewBodyOperationType.REMOVE, "oppositeDirection" : true, "depth" : 3.7 * mm, "offsetDistance" : 25 * mm, "hasSecondDirection" : true, "secondDirectionOppositeDirection" : false, "secondDirectionDepth" : 3.7 * mm});
        }
        {
            var Q0;
            Q0=makeQuery(id+"F43.opBoolean","COPY",EDGE,{"derivedFrom":makeQuery(id+"F37.boolean.opBoolean","COPY",EDGE,{"derivedFrom":makeQuery(id+"F37.opRevolve","SWEPT_EDGE",EDGE,{"disambiguationData":[OSD([sQuery(id+"F36.wireOp",EDGE,"E171"),sQuery(id+"F36.wireOp",EDGE,"E172")])]})})});
            var Q1;
            Q1=makeQuery(id+"F43.opBoolean","COPY",EDGE,{"derivedFrom":makeQuery(id+"F37.boolean.opBoolean","COPY",EDGE,{"derivedFrom":makeQuery(id+"F37.opRevolve","SWEPT_EDGE",EDGE,{"disambiguationData":[OSD([sQuery(id+"F36.wireOp",EDGE,"E174"),sQuery(id+"F36.wireOp",EDGE,"E175")])]})})});
            var Q2;
            Q2=makeQuery(id+"F43.opBoolean","INTERSECT",EDGE,{"derivedFrom":[makeQuery(id+"F37.boolean.opBoolean","COPY",FACE,{"derivedFrom":makeQuery(id+"F37.opRevolve","SWEPT_FACE",FACE,{"disambiguationData":[OSD([sQuery(id+"F36.wireOp",EDGE,"E175")])]})}),makeQuery(id+"F42.opExtrude","SWEPT_FACE",FACE,{"disambiguationData":[OSD([sQuery(id+"F41.wireOp",EDGE,"E188")])]})]});
            var Q3;
            Q3=makeQuery(id+"F43.opBoolean","COPY",EDGE,{"disambiguationData":[OD(0.0)],"derivedFrom":makeQuery(id+"F37.boolean.opBoolean","COPY",EDGE,{"derivedFrom":makeQuery(id+"F37.opRevolve","SWEPT_EDGE",EDGE,{"disambiguationData":[OSD([sQuery(id+"F36.wireOp",EDGE,"E170"),sQuery(id+"F36.wireOp",EDGE,"E171")])]})})});
            fillet(context, id + "F49", {"entities" : qUnion([Q0, Q1, Q2, Q3]), "radius" : .5 * mm, "tangentPropagation" : true, "allowEdgeOverflow" : false});
        }
        {
            var Q0;
            {var subQ0=sQuery(id+"F41.wireOp",EDGE,"E187");var subQ1=makeQuery(id+"F46.opExtrude","SWEPT_FACE",FACE,{"disambiguationData":[OSD([sQuery(id+"F45.wireOp",EDGE,"E196.left")])]});var subQ2=makeQuery(id+"F42.opExtrude","CAP_FACE",FACE,{"disambiguationData":[OSD([sQuery(id+"F41.wireOp",EDGE,"E186"),subQ0,sQuery(id+"F41.wireOp",EDGE,"E188"),sQuery(id+"F41.wireOp",EDGE,"E191"),sQuery(id+"F41.wireOp",EDGE,"E192"),sQuery(id+"F41.wireOp",EDGE,"E193.MirrorC"),sQuery(id+"F41.wireOp",EDGE,"E194.MirrorC"),sQuery(id+"F41.wireOp",EDGE,"E195.MirrorC")])],"isStart":true});Q0=makeQuery(id+"F48.boolean.opBoolean","SPLIT",EDGE,{"disambiguationData":[TD([makeQuery(id+"F42.opExtrude","SWEPT_FACE",FACE,{"disambiguationData":[OSD([subQ0])]})])],"derivedFrom":makeQuery(id+"F46.boolean.opBoolean","INTERSECT",EDGE,{"derivedFrom":[subQ2,subQ1]})});}
            var Q1;
            {var subQ0=sQuery(id+"F41.wireOp",EDGE,"E188");var subQ1=sQuery(id+"F41.wireOp",EDGE,"E187");var subQ2=sQuery(id+"F41.wireOp",EDGE,"E191");var subQ3=sQuery(id+"F41.wireOp",EDGE,"E186");var subQ4=sQuery(id+"F41.wireOp",EDGE,"E192");Q1=makeQuery(id+"F48.boolean.opBoolean","INTERSECT",EDGE,{"derivedFrom":[makeQuery(id+"F46.boolean.opBoolean","SPLIT",FACE,{"disambiguationData":[TD([makeQuery(id+"F42.opExtrude","SWEPT_FACE",FACE,{"disambiguationData":[OSD([subQ3])]})])],"derivedFrom":makeQuery(id+"F42.opExtrude","CAP_FACE",FACE,{"disambiguationData":[OSD([subQ3,subQ1,subQ0,subQ2,subQ4,sQuery(id+"F41.wireOp",EDGE,"E193.MirrorC"),sQuery(id+"F41.wireOp",EDGE,"E194.MirrorC"),sQuery(id+"F41.wireOp",EDGE,"E195.MirrorC")])],"isStart":true})}),makeQuery(id+"F48.opExtrude","CAP_FACE",FACE,{"disambiguationData":[OSD([sQuery(id+"F47.wireOp",EDGE,"E197.bottom"),sQuery(id+"F47.wireOp",EDGE,"E197.top"),sQuery(id+"F47.wireOp",EDGE,"E197.left"),sQuery(id+"F47.wireOp",EDGE,"E197.right")])],"isStart":false})]});}
            var Q2;
            {var subQ0=sQuery(id+"F41.wireOp",EDGE,"E188");var subQ1=makeQuery(id+"F46.opExtrude","SWEPT_FACE",FACE,{"disambiguationData":[OSD([sQuery(id+"F45.wireOp",EDGE,"E196.left")])]});var subQ2=makeQuery(id+"F42.opExtrude","CAP_FACE",FACE,{"disambiguationData":[OSD([sQuery(id+"F41.wireOp",EDGE,"E186"),sQuery(id+"F41.wireOp",EDGE,"E187"),subQ0,sQuery(id+"F41.wireOp",EDGE,"E191"),sQuery(id+"F41.wireOp",EDGE,"E192"),sQuery(id+"F41.wireOp",EDGE,"E193.MirrorC"),sQuery(id+"F41.wireOp",EDGE,"E194.MirrorC"),sQuery(id+"F41.wireOp",EDGE,"E195.MirrorC")])],"isStart":true});Q2=makeQuery(id+"F48.boolean.opBoolean","SPLIT",EDGE,{"disambiguationData":[TD([makeQuery(id+"F42.opExtrude","SWEPT_FACE",FACE,{"disambiguationData":[OSD([subQ0])]})])],"derivedFrom":makeQuery(id+"F46.boolean.opBoolean","INTERSECT",EDGE,{"derivedFrom":[subQ2,subQ1]})});}
            var Q3;
            {var subQ0=makeQuery(id+"F46.opExtrude","SWEPT_FACE",FACE,{"disambiguationData":[OSD([sQuery(id+"F45.wireOp",EDGE,"E196.right")])]});var subQ1=sQuery(id+"F41.wireOp",EDGE,"E188");var subQ2=makeQuery(id+"F42.opExtrude","CAP_FACE",FACE,{"disambiguationData":[OSD([sQuery(id+"F41.wireOp",EDGE,"E186"),sQuery(id+"F41.wireOp",EDGE,"E187"),subQ1,sQuery(id+"F41.wireOp",EDGE,"E191"),sQuery(id+"F41.wireOp",EDGE,"E192"),sQuery(id+"F41.wireOp",EDGE,"E193.MirrorC"),sQuery(id+"F41.wireOp",EDGE,"E194.MirrorC"),sQuery(id+"F41.wireOp",EDGE,"E195.MirrorC")])],"isStart":true});Q3=makeQuery(id+"F48.boolean.opBoolean","SPLIT",EDGE,{"disambiguationData":[TD([makeQuery(id+"F42.opExtrude","SWEPT_FACE",FACE,{"disambiguationData":[OSD([subQ1])]})])],"derivedFrom":makeQuery(id+"F46.boolean.opBoolean","INTERSECT",EDGE,{"derivedFrom":[subQ2,subQ0]})});}
            var Q4;
            {var subQ0=makeQuery(id+"F46.opExtrude","SWEPT_FACE",FACE,{"disambiguationData":[OSD([sQuery(id+"F45.wireOp",EDGE,"E196.right")])]});var subQ1=sQuery(id+"F41.wireOp",EDGE,"E187");var subQ2=makeQuery(id+"F42.opExtrude","CAP_FACE",FACE,{"disambiguationData":[OSD([sQuery(id+"F41.wireOp",EDGE,"E186"),subQ1,sQuery(id+"F41.wireOp",EDGE,"E188"),sQuery(id+"F41.wireOp",EDGE,"E191"),sQuery(id+"F41.wireOp",EDGE,"E192"),sQuery(id+"F41.wireOp",EDGE,"E193.MirrorC"),sQuery(id+"F41.wireOp",EDGE,"E194.MirrorC"),sQuery(id+"F41.wireOp",EDGE,"E195.MirrorC")])],"isStart":true});Q4=makeQuery(id+"F48.boolean.opBoolean","SPLIT",EDGE,{"disambiguationData":[TD([makeQuery(id+"F42.opExtrude","SWEPT_FACE",FACE,{"disambiguationData":[OSD([subQ1])]})])],"derivedFrom":makeQuery(id+"F46.boolean.opBoolean","INTERSECT",EDGE,{"derivedFrom":[subQ2,subQ0]})});}
            var Q5;
            {var subQ0=sQuery(id+"F41.wireOp",EDGE,"E193.MirrorC");var subQ1=sQuery(id+"F41.wireOp",EDGE,"E188");var subQ2=sQuery(id+"F41.wireOp",EDGE,"E194.MirrorC");var subQ3=sQuery(id+"F41.wireOp",EDGE,"E187");var subQ4=sQuery(id+"F41.wireOp",EDGE,"E195.MirrorC");Q5=makeQuery(id+"F48.boolean.opBoolean","INTERSECT",EDGE,{"derivedFrom":[makeQuery(id+"F46.boolean.opBoolean","SPLIT",FACE,{"disambiguationData":[TD([makeQuery(id+"F42.opExtrude","SWEPT_FACE",FACE,{"disambiguationData":[OSD([subQ0])]})])],"derivedFrom":makeQuery(id+"F42.opExtrude","CAP_FACE",FACE,{"disambiguationData":[OSD([sQuery(id+"F41.wireOp",EDGE,"E186"),subQ3,subQ1,sQuery(id+"F41.wireOp",EDGE,"E191"),sQuery(id+"F41.wireOp",EDGE,"E192"),subQ0,subQ2,subQ4])],"isStart":true})}),makeQuery(id+"F48.opExtrude","CAP_FACE",FACE,{"disambiguationData":[OSD([sQuery(id+"F47.wireOp",EDGE,"E197.bottom"),sQuery(id+"F47.wireOp",EDGE,"E197.top"),sQuery(id+"F47.wireOp",EDGE,"E197.left"),sQuery(id+"F47.wireOp",EDGE,"E197.right")])],"isStart":true})]});}
            fillet(context, id + "F50", {"entities" : qUnion([Q0, Q1, Q2, Q3, Q4, Q5]), "radius" : 1 * mm, "tangentPropagation" : true, "allowEdgeOverflow" : false});
        }
        {
            var Q0;
            {var subQ0=makeQuery(id+"F15.opExtrude","CAP_FACE",FACE,{"disambiguationData":[OSD([sQuery(id+"F10.wireOp",EDGE,"E66.bottom"),sQuery(id+"F10.wireOp",EDGE,"E66.top"),sQuery(id+"F10.wireOp",EDGE,"E66.right"),sQuery(id+"F10.wireOp",EDGE,"E67.0.1.1"),sQuery(id+"F10.wireOp",EDGE,"E67.0.1.2"),sQuery(id+"F10.wireOp",EDGE,"E67.0.4.2"),sQuery(id+"F10.wireOp",EDGE,"E67.0.4.3"),sQuery(id+"F10.wireOp",EDGE,"E71.MirrorCS"),sQuery(id+"F10.wireOp",EDGE,"E72.MirrorCS"),sQuery(id+"F10.wireOp",EDGE,"E73.MirrorCS"),sQuery(id+"F10.wireOp",EDGE,"E75.MirrorCS"),sQuery(id+"F10.wireOp",EDGE,"E76.MirrorCS"),sQuery(id+"F10.wireOp",EDGE,"E77.MirrorCS"),sQuery(id+"F10.wireOp",EDGE,"E78.MirrorCS"),sQuery(id+"F10.wireOp",EDGE,"E79.bottom"),sQuery(id+"F10.wireOp",EDGE,"E79.top"),sQuery(id+"F10.wireOp",EDGE,"E79.left"),sQuery(id+"F10.wireOp",EDGE,"E80.0.1.0"),sQuery(id+"F10.wireOp",EDGE,"E80.0.1.1"),sQuery(id+"F10.wireOp",EDGE,"E80.0.1.2"),sQuery(id+"F10.wireOp",EDGE,"E80.0.2.0"),sQuery(id+"F10.wireOp",EDGE,"E80.0.2.1"),sQuery(id+"F10.wireOp",EDGE,"E80.0.2.2"),sQuery(id+"F10.wireOp",EDGE,"E82.MirrorCS"),sQuery(id+"F10.wireOp",EDGE,"E83.MirrorCS"),sQuery(id+"F10.wireOp",EDGE,"E86.MirrorCS"),sQuery(id+"F10.wireOp",EDGE,"E87.MirrorCS"),sQuery(id+"F10.wireOp",EDGE,"E88.MirrorCS"),sQuery(id+"F10.wireOp",EDGE,"E90.MirrorCS"),sQuery(id+"F10.wireOp",EDGE,"E91.MirrorCS"),sQuery(id+"F10.wireOp",EDGE,"E92.MirrorCS"),sQuery(id+"F10.wireOp",EDGE,"E93.MirrorCS"),sQuery(id+"F10.wireOp",EDGE,"E95.bottom"),sQuery(id+"F10.wireOp",EDGE,"E95.top"),sQuery(id+"F10.wireOp",EDGE,"E95.left"),sQuery(id+"F10.wireOp",EDGE,"E95.right"),sQuery(id+"F10.wireOp",EDGE,"E96"),sQuery(id+"F10.wireOp",EDGE,"E98"),sQuery(id+"F10.wireOp",EDGE,"E100")])],"isStart":false});var subQ1=makeQuery(id+"F4.opExtrude","CAP_FACE",FACE,{"disambiguationData":[OSD([sQuery(id+"F3.wireOp",EDGE,"E37.bottom"),sQuery(id+"F3.wireOp",EDGE,"E37.top"),sQuery(id+"F3.wireOp",EDGE,"E37.left"),sQuery(id+"F3.wireOp",EDGE,"E37.right"),sQuery(id+"F3.wireOp",EDGE,"E38.bottom"),sQuery(id+"F3.wireOp",EDGE,"E38.top"),sQuery(id+"F3.wireOp",EDGE,"E38.left"),sQuery(id+"F3.wireOp",EDGE,"E38.right"),sQuery(id+"F3.wireOp",EDGE,"E39.bottom"),sQuery(id+"F3.wireOp",EDGE,"E39.top"),sQuery(id+"F3.wireOp",EDGE,"E40.left"),sQuery(id+"F3.wireOp",EDGE,"E40.right"),sQuery(id+"F3.wireOp",EDGE,"E41.trimOffspring"),sQuery(id+"F3.wireOp",EDGE,"E42.trimOffspring"),sQuery(id+"F3.wireOp",EDGE,"E43.trimOffspring"),sQuery(id+"F3.wireOp",EDGE,"E44.trimOffspring"),sQuery(id+"F3.wireOp",EDGE,"E45.trimOffspring"),sQuery(id+"F3.wireOp",EDGE,"E46.trimOffspring"),sQuery(id+"F3.wireOp",EDGE,"E47.trimOffspring"),sQuery(id+"F3.wireOp",EDGE,"E48.trimOffspring")])],"isStart":true});Q0=makeQuery(id+"F23.boolean.opBoolean","MERGE",FACE,{"derivedFrom":[makeQuery(id+"F21.opBoolean","MERGE",FACE,{"derivedFrom":[makeQuery(id+"F2.opExtrude","CAP_FACE",FACE,{"disambiguationData":[OSD([sQuery(id+"F1.wireOp",EDGE,"E6.bottom"),sQuery(id+"F1.wireOp",EDGE,"E6.top"),sQuery(id+"F1.wireOp",EDGE,"E6.left"),sQuery(id+"F1.wireOp",EDGE,"E6.right"),sQuery(id+"F1.wireOp",EDGE,"E7.bottom"),sQuery(id+"F1.wireOp",EDGE,"E7.top"),sQuery(id+"F1.wireOp",EDGE,"E7.left"),sQuery(id+"F1.wireOp",EDGE,"E7.right"),sQuery(id+"F1.wireOp",EDGE,"E8.bottom"),sQuery(id+"F1.wireOp",EDGE,"E8.top"),sQuery(id+"F1.wireOp",EDGE,"E8.left"),sQuery(id+"F1.wireOp",EDGE,"E8.right"),sQuery(id+"F1.wireOp",EDGE,"E9.trimOffspring"),sQuery(id+"F1.wireOp",EDGE,"E10.trimOffspring"),sQuery(id+"F1.wireOp",EDGE,"E11.left"),sQuery(id+"F1.wireOp",EDGE,"E11.right"),sQuery(id+"F1.wireOp",EDGE,"E14.trimOffspring"),sQuery(id+"F1.wireOp",EDGE,"E15.trimOffspring"),sQuery(id+"F1.wireOp",EDGE,"E16"),sQuery(id+"F1.wireOp",EDGE,"E17"),sQuery(id+"F1.wireOp",EDGE,"E18"),sQuery(id+"F1.wireOp",EDGE,"E19"),sQuery(id+"F1.wireOp",EDGE,"E20"),sQuery(id+"F1.wireOp",EDGE,"E25.trimOffspring"),sQuery(id+"F1.wireOp",EDGE,"E26.trimOffspring"),sQuery(id+"F1.wireOp",EDGE,"E27.trimOffspring"),sQuery(id+"F1.wireOp",EDGE,"E28.trimOffspring"),sQuery(id+"F1.wireOp",EDGE,"E29.trimOffspring"),sQuery(id+"F1.wireOp",EDGE,"E30.trimOffspring"),sQuery(id+"F1.wireOp",EDGE,"E31.bottom"),sQuery(id+"F1.wireOp",EDGE,"E31.top"),sQuery(id+"F1.wireOp",EDGE,"E31.left"),sQuery(id+"F1.wireOp",EDGE,"E31.right"),sQuery(id+"F1.wireOp",EDGE,"E32"),sQuery(id+"F1.wireOp",EDGE,"E33"),sQuery(id+"F1.wireOp",EDGE,"E34.trimOffspring"),sQuery(id+"F1.wireOp",EDGE,"E35.trimOffspring"),sQuery(id+"F1.wireOp",EDGE,"E36.trimOffspring")])],"isStart":true}),makeQuery(id+"F12.boolean.opBoolean","MERGE",FACE,{"derivedFrom":[makeQuery(id+"F9.opBoolean","MERGE",FACE,{"derivedFrom":[subQ1,makeQuery(id+"F6.opPattern","COPY",FACE,{"derivedFrom":subQ1,"instanceName":"1"}),makeQuery(id+"F6.opPattern","COPY",FACE,{"derivedFrom":subQ1,"instanceName":"2"}),makeQuery(id+"F6.opPattern","COPY",FACE,{"derivedFrom":subQ1,"instanceName":"3"}),makeQuery(id+"F8.opExtrude","CAP_FACE",FACE,{"disambiguationData":[OSD([sQuery(id+"F7.wireOp",EDGE,"E50"),sQuery(id+"F7.wireOp",EDGE,"E51"),sQuery(id+"F7.wireOp",EDGE,"E52"),sQuery(id+"F7.wireOp",EDGE,"E53"),sQuery(id+"F7.wireOp",EDGE,"E54"),sQuery(id+"F7.wireOp",EDGE,"E55"),sQuery(id+"F7.wireOp",EDGE,"E56"),sQuery(id+"F7.wireOp",EDGE,"E57"),sQuery(id+"F7.wireOp",EDGE,"E58"),sQuery(id+"F7.wireOp",EDGE,"E59"),sQuery(id+"F7.wireOp",EDGE,"E60"),sQuery(id+"F7.wireOp",EDGE,"E61"),sQuery(id+"F7.wireOp",EDGE,"E62"),sQuery(id+"F7.wireOp",EDGE,"E63"),sQuery(id+"F7.wireOp",EDGE,"E64"),sQuery(id+"F7.wireOp",EDGE,"E65")])],"isStart":false})]}),makeQuery(id+"F12.opExtrude","CAP_FACE",FACE,{"disambiguationData":[OSD([sQuery(id+"F11.wireOp",EDGE,"E101.bottom"),sQuery(id+"F11.wireOp",EDGE,"E101.top"),sQuery(id+"F11.wireOp",EDGE,"E101.left"),sQuery(id+"F11.wireOp",EDGE,"E101.right")])],"isStart":true}),makeQuery(id+"F12.opExtrude","CAP_FACE",FACE,{"disambiguationData":[OSD([sQuery(id+"F11.wireOp",EDGE,"E102.bottom"),sQuery(id+"F11.wireOp",EDGE,"E102.top"),sQuery(id+"F11.wireOp",EDGE,"E102.left"),sQuery(id+"F11.wireOp",EDGE,"E102.right")])],"isStart":true}),makeQuery(id+"F12.opExtrude","CAP_FACE",FACE,{"disambiguationData":[OSD([sQuery(id+"F11.wireOp",EDGE,"E103.bottom"),sQuery(id+"F11.wireOp",EDGE,"E103.top"),sQuery(id+"F11.wireOp",EDGE,"E103.left"),sQuery(id+"F11.wireOp",EDGE,"E103.right")])],"isStart":true}),makeQuery(id+"F12.opExtrude","CAP_FACE",FACE,{"disambiguationData":[OSD([sQuery(id+"F11.wireOp",EDGE,"E104.1.0"),sQuery(id+"F11.wireOp",EDGE,"E104.1.1"),sQuery(id+"F11.wireOp",EDGE,"E104.1.6"),sQuery(id+"F11.wireOp",EDGE,"E104.1.11")])],"isStart":true}),makeQuery(id+"F12.opExtrude","CAP_FACE",FACE,{"disambiguationData":[OSD([sQuery(id+"F11.wireOp",EDGE,"E104.1.2"),sQuery(id+"F11.wireOp",EDGE,"E104.1.4"),sQuery(id+"F11.wireOp",EDGE,"E104.1.7"),sQuery(id+"F11.wireOp",EDGE,"E104.1.8")])],"isStart":true}),makeQuery(id+"F12.opExtrude","CAP_FACE",FACE,{"disambiguationData":[OSD([sQuery(id+"F11.wireOp",EDGE,"E104.1.3"),sQuery(id+"F11.wireOp",EDGE,"E104.1.5"),sQuery(id+"F11.wireOp",EDGE,"E104.1.9"),sQuery(id+"F11.wireOp",EDGE,"E104.1.10")])],"isStart":true}),makeQuery(id+"F12.opExtrude","CAP_FACE",FACE,{"disambiguationData":[OSD([sQuery(id+"F11.wireOp",EDGE,"E104.2.0"),sQuery(id+"F11.wireOp",EDGE,"E104.2.1"),sQuery(id+"F11.wireOp",EDGE,"E104.2.6"),sQuery(id+"F11.wireOp",EDGE,"E104.2.11")])],"isStart":true}),makeQuery(id+"F12.opExtrude","CAP_FACE",FACE,{"disambiguationData":[OSD([sQuery(id+"F11.wireOp",EDGE,"E104.2.2"),sQuery(id+"F11.wireOp",EDGE,"E104.2.4"),sQuery(id+"F11.wireOp",EDGE,"E104.2.7"),sQuery(id+"F11.wireOp",EDGE,"E104.2.8")])],"isStart":true}),makeQuery(id+"F12.opExtrude","CAP_FACE",FACE,{"disambiguationData":[OSD([sQuery(id+"F11.wireOp",EDGE,"E104.2.3"),sQuery(id+"F11.wireOp",EDGE,"E104.2.5"),sQuery(id+"F11.wireOp",EDGE,"E104.2.9"),sQuery(id+"F11.wireOp",EDGE,"E104.2.10")])],"isStart":true}),makeQuery(id+"F12.opExtrude","CAP_FACE",FACE,{"disambiguationData":[OSD([sQuery(id+"F11.wireOp",EDGE,"E104.3.0"),sQuery(id+"F11.wireOp",EDGE,"E104.3.1"),sQuery(id+"F11.wireOp",EDGE,"E104.3.6"),sQuery(id+"F11.wireOp",EDGE,"E104.3.11")])],"isStart":true}),makeQuery(id+"F12.opExtrude","CAP_FACE",FACE,{"disambiguationData":[OSD([sQuery(id+"F11.wireOp",EDGE,"E104.3.2"),sQuery(id+"F11.wireOp",EDGE,"E104.3.4"),sQuery(id+"F11.wireOp",EDGE,"E104.3.7"),sQuery(id+"F11.wireOp",EDGE,"E104.3.8")])],"isStart":true}),makeQuery(id+"F12.opExtrude","CAP_FACE",FACE,{"disambiguationData":[OSD([sQuery(id+"F11.wireOp",EDGE,"E104.3.3"),sQuery(id+"F11.wireOp",EDGE,"E104.3.5"),sQuery(id+"F11.wireOp",EDGE,"E104.3.9"),sQuery(id+"F11.wireOp",EDGE,"E104.3.10")])],"isStart":true})]}),makeQuery(id+"F17.opBoolean","MERGE",FACE,{"derivedFrom":[subQ0,makeQuery(id+"F16.opPattern","COPY",FACE,{"derivedFrom":subQ0,"instanceName":"1"}),makeQuery(id+"F16.opPattern","COPY",FACE,{"derivedFrom":subQ0,"instanceName":"2"}),makeQuery(id+"F16.opPattern","COPY",FACE,{"derivedFrom":subQ0,"instanceName":"3"})]})]}),makeQuery(id+"F23.opExtrude","CAP_FACE",FACE,{"disambiguationData":[OSD([sQuery(id+"F22.wireOp",EDGE,"E127.bottom"),sQuery(id+"F22.wireOp",EDGE,"E127.top"),sQuery(id+"F22.wireOp",EDGE,"E127.left"),sQuery(id+"F22.wireOp",EDGE,"E127.right")])],"isStart":false}),makeQuery(id+"F23.opExtrude","CAP_FACE",FACE,{"disambiguationData":[OSD([sQuery(id+"F22.wireOp",EDGE,"E128.bottom"),sQuery(id+"F22.wireOp",EDGE,"E128.top"),sQuery(id+"F22.wireOp",EDGE,"E128.left"),sQuery(id+"F22.wireOp",EDGE,"E128.right")])],"isStart":false}),makeQuery(id+"F23.opExtrude","CAP_FACE",FACE,{"disambiguationData":[OSD([sQuery(id+"F22.wireOp",EDGE,"E129.bottom"),sQuery(id+"F22.wireOp",EDGE,"E129.top"),sQuery(id+"F22.wireOp",EDGE,"E129.left"),sQuery(id+"F22.wireOp",EDGE,"E129.right")])],"isStart":false}),makeQuery(id+"F23.opExtrude","CAP_FACE",FACE,{"disambiguationData":[OSD([sQuery(id+"F22.wireOp",EDGE,"E130.bottom"),sQuery(id+"F22.wireOp",EDGE,"E130.top"),sQuery(id+"F22.wireOp",EDGE,"E130.left"),sQuery(id+"F22.wireOp",EDGE,"E130.right")])],"isStart":false}),makeQuery(id+"F23.opExtrude","CAP_FACE",FACE,{"disambiguationData":[OSD([sQuery(id+"F22.wireOp",EDGE,"E131.bottom"),sQuery(id+"F22.wireOp",EDGE,"E131.top"),sQuery(id+"F22.wireOp",EDGE,"E131.left"),sQuery(id+"F22.wireOp",EDGE,"E131.right")])],"isStart":false}),makeQuery(id+"F23.opExtrude","CAP_FACE",FACE,{"disambiguationData":[OSD([sQuery(id+"F22.wireOp",EDGE,"E132.1.0"),sQuery(id+"F22.wireOp",EDGE,"E132.1.8"),sQuery(id+"F22.wireOp",EDGE,"E132.1.20"),sQuery(id+"F22.wireOp",EDGE,"E132.1.24")])],"isStart":false}),makeQuery(id+"F23.opExtrude","CAP_FACE",FACE,{"disambiguationData":[OSD([sQuery(id+"F22.wireOp",EDGE,"E132.1.1"),sQuery(id+"F22.wireOp",EDGE,"E132.1.4"),sQuery(id+"F22.wireOp",EDGE,"E132.1.16"),sQuery(id+"F22.wireOp",EDGE,"E132.1.21")])],"isStart":false}),makeQuery(id+"F23.opExtrude","CAP_FACE",FACE,{"disambiguationData":[OSD([sQuery(id+"F22.wireOp",EDGE,"E132.1.3"),sQuery(id+"F22.wireOp",EDGE,"E132.1.10"),sQuery(id+"F22.wireOp",EDGE,"E132.1.15"),sQuery(id+"F22.wireOp",EDGE,"E132.1.22")])],"isStart":false}),makeQuery(id+"F23.opExtrude","CAP_FACE",FACE,{"disambiguationData":[OSD([sQuery(id+"F22.wireOp",EDGE,"E132.1.6"),sQuery(id+"F22.wireOp",EDGE,"E132.1.7"),sQuery(id+"F22.wireOp",EDGE,"E132.1.17"),sQuery(id+"F22.wireOp",EDGE,"E132.1.18")])],"isStart":false}),makeQuery(id+"F23.opExtrude","CAP_FACE",FACE,{"disambiguationData":[OSD([sQuery(id+"F22.wireOp",EDGE,"E132.1.12"),sQuery(id+"F22.wireOp",EDGE,"E132.1.13"),sQuery(id+"F22.wireOp",EDGE,"E132.1.19"),sQuery(id+"F22.wireOp",EDGE,"E132.1.23")])],"isStart":false}),makeQuery(id+"F23.opExtrude","CAP_FACE",FACE,{"disambiguationData":[OSD([sQuery(id+"F22.wireOp",EDGE,"E132.2.0"),sQuery(id+"F22.wireOp",EDGE,"E132.2.8"),sQuery(id+"F22.wireOp",EDGE,"E132.2.20"),sQuery(id+"F22.wireOp",EDGE,"E132.2.24")])],"isStart":false}),makeQuery(id+"F23.opExtrude","CAP_FACE",FACE,{"disambiguationData":[OSD([sQuery(id+"F22.wireOp",EDGE,"E132.2.1"),sQuery(id+"F22.wireOp",EDGE,"E132.2.4"),sQuery(id+"F22.wireOp",EDGE,"E132.2.16"),sQuery(id+"F22.wireOp",EDGE,"E132.2.21")])],"isStart":false}),makeQuery(id+"F23.opExtrude","CAP_FACE",FACE,{"disambiguationData":[OSD([sQuery(id+"F22.wireOp",EDGE,"E132.2.3"),sQuery(id+"F22.wireOp",EDGE,"E132.2.10"),sQuery(id+"F22.wireOp",EDGE,"E132.2.15"),sQuery(id+"F22.wireOp",EDGE,"E132.2.22")])],"isStart":false}),makeQuery(id+"F23.opExtrude","CAP_FACE",FACE,{"disambiguationData":[OSD([sQuery(id+"F22.wireOp",EDGE,"E132.2.6"),sQuery(id+"F22.wireOp",EDGE,"E132.2.7"),sQuery(id+"F22.wireOp",EDGE,"E132.2.17"),sQuery(id+"F22.wireOp",EDGE,"E132.2.18")])],"isStart":false}),makeQuery(id+"F23.opExtrude","CAP_FACE",FACE,{"disambiguationData":[OSD([sQuery(id+"F22.wireOp",EDGE,"E132.2.12"),sQuery(id+"F22.wireOp",EDGE,"E132.2.13"),sQuery(id+"F22.wireOp",EDGE,"E132.2.19"),sQuery(id+"F22.wireOp",EDGE,"E132.2.23")])],"isStart":false}),makeQuery(id+"F23.opExtrude","CAP_FACE",FACE,{"disambiguationData":[OSD([sQuery(id+"F22.wireOp",EDGE,"E132.3.0"),sQuery(id+"F22.wireOp",EDGE,"E132.3.8"),sQuery(id+"F22.wireOp",EDGE,"E132.3.20"),sQuery(id+"F22.wireOp",EDGE,"E132.3.24")])],"isStart":false}),makeQuery(id+"F23.opExtrude","CAP_FACE",FACE,{"disambiguationData":[OSD([sQuery(id+"F22.wireOp",EDGE,"E132.3.1"),sQuery(id+"F22.wireOp",EDGE,"E132.3.4"),sQuery(id+"F22.wireOp",EDGE,"E132.3.16"),sQuery(id+"F22.wireOp",EDGE,"E132.3.21")])],"isStart":false}),makeQuery(id+"F23.opExtrude","CAP_FACE",FACE,{"disambiguationData":[OSD([sQuery(id+"F22.wireOp",EDGE,"E132.3.3"),sQuery(id+"F22.wireOp",EDGE,"E132.3.10"),sQuery(id+"F22.wireOp",EDGE,"E132.3.15"),sQuery(id+"F22.wireOp",EDGE,"E132.3.22")])],"isStart":false}),makeQuery(id+"F23.opExtrude","CAP_FACE",FACE,{"disambiguationData":[OSD([sQuery(id+"F22.wireOp",EDGE,"E132.3.6"),sQuery(id+"F22.wireOp",EDGE,"E132.3.7"),sQuery(id+"F22.wireOp",EDGE,"E132.3.17"),sQuery(id+"F22.wireOp",EDGE,"E132.3.18")])],"isStart":false}),makeQuery(id+"F23.opExtrude","CAP_FACE",FACE,{"disambiguationData":[OSD([sQuery(id+"F22.wireOp",EDGE,"E132.3.12"),sQuery(id+"F22.wireOp",EDGE,"E132.3.13"),sQuery(id+"F22.wireOp",EDGE,"E132.3.19"),sQuery(id+"F22.wireOp",EDGE,"E132.3.23")])],"isStart":false})]});}
            var sketch = newSketch(context, id + "F51", { "sketchPlane" : qUnion([Q0])});
            skLineSegment(sketch, "E198.bottom", {"start": v(-61, -11.9) * mm, "end": v(-67, -11.9) * mm});
            skLineSegment(sketch, "E198.top", {"start": v(-61, 12.1) * mm, "end": v(-67, 12.1) * mm});
            skLineSegment(sketch, "E198.left", {"start": v(-61, -11.9) * mm, "end": v(-61, 12.1) * mm});
            skLineSegment(sketch, "E198.right", {"start": v(-67, -11.9) * mm, "end": v(-67, 12.1) * mm});
            skLineSegment(sketch, "E199.1.0", {"start": v(11.9, -61) * mm, "end": v(11.9, -67) * mm});
            skLineSegment(sketch, "E199.1.1", {"start": v(11.9, -61) * mm, "end": v(-12.1, -61) * mm});
            skLineSegment(sketch, "E199.1.2", {"start": v(-12.1, -61) * mm, "end": v(-12.1, -67) * mm});
            skLineSegment(sketch, "E199.1.3", {"start": v(11.9, -67) * mm, "end": v(-12.1, -67) * mm});
            skLineSegment(sketch, "E199.2.0", {"start": v(61, 11.9) * mm, "end": v(67, 11.9) * mm});
            skLineSegment(sketch, "E199.2.1", {"start": v(61, 11.9) * mm, "end": v(61, -12.1) * mm});
            skLineSegment(sketch, "E199.2.2", {"start": v(61, -12.1) * mm, "end": v(67, -12.1) * mm});
            skLineSegment(sketch, "E199.2.3", {"start": v(67, 11.9) * mm, "end": v(67, -12.1) * mm});
            skLineSegment(sketch, "E199.3.0", {"start": v(-11.9, 61) * mm, "end": v(-11.9, 67) * mm});
            skLineSegment(sketch, "E199.3.1", {"start": v(-11.9, 61) * mm, "end": v(12.1, 61) * mm});
            skLineSegment(sketch, "E199.3.2", {"start": v(12.1, 61) * mm, "end": v(12.1, 67) * mm});
            skLineSegment(sketch, "E199.3.3", {"start": v(-11.9, 67) * mm, "end": v(12.1, 67) * mm});
            skPoint(sketch, "E199.center", {"position": v(0, 0) * mm});
            skSolve(sketch);
        }
        {
            var Q0;
            Q0 = qSketchRegion(id + "F51", true);
            extrude(context, id + "F52", {"entities" : qUnion([Q0]), "operationType" : NewBodyOperationType.ADD, "oppositeDirection" : true, "depth" : .2 * mm, "offsetDistance" : 25 * mm});
        }
        {
            var Q0;
            Q0=makeQuery(id+"F52.opExtrude","SWEPT_EDGE",EDGE,{"disambiguationData":[OSD([sQuery(id+"F51.wireOp",EDGE,"E198.top"),sQuery(id+"F51.wireOp",EDGE,"E198.right")])]});
            var Q1;
            Q1=makeQuery(id+"F52.opExtrude","SWEPT_EDGE",EDGE,{"disambiguationData":[OSD([sQuery(id+"F51.wireOp",EDGE,"E198.bottom"),sQuery(id+"F51.wireOp",EDGE,"E198.right")])]});
            var Q2;
            Q2=makeQuery(id+"F52.opExtrude","SWEPT_EDGE",EDGE,{"disambiguationData":[OSD([sQuery(id+"F51.wireOp",EDGE,"E199.3.0"),sQuery(id+"F51.wireOp",EDGE,"E199.3.3")])]});
            var Q3;
            Q3=makeQuery(id+"F52.opExtrude","SWEPT_EDGE",EDGE,{"disambiguationData":[OSD([sQuery(id+"F51.wireOp",EDGE,"E199.3.2"),sQuery(id+"F51.wireOp",EDGE,"E199.3.3")])]});
            var Q4;
            Q4=makeQuery(id+"F52.opExtrude","SWEPT_EDGE",EDGE,{"disambiguationData":[OSD([sQuery(id+"F51.wireOp",EDGE,"E199.2.0"),sQuery(id+"F51.wireOp",EDGE,"E199.2.3")])]});
            var Q5;
            Q5=makeQuery(id+"F52.opExtrude","SWEPT_EDGE",EDGE,{"disambiguationData":[OSD([sQuery(id+"F51.wireOp",EDGE,"E199.2.2"),sQuery(id+"F51.wireOp",EDGE,"E199.2.3")])]});
            var Q6;
            Q6=makeQuery(id+"F52.opExtrude","SWEPT_EDGE",EDGE,{"disambiguationData":[OSD([sQuery(id+"F51.wireOp",EDGE,"E199.1.0"),sQuery(id+"F51.wireOp",EDGE,"E199.1.3")])]});
            var Q7;
            Q7=makeQuery(id+"F52.opExtrude","SWEPT_EDGE",EDGE,{"disambiguationData":[OSD([sQuery(id+"F51.wireOp",EDGE,"E199.1.2"),sQuery(id+"F51.wireOp",EDGE,"E199.1.3")])]});
            fillet(context, id + "F53", {"entities" : qUnion([Q0, Q1, Q2, Q3, Q4, Q5, Q6, Q7]), "radius" : 4 * mm, "tangentPropagation" : true, "allowEdgeOverflow" : false});
        }
        {
            var Q0;
            Q0=makeQuery(id+"F6.opPattern","COPY",EDGE,{"derivedFrom":makeQuery(id+"F4.opExtrude","CAP_EDGE",EDGE,{"disambiguationData":[OSD([sQuery(id+"F3.wireOp",EDGE,"E37.right")])],"isStart":false}),"instanceName":"2"});
            var Q1;
            Q1=makeQuery(id+"F6.opPattern","COPY",EDGE,{"derivedFrom":makeQuery(id+"F4.opExtrude","CAP_EDGE",EDGE,{"disambiguationData":[OSD([sQuery(id+"F3.wireOp",EDGE,"E37.right")])],"isStart":false}),"instanceName":"1"});
            var Q2;
            Q2=makeQuery(id+"F4.opExtrude","CAP_EDGE",EDGE,{"disambiguationData":[OSD([sQuery(id+"F3.wireOp",EDGE,"E37.right")])],"isStart":false});
            var Q3;
            Q3=makeQuery(id+"F6.opPattern","COPY",EDGE,{"derivedFrom":makeQuery(id+"F4.opExtrude","CAP_EDGE",EDGE,{"disambiguationData":[OSD([sQuery(id+"F3.wireOp",EDGE,"E37.right")])],"isStart":false}),"instanceName":"3"});
            chamfer(context, id + "F54", {"entities" : qUnion([Q0, Q1, Q2, Q3]), "chamferType" : ChamferType.TWO_OFFSETS, "width1" : 23 * mm, "oppositeDirection" : false, "width2" : 4 * mm, "tangentPropagation" : true});
        }
        {
            var Q0;
            Q0=qCreatedBy(makeId("Front.planeOp"),FACE);
            var sketch = newSketch(context, id + "F55", { "sketchPlane" : qUnion([Q0])});
            skCircle(sketch, "E200", {"center": v(-26.1, 2.6) * mm, "radius": 1.2 * mm});
            skCircle(sketch, "E201", {"center": v(-40.26, 2) * mm, "radius": 1 * mm});
            skSolve(sketch);
        }
        {
            var Q0;
            Q0 = qSketchRegion(id + "F55", true);
            extrude(context, id + "F56", {"entities" : qUnion([Q0]), "oppositeDirection" : true, "depth" : 13 * mm, "offsetDistance" : 25 * mm, "hasSecondDirection" : true, "secondDirectionOppositeDirection" : false, "secondDirectionDepth" : 13 * mm});
        }
        {
            var Q0;
            Q0=makeQuery(id+"F56.opExtrude","SWEPT_BODY",BODY,{"disambiguationData":[OSD([sQuery(id+"F55.wireOp",EDGE,"E200")])]});
            var Q1;
            Q1=makeQuery(id+"F56.opExtrude","SWEPT_BODY",BODY,{"disambiguationData":[OSD([sQuery(id+"F55.wireOp",EDGE,"E201")])]});
            var Q2;
            Q2=sQuery(id+"F5.wireOp",EDGE,"E49");
            circularPattern(context, id + "F57", {"operationType" : NewBodyOperationType.REMOVE, "entities" : qUnion([Q0, Q1]), "axis" : qUnion([Q2]), "angle" : 360 * degree, "instanceCount" : 4, "equalSpace" : true});
        }
    });
